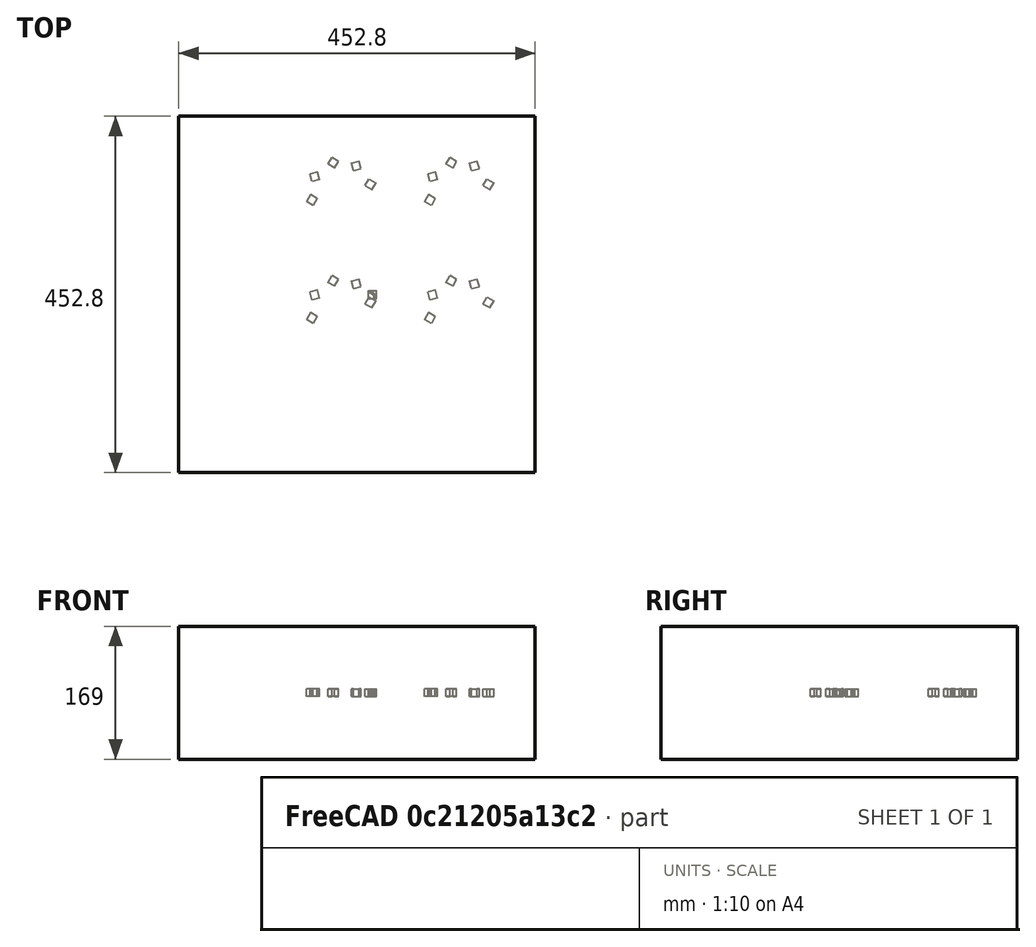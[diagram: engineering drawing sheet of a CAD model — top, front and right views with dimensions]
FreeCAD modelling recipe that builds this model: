
FCSTD DOCUMENT  (FreeCAD 0.21R33694 (Git))
Label: orthoArray-of-polarArray-of-Part
License: All rights reserved
LicenseURL: http://en.wikipedia.org/wiki/All_rights_reserved
objects: App::DocumentObjectGroupPython×1251, Part::FeaturePython×5, App::Part×5
note: 4 computed .brp shape members not serialized (recipe doc carries the construction recipe); baked Part::Feature solids carry a one-line shape summary decoded from their .brp

FEATURE [App::DocumentObjectGroupPython] HALFPI  # scripted group (container) (typed FeaturePython)
  name = HALFPI
  value = pi/2.
FEATURE [App::DocumentObjectGroupPython] PI  # scripted group (container) (typed FeaturePython)
  name = PI
  value = 1.*pi
FEATURE [App::DocumentObjectGroupPython] TWOPI  # scripted group (container) (typed FeaturePython)
  name = TWOPI
  value = 2.*pi
FEATURE [App::DocumentObjectGroupPython] Constants  # scripted group (container) (typed FeaturePython)
  Group = -> [HALFPI,PI,TWOPI]
FEATURE [App::DocumentObjectGroupPython] Variables  # scripted group (container) (typed FeaturePython)
FEATURE [App::DocumentObjectGroupPython] Quantities  # scripted group (container) (typed FeaturePython)
FEATURE [App::DocumentObjectGroupPython] Isotopes  # scripted group (container) (typed FeaturePython)
FEATURE [App::DocumentObjectGroupPython] Elements  # scripted group (container) (typed FeaturePython)
FEATURE [App::DocumentObjectGroupPython] Matrix  # scripted group (container) (typed FeaturePython)
FEATURE [App::DocumentObjectGroupPython] Surfaces  # scripted group (container) (typed FeaturePython)
FEATURE [App::DocumentObjectGroupPython] Opticals  # scripted group (container) (typed FeaturePython)
  Group = -> [Matrix,Surfaces]
FEATURE [App::DocumentObjectGroupPython] G4Isotopes  # scripted group (container) (typed FeaturePython)
FEATURE [App::DocumentObjectGroupPython] H_element  # scripted group (container) (typed FeaturePython)
  Z = 1
  atom_value = 1.008
  formula = H
  name = H_element
FEATURE [App::DocumentObjectGroupPython] He_element  # scripted group (container) (typed FeaturePython)
  Z = 2
  atom_value = 4.0026
  formula = He
  name = He_element
FEATURE [App::DocumentObjectGroupPython] Li_element  # scripted group (container) (typed FeaturePython)
  Z = 3
  atom_value = 6.94
  formula = Li
  name = Li_element
FEATURE [App::DocumentObjectGroupPython] Be_element  # scripted group (container) (typed FeaturePython)
  Z = 4
  atom_value = 9.01218
  formula = Be
  name = Be_element
FEATURE [App::DocumentObjectGroupPython] B_element  # scripted group (container) (typed FeaturePython)
  Z = 5
  atom_value = 10.81
  formula = B
  name = B_element
FEATURE [App::DocumentObjectGroupPython] C_element  # scripted group (container) (typed FeaturePython)
  Z = 6
  atom_value = 12.011
  formula = C
  name = C_element
FEATURE [App::DocumentObjectGroupPython] N_element  # scripted group (container) (typed FeaturePython)
  Z = 7
  atom_value = 14.007
  formula = N
  name = N_element
FEATURE [App::DocumentObjectGroupPython] O_element  # scripted group (container) (typed FeaturePython)
  Z = 8
  atom_value = 15.999
  formula = O
  name = O_element
FEATURE [App::DocumentObjectGroupPython] F_element  # scripted group (container) (typed FeaturePython)
  Z = 9
  atom_value = 18.9984
  formula = F
  name = F_element
FEATURE [App::DocumentObjectGroupPython] Ne_element  # scripted group (container) (typed FeaturePython)
  Z = 10
  atom_value = 20.1797
  formula = Ne
  name = Ne_element
FEATURE [App::DocumentObjectGroupPython] Na_element  # scripted group (container) (typed FeaturePython)
  Z = 11
  atom_value = 22.9898
  formula = Na
  name = Na_element
FEATURE [App::DocumentObjectGroupPython] Mg_element  # scripted group (container) (typed FeaturePython)
  Z = 12
  atom_value = 24.305
  formula = Mg
  name = Mg_element
FEATURE [App::DocumentObjectGroupPython] Al_element  # scripted group (container) (typed FeaturePython)
  Z = 13
  atom_value = 26.9815
  formula = Al
  name = Al_element
FEATURE [App::DocumentObjectGroupPython] Si_element  # scripted group (container) (typed FeaturePython)
  Z = 14
  atom_value = 28.085
  formula = Si
  name = Si_element
FEATURE [App::DocumentObjectGroupPython] P_element  # scripted group (container) (typed FeaturePython)
  Z = 15
  atom_value = 30.9738
  formula = P
  name = P_element
FEATURE [App::DocumentObjectGroupPython] S_element  # scripted group (container) (typed FeaturePython)
  Z = 16
  atom_value = 32.06
  formula = S
  name = S_element
FEATURE [App::DocumentObjectGroupPython] Cl_element  # scripted group (container) (typed FeaturePython)
  Z = 17
  atom_value = 35.45
  formula = Cl
  name = Cl_element
FEATURE [App::DocumentObjectGroupPython] Ar_element  # scripted group (container) (typed FeaturePython)
  Z = 18
  atom_value = 39.95
  formula = Ar
  name = Ar_element
FEATURE [App::DocumentObjectGroupPython] K_element  # scripted group (container) (typed FeaturePython)
  Z = 19
  atom_value = 39.0983
  formula = K
  name = K_element
FEATURE [App::DocumentObjectGroupPython] Ca_element  # scripted group (container) (typed FeaturePython)
  Z = 20
  atom_value = 40.078
  formula = Ca
  name = Ca_element
FEATURE [App::DocumentObjectGroupPython] Sc_element  # scripted group (container) (typed FeaturePython)
  Z = 21
  atom_value = 44.9559
  formula = Sc
  name = Sc_element
FEATURE [App::DocumentObjectGroupPython] Ti_element  # scripted group (container) (typed FeaturePython)
  Z = 22
  atom_value = 47.867
  formula = Ti
  name = Ti_element
FEATURE [App::DocumentObjectGroupPython] V_element  # scripted group (container) (typed FeaturePython)
  Z = 23
  atom_value = 50.9415
  formula = V
  name = V_element
FEATURE [App::DocumentObjectGroupPython] Cr_element  # scripted group (container) (typed FeaturePython)
  Z = 24
  atom_value = 51.9961
  formula = Cr
  name = Cr_element
FEATURE [App::DocumentObjectGroupPython] Mn_element  # scripted group (container) (typed FeaturePython)
  Z = 25
  atom_value = 54.938
  formula = Mn
  name = Mn_element
FEATURE [App::DocumentObjectGroupPython] Fe_element  # scripted group (container) (typed FeaturePython)
  Z = 26
  atom_value = 55.845
  formula = Fe
  name = Fe_element
FEATURE [App::DocumentObjectGroupPython] Co_element  # scripted group (container) (typed FeaturePython)
  Z = 27
  atom_value = 58.9332
  formula = Co
  name = Co_element
FEATURE [App::DocumentObjectGroupPython] Ni_element  # scripted group (container) (typed FeaturePython)
  Z = 28
  atom_value = 58.6934
  formula = Ni
  name = Ni_element
FEATURE [App::DocumentObjectGroupPython] Cu_element  # scripted group (container) (typed FeaturePython)
  Z = 29
  atom_value = 63.546
  formula = Cu
  name = Cu_element
FEATURE [App::DocumentObjectGroupPython] Zn_element  # scripted group (container) (typed FeaturePython)
  Z = 30
  atom_value = 65.38
  formula = Zn
  name = Zn_element
FEATURE [App::DocumentObjectGroupPython] Ga_element  # scripted group (container) (typed FeaturePython)
  Z = 31
  atom_value = 69.723
  formula = Ga
  name = Ga_element
FEATURE [App::DocumentObjectGroupPython] Ge_element  # scripted group (container) (typed FeaturePython)
  Z = 32
  atom_value = 72.63
  formula = Ge
  name = Ge_element
FEATURE [App::DocumentObjectGroupPython] As_element  # scripted group (container) (typed FeaturePython)
  Z = 33
  atom_value = 74.9216
  formula = As
  name = As_element
FEATURE [App::DocumentObjectGroupPython] Se_element  # scripted group (container) (typed FeaturePython)
  Z = 34
  atom_value = 78.971
  formula = Se
  name = Se_element
FEATURE [App::DocumentObjectGroupPython] Br_element  # scripted group (container) (typed FeaturePython)
  Z = 35
  atom_value = 79.904
  formula = Br
  name = Br_element
FEATURE [App::DocumentObjectGroupPython] Kr_element  # scripted group (container) (typed FeaturePython)
  Z = 36
  atom_value = 83.798
  formula = Kr
  name = Kr_element
FEATURE [App::DocumentObjectGroupPython] Rb_element  # scripted group (container) (typed FeaturePython)
  Z = 37
  atom_value = 85.4678
  formula = Rb
  name = Rb_element
FEATURE [App::DocumentObjectGroupPython] Sr_element  # scripted group (container) (typed FeaturePython)
  Z = 38
  atom_value = 87.62
  formula = Sr
  name = Sr_element
FEATURE [App::DocumentObjectGroupPython] Y_element  # scripted group (container) (typed FeaturePython)
  Z = 39
  atom_value = 88.9058
  formula = Y
  name = Y_element
FEATURE [App::DocumentObjectGroupPython] Zr_element  # scripted group (container) (typed FeaturePython)
  Z = 40
  atom_value = 91.224
  formula = Zr
  name = Zr_element
FEATURE [App::DocumentObjectGroupPython] Nb_element  # scripted group (container) (typed FeaturePython)
  Z = 41
  atom_value = 92.9064
  formula = Nb
  name = Nb_element
FEATURE [App::DocumentObjectGroupPython] Mo_element  # scripted group (container) (typed FeaturePython)
  Z = 42
  atom_value = 95.95
  formula = Mo
  name = Mo_element
FEATURE [App::DocumentObjectGroupPython] Tc_element  # scripted group (container) (typed FeaturePython)
  Z = 43
  atom_value = 97
  formula = Tc
  name = Tc_element
FEATURE [App::DocumentObjectGroupPython] Ru_element  # scripted group (container) (typed FeaturePython)
  Z = 44
  atom_value = 101.07
  formula = Ru
  name = Ru_element
FEATURE [App::DocumentObjectGroupPython] Rh_element  # scripted group (container) (typed FeaturePython)
  Z = 45
  atom_value = 102.905
  formula = Rh
  name = Rh_element
FEATURE [App::DocumentObjectGroupPython] Pd_element  # scripted group (container) (typed FeaturePython)
  Z = 46
  atom_value = 106.42
  formula = Pd
  name = Pd_element
FEATURE [App::DocumentObjectGroupPython] Ag_element  # scripted group (container) (typed FeaturePython)
  Z = 47
  atom_value = 107.868
  formula = Ag
  name = Ag_element
FEATURE [App::DocumentObjectGroupPython] Cd_element  # scripted group (container) (typed FeaturePython)
  Z = 48
  atom_value = 112.414
  formula = Cd
  name = Cd_element
FEATURE [App::DocumentObjectGroupPython] In_element  # scripted group (container) (typed FeaturePython)
  Z = 49
  atom_value = 114.818
  formula = In
  name = In_element
FEATURE [App::DocumentObjectGroupPython] Sn_element  # scripted group (container) (typed FeaturePython)
  Z = 50
  atom_value = 118.71
  formula = Sn
  name = Sn_element
FEATURE [App::DocumentObjectGroupPython] Sb_element  # scripted group (container) (typed FeaturePython)
  Z = 51
  atom_value = 121.76
  formula = Sb
  name = Sb_element
FEATURE [App::DocumentObjectGroupPython] Te_element  # scripted group (container) (typed FeaturePython)
  Z = 52
  atom_value = 127.6
  formula = Te
  name = Te_element
FEATURE [App::DocumentObjectGroupPython] I_element  # scripted group (container) (typed FeaturePython)
  Z = 53
  atom_value = 126.904
  formula = I
  name = I_element
FEATURE [App::DocumentObjectGroupPython] Xe_element  # scripted group (container) (typed FeaturePython)
  Z = 54
  atom_value = 131.293
  formula = Xe
  name = Xe_element
FEATURE [App::DocumentObjectGroupPython] Cs_element  # scripted group (container) (typed FeaturePython)
  Z = 55
  atom_value = 132.905
  formula = Cs
  name = Cs_element
FEATURE [App::DocumentObjectGroupPython] Ba_element  # scripted group (container) (typed FeaturePython)
  Z = 56
  atom_value = 137.327
  formula = Ba
  name = Ba_element
FEATURE [App::DocumentObjectGroupPython] La_element  # scripted group (container) (typed FeaturePython)
  Z = 57
  atom_value = 138.905
  formula = La
  name = La_element
FEATURE [App::DocumentObjectGroupPython] Ce_element  # scripted group (container) (typed FeaturePython)
  Z = 58
  atom_value = 140.116
  formula = Ce
  name = Ce_element
FEATURE [App::DocumentObjectGroupPython] Pr_element  # scripted group (container) (typed FeaturePython)
  Z = 59
  atom_value = 140.908
  formula = Pr
  name = Pr_element
FEATURE [App::DocumentObjectGroupPython] Nd_element  # scripted group (container) (typed FeaturePython)
  Z = 60
  atom_value = 144.242
  formula = Nd
  name = Nd_element
FEATURE [App::DocumentObjectGroupPython] Pm_element  # scripted group (container) (typed FeaturePython)
  Z = 61
  atom_value = 145
  formula = Pm
  name = Pm_element
FEATURE [App::DocumentObjectGroupPython] Sm_element  # scripted group (container) (typed FeaturePython)
  Z = 62
  atom_value = 150.36
  formula = Sm
  name = Sm_element
FEATURE [App::DocumentObjectGroupPython] Eu_element  # scripted group (container) (typed FeaturePython)
  Z = 63
  atom_value = 151.964
  formula = Eu
  name = Eu_element
FEATURE [App::DocumentObjectGroupPython] Gd_element  # scripted group (container) (typed FeaturePython)
  Z = 64
  atom_value = 157.25
  formula = Gd
  name = Gd_element
FEATURE [App::DocumentObjectGroupPython] Tb_element  # scripted group (container) (typed FeaturePython)
  Z = 65
  atom_value = 158.925
  formula = Tb
  name = Tb_element
FEATURE [App::DocumentObjectGroupPython] Dy_element  # scripted group (container) (typed FeaturePython)
  Z = 66
  atom_value = 162.5
  formula = Dy
  name = Dy_element
FEATURE [App::DocumentObjectGroupPython] Ho_element  # scripted group (container) (typed FeaturePython)
  Z = 67
  atom_value = 164.93
  formula = Ho
  name = Ho_element
FEATURE [App::DocumentObjectGroupPython] Er_element  # scripted group (container) (typed FeaturePython)
  Z = 68
  atom_value = 167.259
  formula = Er
  name = Er_element
FEATURE [App::DocumentObjectGroupPython] Tm_element  # scripted group (container) (typed FeaturePython)
  Z = 69
  atom_value = 168.934
  formula = Tm
  name = Tm_element
FEATURE [App::DocumentObjectGroupPython] Yb_element  # scripted group (container) (typed FeaturePython)
  Z = 70
  atom_value = 173.045
  formula = Yb
  name = Yb_element
FEATURE [App::DocumentObjectGroupPython] Lu_element  # scripted group (container) (typed FeaturePython)
  Z = 71
  atom_value = 174.967
  formula = Lu
  name = Lu_element
FEATURE [App::DocumentObjectGroupPython] Hf_element  # scripted group (container) (typed FeaturePython)
  Z = 72
  atom_value = 178.49
  formula = Hf
  name = Hf_element
FEATURE [App::DocumentObjectGroupPython] Ta_element  # scripted group (container) (typed FeaturePython)
  Z = 73
  atom_value = 180.948
  formula = Ta
  name = Ta_element
FEATURE [App::DocumentObjectGroupPython] W_element  # scripted group (container) (typed FeaturePython)
  Z = 74
  atom_value = 183.84
  formula = W
  name = W_element
FEATURE [App::DocumentObjectGroupPython] Re_element  # scripted group (container) (typed FeaturePython)
  Z = 75
  atom_value = 186.207
  formula = Re
  name = Re_element
FEATURE [App::DocumentObjectGroupPython] Os_element  # scripted group (container) (typed FeaturePython)
  Z = 76
  atom_value = 190.23
  formula = Os
  name = Os_element
FEATURE [App::DocumentObjectGroupPython] Ir_element  # scripted group (container) (typed FeaturePython)
  Z = 77
  atom_value = 192.217
  formula = Ir
  name = Ir_element
FEATURE [App::DocumentObjectGroupPython] Pt_element  # scripted group (container) (typed FeaturePython)
  Z = 78
  atom_value = 195.084
  formula = Pt
  name = Pt_element
FEATURE [App::DocumentObjectGroupPython] Au_element  # scripted group (container) (typed FeaturePython)
  Z = 79
  atom_value = 196.967
  formula = Au
  name = Au_element
FEATURE [App::DocumentObjectGroupPython] Hg_element  # scripted group (container) (typed FeaturePython)
  Z = 80
  atom_value = 200.592
  formula = Hg
  name = Hg_element
FEATURE [App::DocumentObjectGroupPython] Tl_element  # scripted group (container) (typed FeaturePython)
  Z = 81
  atom_value = 204.38
  formula = Tl
  name = Tl_element
FEATURE [App::DocumentObjectGroupPython] Pb_element  # scripted group (container) (typed FeaturePython)
  Z = 82
  atom_value = 207.2
  formula = Pb
  name = Pb_element
FEATURE [App::DocumentObjectGroupPython] Bi_element  # scripted group (container) (typed FeaturePython)
  Z = 83
  atom_value = 208.98
  formula = Bi
  name = Bi_element
FEATURE [App::DocumentObjectGroupPython] Po_element  # scripted group (container) (typed FeaturePython)
  Z = 84
  atom_value = 209
  formula = Po
  name = Po_element
FEATURE [App::DocumentObjectGroupPython] At_element  # scripted group (container) (typed FeaturePython)
  Z = 85
  atom_value = 210
  formula = At
  name = At_element
FEATURE [App::DocumentObjectGroupPython] Rn_element  # scripted group (container) (typed FeaturePython)
  Z = 86
  atom_value = 222
  formula = Rn
  name = Rn_element
FEATURE [App::DocumentObjectGroupPython] Fr_element  # scripted group (container) (typed FeaturePython)
  Z = 87
  atom_value = 223
  formula = Fr
  name = Fr_element
FEATURE [App::DocumentObjectGroupPython] Ra_element  # scripted group (container) (typed FeaturePython)
  Z = 88
  atom_value = 226
  formula = Ra
  name = Ra_element
FEATURE [App::DocumentObjectGroupPython] Ac_element  # scripted group (container) (typed FeaturePython)
  Z = 89
  atom_value = 227
  formula = Ac
  name = Ac_element
FEATURE [App::DocumentObjectGroupPython] Th_element  # scripted group (container) (typed FeaturePython)
  Z = 90
  atom_value = 232.038
  formula = Th
  name = Th_element
FEATURE [App::DocumentObjectGroupPython] Pa_element  # scripted group (container) (typed FeaturePython)
  Z = 91
  atom_value = 231.036
  formula = Pa
  name = Pa_element
FEATURE [App::DocumentObjectGroupPython] U_element  # scripted group (container) (typed FeaturePython)
  Z = 92
  atom_value = 238.029
  formula = U
  name = U_element
FEATURE [App::DocumentObjectGroupPython] Np_element  # scripted group (container) (typed FeaturePython)
  Z = 93
  atom_value = 237
  formula = Np
  name = Np_element
FEATURE [App::DocumentObjectGroupPython] Pu_element  # scripted group (container) (typed FeaturePython)
  Z = 94
  atom_value = 244
  formula = Pu
  name = Pu_element
FEATURE [App::DocumentObjectGroupPython] Am_element  # scripted group (container) (typed FeaturePython)
  Z = 95
  atom_value = 243
  formula = Am
  name = Am_element
FEATURE [App::DocumentObjectGroupPython] Cm_element  # scripted group (container) (typed FeaturePython)
  Z = 96
  atom_value = 247
  formula = Cm
  name = Cm_element
FEATURE [App::DocumentObjectGroupPython] Bk_element  # scripted group (container) (typed FeaturePython)
  Z = 97
  atom_value = 247
  formula = Bk
  name = Bk_element
FEATURE [App::DocumentObjectGroupPython] Cf_element  # scripted group (container) (typed FeaturePython)
  Z = 98
  atom_value = 251
  formula = Cf
  name = Cf_element
FEATURE [App::DocumentObjectGroupPython] G4Elements  # scripted group (container) (typed FeaturePython)
  Group = -> [H_element,He_element,Li_element,Be_element,B_element,C_element,N_element,O_element,F_element,Ne_element,Na_element,Mg_element,Al_element,Si_element,P_element,S_element,Cl_element,Ar_element,K_element,Ca_element,Sc_element,Ti_element,V_element,Cr_element,Mn_element,Fe_element,Co_element,Ni_element,Cu_element,Zn_element,Ga_element,Ge_element,As_element,Se_element,Br_element,Kr_element,Rb_element,+61 more]
FEATURE [App::DocumentObjectGroupPython] H_element001  label="H_element : 0.101"  # scripted group (container) (typed FeaturePython)
  n = 0.101327
FEATURE [App::DocumentObjectGroupPython] C_element001  label="C_element : 0.775"  # scripted group (container) (typed FeaturePython)
  n = 0.7755
FEATURE [App::DocumentObjectGroupPython] N_element001  label="N_element : 0.035"  # scripted group (container) (typed FeaturePython)
  n = 0.035057
FEATURE [App::DocumentObjectGroupPython] O_element001  label="O_element : 0.052"  # scripted group (container) (typed FeaturePython)
  n = 0.0523159
FEATURE [App::DocumentObjectGroupPython] F_element001  label="F_element : 0.017"  # scripted group (container) (typed FeaturePython)
  n = 0.017422
FEATURE [App::DocumentObjectGroupPython] Ca_element001  label="Ca_element : 0.018"  # scripted group (container) (typed FeaturePython)
  n = 0.018378
FEATURE [App::DocumentObjectGroupPython] G4_A_150_TISSUE  label="G4_A-150_TISSUE"  # scripted group (container) (typed FeaturePython)
  Dunit = g/cm3
  Dvalue = 1.127
  Group = -> [H_element001,C_element001,N_element001,O_element001,F_element001,Ca_element001]
  conduct = 2
  density = 1
  expand = 3
  formula = G4_A-150_TISSUE
  name = G4_A-150_TISSUE
  specific = 4
FEATURE [App::DocumentObjectGroupPython] C_element002  label="C_element : 3"  # scripted group (container) (typed FeaturePython)
  n = 3
  ref = C_element
FEATURE [App::DocumentObjectGroupPython] H_element002  label="H_element : 6"  # scripted group (container) (typed FeaturePython)
  n = 6
  ref = H_element
FEATURE [App::DocumentObjectGroupPython] O_element002  label="O_element : 1"  # scripted group (container) (typed FeaturePython)
  n = 1
  ref = O_element
FEATURE [App::DocumentObjectGroupPython] G4_ACETONE  # scripted group (container) (typed FeaturePython)
  Dunit = g/cm3
  Dvalue = 0.7899
  Group = -> [C_element002,H_element002,O_element002]
  conduct = 2
  density = 1
  expand = 3
  formula = G4_ACETONE
  name = G4_ACETONE
  specific = 4
FEATURE [App::DocumentObjectGroupPython] C_element003  label="C_element : 2"  # scripted group (container) (typed FeaturePython)
  n = 2
  ref = C_element
FEATURE [App::DocumentObjectGroupPython] H_element003  label="H_element : 2"  # scripted group (container) (typed FeaturePython)
  n = 2
  ref = H_element
FEATURE [App::DocumentObjectGroupPython] G4_ACETYLENE  # scripted group (container) (typed FeaturePython)
  Dunit = g/cm3
  Dvalue = 0.0010967
  Group = -> [C_element003,H_element003]
  conduct = 2
  density = 1
  expand = 3
  formula = G4_ACETYLENE
  name = G4_ACETYLENE
  specific = 4
FEATURE [App::DocumentObjectGroupPython] C_element004  label="C_element : 5"  # scripted group (container) (typed FeaturePython)
  n = 5
  ref = C_element
FEATURE [App::DocumentObjectGroupPython] H_element004  label="H_element : 5"  # scripted group (container) (typed FeaturePython)
  n = 5
  ref = H_element
FEATURE [App::DocumentObjectGroupPython] N_element002  label="N_element : 5"  # scripted group (container) (typed FeaturePython)
  n = 5
  ref = N_element
FEATURE [App::DocumentObjectGroupPython] G4_ADENINE  # scripted group (container) (typed FeaturePython)
  Dunit = g/cm3
  Dvalue = 1.6
  Group = -> [C_element004,H_element004,N_element002]
  conduct = 2
  density = 1
  expand = 3
  formula = G4_ADENINE
  name = G4_ADENINE
  specific = 4
FEATURE [App::DocumentObjectGroupPython] H_element005  label="H_element : 0.114"  # scripted group (container) (typed FeaturePython)
  n = 0.114
FEATURE [App::DocumentObjectGroupPython] C_element005  label="C_element : 0.598"  # scripted group (container) (typed FeaturePython)
  n = 0.598
FEATURE [App::DocumentObjectGroupPython] N_element003  label="N_element : 0.007"  # scripted group (container) (typed FeaturePython)
  n = 0.007
FEATURE [App::DocumentObjectGroupPython] O_element003  label="O_element : 0.278"  # scripted group (container) (typed FeaturePython)
  n = 0.278
FEATURE [App::DocumentObjectGroupPython] Na_element001  label="Na_element : 0.001"  # scripted group (container) (typed FeaturePython)
  n = 0.001
FEATURE [App::DocumentObjectGroupPython] S_element001  label="S_element : 0.001"  # scripted group (container) (typed FeaturePython)
  n = 0.001
FEATURE [App::DocumentObjectGroupPython] Cl_element001  label="Cl_element : 0.001"  # scripted group (container) (typed FeaturePython)
  n = 0.001
FEATURE [App::DocumentObjectGroupPython] G4_ADIPOSE_TISSUE_ICRP  # scripted group (container) (typed FeaturePython)
  Dunit = g/cm3
  Dvalue = 0.95
  Group = -> [H_element005,C_element005,N_element003,O_element003,Na_element001,S_element001,Cl_element001]
  conduct = 2
  density = 1
  expand = 3
  formula = G4_ADIPOSE_TISSUE_ICRP
  name = G4_ADIPOSE_TISSUE_ICRP
  specific = 4
FEATURE [App::DocumentObjectGroupPython] C_element006  label="C_element : 0.000"  # scripted group (container) (typed FeaturePython)
  n = 0.000124
FEATURE [App::DocumentObjectGroupPython] N_element004  label="N_element : 0.755"  # scripted group (container) (typed FeaturePython)
  n = 0.755268
FEATURE [App::DocumentObjectGroupPython] O_element004  label="O_element : 0.232"  # scripted group (container) (typed FeaturePython)
  n = 0.231781
FEATURE [App::DocumentObjectGroupPython] Ar_element001  label="Ar_element : 0.013"  # scripted group (container) (typed FeaturePython)
  n = 0.012827
FEATURE [App::DocumentObjectGroupPython] G4_AIR  # scripted group (container) (typed FeaturePython)
  Dunit = g/cm3
  Dvalue = 0.00120479
  Group = -> [C_element006,N_element004,O_element004,Ar_element001]
  conduct = 2
  density = 1
  expand = 3
  formula = G4_AIR
  name = G4_AIR
  specific = 4
FEATURE [App::DocumentObjectGroupPython] C_element007  label="C_element : 006"  # scripted group (container) (typed FeaturePython)
  n = 3
  ref = C_element
FEATURE [App::DocumentObjectGroupPython] H_element006  label="H_element : 7"  # scripted group (container) (typed FeaturePython)
  n = 7
  ref = H_element
FEATURE [App::DocumentObjectGroupPython] N_element005  label="N_element : 1"  # scripted group (container) (typed FeaturePython)
  n = 1
  ref = N_element
FEATURE [App::DocumentObjectGroupPython] O_element005  label="O_element : 2"  # scripted group (container) (typed FeaturePython)
  n = 2
  ref = O_element
FEATURE [App::DocumentObjectGroupPython] G4_ALANINE  # scripted group (container) (typed FeaturePython)
  Dunit = g/cm3
  Dvalue = 1.42
  Group = -> [C_element007,H_element006,N_element005,O_element005]
  conduct = 2
  density = 1
  expand = 3
  formula = G4_ALANINE
  name = G4_ALANINE
  specific = 4
FEATURE [App::DocumentObjectGroupPython] Al_element001  label="Al_element : 2"  # scripted group (container) (typed FeaturePython)
  n = 2
  ref = Al_element
FEATURE [App::DocumentObjectGroupPython] O_element006  label="O_element : 3"  # scripted group (container) (typed FeaturePython)
  n = 3
  ref = O_element
FEATURE [App::DocumentObjectGroupPython] G4_ALUMINUM_OXIDE  # scripted group (container) (typed FeaturePython)
  Dunit = g/cm3
  Dvalue = 3.97
  Group = -> [Al_element001,O_element006]
  conduct = 2
  density = 1
  expand = 3
  formula = G4_ALUMINUM_OXIDE
  name = G4_ALUMINUM_OXIDE
  specific = 4
FEATURE [App::DocumentObjectGroupPython] H_element007  label="H_element : 0.106"  # scripted group (container) (typed FeaturePython)
  n = 0.10593
FEATURE [App::DocumentObjectGroupPython] C_element008  label="C_element : 0.789"  # scripted group (container) (typed FeaturePython)
  n = 0.788974
FEATURE [App::DocumentObjectGroupPython] O_element007  label="O_element : 0.105"  # scripted group (container) (typed FeaturePython)
  n = 0.105096
FEATURE [App::DocumentObjectGroupPython] G4_AMBER  # scripted group (container) (typed FeaturePython)
  Dunit = g/cm3
  Dvalue = 1.1
  Group = -> [H_element007,C_element008,O_element007]
  conduct = 2
  density = 1
  expand = 3
  formula = G4_AMBER
  name = G4_AMBER
  specific = 4
FEATURE [App::DocumentObjectGroupPython] N_element006  label="N_element : 006"  # scripted group (container) (typed FeaturePython)
  n = 1
  ref = N_element
FEATURE [App::DocumentObjectGroupPython] H_element008  label="H_element : 3"  # scripted group (container) (typed FeaturePython)
  n = 3
  ref = H_element
FEATURE [App::DocumentObjectGroupPython] G4_AMMONIA  # scripted group (container) (typed FeaturePython)
  Dunit = g/cm3
  Dvalue = 0.000826019
  Group = -> [N_element006,H_element008]
  conduct = 2
  density = 1
  expand = 3
  formula = G4_AMMONIA
  name = G4_AMMONIA
  specific = 4
FEATURE [App::DocumentObjectGroupPython] C_element009  label="C_element : 6"  # scripted group (container) (typed FeaturePython)
  n = 6
  ref = C_element
FEATURE [App::DocumentObjectGroupPython] H_element009  label="H_element : 008"  # scripted group (container) (typed FeaturePython)
  n = 7
  ref = H_element
FEATURE [App::DocumentObjectGroupPython] N_element007  label="N_element : 007"  # scripted group (container) (typed FeaturePython)
  n = 1
  ref = N_element
FEATURE [App::DocumentObjectGroupPython] G4_ANILINE  # scripted group (container) (typed FeaturePython)
  Dunit = g/cm3
  Dvalue = 1.0235
  Group = -> [C_element009,H_element009,N_element007]
  conduct = 2
  density = 1
  expand = 3
  formula = G4_ANILINE
  name = G4_ANILINE
  specific = 4
FEATURE [App::DocumentObjectGroupPython] C_element010  label="C_element : 14"  # scripted group (container) (typed FeaturePython)
  n = 14
  ref = C_element
FEATURE [App::DocumentObjectGroupPython] H_element010  label="H_element : 10"  # scripted group (container) (typed FeaturePython)
  n = 10
  ref = H_element
FEATURE [App::DocumentObjectGroupPython] G4_ANTHRACENE  # scripted group (container) (typed FeaturePython)
  Dunit = g/cm3
  Dvalue = 1.283
  Group = -> [C_element010,H_element010]
  conduct = 2
  density = 1
  expand = 3
  formula = G4_ANTHRACENE
  name = G4_ANTHRACENE
  specific = 4
FEATURE [App::DocumentObjectGroupPython] H_element011  label="H_element : 0.065"  # scripted group (container) (typed FeaturePython)
  n = 0.0654709
FEATURE [App::DocumentObjectGroupPython] C_element011  label="C_element : 0.537"  # scripted group (container) (typed FeaturePython)
  n = 0.536944
FEATURE [App::DocumentObjectGroupPython] N_element008  label="N_element : 0.021"  # scripted group (container) (typed FeaturePython)
  n = 0.0215
FEATURE [App::DocumentObjectGroupPython] O_element008  label="O_element : 0.032"  # scripted group (container) (typed FeaturePython)
  n = 0.032085
FEATURE [App::DocumentObjectGroupPython] F_element002  label="F_element : 0.167"  # scripted group (container) (typed FeaturePython)
  n = 0.167411
FEATURE [App::DocumentObjectGroupPython] Ca_element002  label="Ca_element : 0.177"  # scripted group (container) (typed FeaturePython)
  n = 0.176589
FEATURE [App::DocumentObjectGroupPython] G4_B_100_BONE  label="G4_B-100_BONE"  # scripted group (container) (typed FeaturePython)
  Dunit = g/cm3
  Dvalue = 1.45
  Group = -> [H_element011,C_element011,N_element008,O_element008,F_element002,Ca_element002]
  conduct = 2
  density = 1
  expand = 3
  formula = G4_B-100_BONE
  name = G4_B-100_BONE
  specific = 4
FEATURE [App::DocumentObjectGroupPython] H_element012  label="H_element : 0.057"  # scripted group (container) (typed FeaturePython)
  n = 0.057441
FEATURE [App::DocumentObjectGroupPython] C_element012  label="C_element : 0.790"  # scripted group (container) (typed FeaturePython)
  n = 0.774591
FEATURE [App::DocumentObjectGroupPython] O_element009  label="O_element : 0.168"  # scripted group (container) (typed FeaturePython)
  n = 0.167968
FEATURE [App::DocumentObjectGroupPython] G4_BAKELITE  # scripted group (container) (typed FeaturePython)
  Dunit = g/cm3
  Dvalue = 1.25
  Group = -> [H_element012,C_element012,O_element009]
  conduct = 2
  density = 1
  expand = 3
  formula = G4_BAKELITE
  name = G4_BAKELITE
  specific = 4
FEATURE [App::DocumentObjectGroupPython] Ba_element001  label="Ba_element : 1"  # scripted group (container) (typed FeaturePython)
  n = 1
  ref = Ba_element
FEATURE [App::DocumentObjectGroupPython] F_element003  label="F_element : 2"  # scripted group (container) (typed FeaturePython)
  n = 2
  ref = F_element
FEATURE [App::DocumentObjectGroupPython] G4_BARIUM_FLUORIDE  # scripted group (container) (typed FeaturePython)
  Dunit = g/cm3
  Dvalue = 4.89
  Group = -> [Ba_element001,F_element003]
  conduct = 2
  density = 1
  expand = 3
  formula = G4_BARIUM_FLUORIDE
  name = G4_BARIUM_FLUORIDE
  specific = 4
FEATURE [App::DocumentObjectGroupPython] Ba_element002  label="Ba_element : 002"  # scripted group (container) (typed FeaturePython)
  n = 1
  ref = Ba_element
FEATURE [App::DocumentObjectGroupPython] S_element002  label="S_element : 1"  # scripted group (container) (typed FeaturePython)
  n = 1
  ref = S_element
FEATURE [App::DocumentObjectGroupPython] O_element010  label="O_element : 4"  # scripted group (container) (typed FeaturePython)
  n = 4
  ref = O_element
FEATURE [App::DocumentObjectGroupPython] G4_BARIUM_SULFATE  # scripted group (container) (typed FeaturePython)
  Dunit = g/cm3
  Dvalue = 4.5
  Group = -> [Ba_element002,S_element002,O_element010]
  conduct = 2
  density = 1
  expand = 3
  formula = G4_BARIUM_SULFATE
  name = G4_BARIUM_SULFATE
  specific = 4
FEATURE [App::DocumentObjectGroupPython] C_element013  label="C_element : 007"  # scripted group (container) (typed FeaturePython)
  n = 6
  ref = C_element
FEATURE [App::DocumentObjectGroupPython] H_element013  label="H_element : 009"  # scripted group (container) (typed FeaturePython)
  n = 6
  ref = H_element
FEATURE [App::DocumentObjectGroupPython] G4_BENZENE  # scripted group (container) (typed FeaturePython)
  Dunit = g/cm3
  Dvalue = 0.87865
  Group = -> [C_element013,H_element013]
  conduct = 2
  density = 1
  expand = 3
  formula = G4_BENZENE
  name = G4_BENZENE
  specific = 4
FEATURE [App::DocumentObjectGroupPython] Be_element001  label="Be_element : 1"  # scripted group (container) (typed FeaturePython)
  n = 1
  ref = Be_element
FEATURE [App::DocumentObjectGroupPython] O_element011  label="O_element : 005"  # scripted group (container) (typed FeaturePython)
  n = 1
  ref = O_element
FEATURE [App::DocumentObjectGroupPython] G4_BERYLLIUM_OXIDE  # scripted group (container) (typed FeaturePython)
  Dunit = g/cm3
  Dvalue = 3.01
  Group = -> [Be_element001,O_element011]
  conduct = 2
  density = 1
  expand = 3
  formula = G4_BERYLLIUM_OXIDE
  name = G4_BERYLLIUM_OXIDE
  specific = 4
FEATURE [App::DocumentObjectGroupPython] Bi_element001  label="Bi_element : 4"  # scripted group (container) (typed FeaturePython)
  n = 4
  ref = Bi_element
FEATURE [App::DocumentObjectGroupPython] Ge_element001  label="Ge_element : 3"  # scripted group (container) (typed FeaturePython)
  n = 3
  ref = Ge_element
FEATURE [App::DocumentObjectGroupPython] O_element012  label="O_element : 12"  # scripted group (container) (typed FeaturePython)
  n = 12
  ref = O_element
FEATURE [App::DocumentObjectGroupPython] G4_BGO  # scripted group (container) (typed FeaturePython)
  Dunit = g/cm3
  Dvalue = 7.13
  Group = -> [Bi_element001,Ge_element001,O_element012]
  conduct = 2
  density = 1
  expand = 3
  formula = G4_BGO
  name = G4_BGO
  specific = 4
FEATURE [App::DocumentObjectGroupPython] H_element014  label="H_element : 0.102"  # scripted group (container) (typed FeaturePython)
  n = 0.102
FEATURE [App::DocumentObjectGroupPython] C_element014  label="C_element : 0.110"  # scripted group (container) (typed FeaturePython)
  n = 0.11
FEATURE [App::DocumentObjectGroupPython] N_element009  label="N_element : 0.033"  # scripted group (container) (typed FeaturePython)
  n = 0.033
FEATURE [App::DocumentObjectGroupPython] O_element013  label="O_element : 0.745"  # scripted group (container) (typed FeaturePython)
  n = 0.745
FEATURE [App::DocumentObjectGroupPython] Na_element002  label="Na_element : 0.002"  # scripted group (container) (typed FeaturePython)
  n = 0.001
FEATURE [App::DocumentObjectGroupPython] P_element001  label="P_element : 0.001"  # scripted group (container) (typed FeaturePython)
  n = 0.001
FEATURE [App::DocumentObjectGroupPython] S_element003  label="S_element : 0.002"  # scripted group (container) (typed FeaturePython)
  n = 0.002
FEATURE [App::DocumentObjectGroupPython] Cl_element002  label="Cl_element : 0.003"  # scripted group (container) (typed FeaturePython)
  n = 0.003
FEATURE [App::DocumentObjectGroupPython] K_element001  label="K_element : 0.002"  # scripted group (container) (typed FeaturePython)
  n = 0.002
FEATURE [App::DocumentObjectGroupPython] Fe_element001  label="Fe_element : 0.001"  # scripted group (container) (typed FeaturePython)
  n = 0.001
FEATURE [App::DocumentObjectGroupPython] G4_BLOOD_ICRP  # scripted group (container) (typed FeaturePython)
  Dunit = g/cm3
  Dvalue = 1.06
  Group = -> [H_element014,C_element014,N_element009,O_element013,Na_element002,P_element001,S_element003,Cl_element002,K_element001,Fe_element001]
  conduct = 2
  density = 1
  expand = 3
  formula = G4_BLOOD_ICRP
  name = G4_BLOOD_ICRP
  specific = 4
FEATURE [App::DocumentObjectGroupPython] H_element015  label="H_element : 0.064"  # scripted group (container) (typed FeaturePython)
  n = 0.064
FEATURE [App::DocumentObjectGroupPython] C_element015  label="C_element : 0.278"  # scripted group (container) (typed FeaturePython)
  n = 0.278
FEATURE [App::DocumentObjectGroupPython] N_element010  label="N_element : 0.027"  # scripted group (container) (typed FeaturePython)
  n = 0.027
FEATURE [App::DocumentObjectGroupPython] O_element014  label="O_element : 0.410"  # scripted group (container) (typed FeaturePython)
  n = 0.41
FEATURE [App::DocumentObjectGroupPython] Mg_element001  label="Mg_element : 0.002"  # scripted group (container) (typed FeaturePython)
  n = 0.002
FEATURE [App::DocumentObjectGroupPython] P_element002  label="P_element : 0.070"  # scripted group (container) (typed FeaturePython)
  n = 0.07
FEATURE [App::DocumentObjectGroupPython] S_element004  label="S_element : 0.003"  # scripted group (container) (typed FeaturePython)
  n = 0.002
FEATURE [App::DocumentObjectGroupPython] Ca_element003  label="Ca_element : 0.147"  # scripted group (container) (typed FeaturePython)
  n = 0.147
FEATURE [App::DocumentObjectGroupPython] G4_BONE_COMPACT_ICRU  # scripted group (container) (typed FeaturePython)
  Dunit = g/cm3
  Dvalue = 1.85
  Group = -> [H_element015,C_element015,N_element010,O_element014,Mg_element001,P_element002,S_element004,Ca_element003]
  conduct = 2
  density = 1
  expand = 3
  formula = G4_BONE_COMPACT_ICRU
  name = G4_BONE_COMPACT_ICRU
  specific = 4
FEATURE [App::DocumentObjectGroupPython] H_element016  label="H_element : 0.034"  # scripted group (container) (typed FeaturePython)
  n = 0.034
FEATURE [App::DocumentObjectGroupPython] C_element016  label="C_element : 0.155"  # scripted group (container) (typed FeaturePython)
  n = 0.155
FEATURE [App::DocumentObjectGroupPython] N_element011  label="N_element : 0.042"  # scripted group (container) (typed FeaturePython)
  n = 0.042
FEATURE [App::DocumentObjectGroupPython] O_element015  label="O_element : 0.435"  # scripted group (container) (typed FeaturePython)
  n = 0.435
FEATURE [App::DocumentObjectGroupPython] Na_element003  label="Na_element : 0.003"  # scripted group (container) (typed FeaturePython)
  n = 0.001
FEATURE [App::DocumentObjectGroupPython] Mg_element002  label="Mg_element : 0.003"  # scripted group (container) (typed FeaturePython)
  n = 0.002
FEATURE [App::DocumentObjectGroupPython] P_element003  label="P_element : 0.103"  # scripted group (container) (typed FeaturePython)
  n = 0.103
FEATURE [App::DocumentObjectGroupPython] S_element005  label="S_element : 0.004"  # scripted group (container) (typed FeaturePython)
  n = 0.003
FEATURE [App::DocumentObjectGroupPython] Ca_element004  label="Ca_element : 0.225"  # scripted group (container) (typed FeaturePython)
  n = 0.225
FEATURE [App::DocumentObjectGroupPython] G4_BONE_CORTICAL_ICRP  # scripted group (container) (typed FeaturePython)
  Dunit = g/cm3
  Dvalue = 1.92
  Group = -> [H_element016,C_element016,N_element011,O_element015,Na_element003,Mg_element002,P_element003,S_element005,Ca_element004]
  conduct = 2
  density = 1
  expand = 3
  formula = G4_BONE_CORTICAL_ICRP
  name = G4_BONE_CORTICAL_ICRP
  specific = 4
FEATURE [App::DocumentObjectGroupPython] B_element001  label="B_element : 4"  # scripted group (container) (typed FeaturePython)
  n = 4
  ref = B_element
FEATURE [App::DocumentObjectGroupPython] C_element017  label="C_element : 1"  # scripted group (container) (typed FeaturePython)
  n = 1
  ref = C_element
FEATURE [App::DocumentObjectGroupPython] G4_BORON_CARBIDE  # scripted group (container) (typed FeaturePython)
  Dunit = g/cm3
  Dvalue = 2.52
  Group = -> [B_element001,C_element017]
  conduct = 2
  density = 1
  expand = 3
  formula = G4_BORON_CARBIDE
  name = G4_BORON_CARBIDE
  specific = 4
FEATURE [App::DocumentObjectGroupPython] B_element002  label="B_element : 2"  # scripted group (container) (typed FeaturePython)
  n = 2
  ref = B_element
FEATURE [App::DocumentObjectGroupPython] O_element016  label="O_element : 006"  # scripted group (container) (typed FeaturePython)
  n = 3
  ref = O_element
FEATURE [App::DocumentObjectGroupPython] G4_BORON_OXIDE  # scripted group (container) (typed FeaturePython)
  Dunit = g/cm3
  Dvalue = 1.812
  Group = -> [B_element002,O_element016]
  conduct = 2
  density = 1
  expand = 3
  formula = G4_BORON_OXIDE
  name = G4_BORON_OXIDE
  specific = 4
FEATURE [App::DocumentObjectGroupPython] H_element017  label="H_element : 0.107"  # scripted group (container) (typed FeaturePython)
  n = 0.107
FEATURE [App::DocumentObjectGroupPython] C_element018  label="C_element : 0.145"  # scripted group (container) (typed FeaturePython)
  n = 0.145
FEATURE [App::DocumentObjectGroupPython] N_element012  label="N_element : 0.022"  # scripted group (container) (typed FeaturePython)
  n = 0.022
FEATURE [App::DocumentObjectGroupPython] O_element017  label="O_element : 0.712"  # scripted group (container) (typed FeaturePython)
  n = 0.712
FEATURE [App::DocumentObjectGroupPython] Na_element004  label="Na_element : 0.004"  # scripted group (container) (typed FeaturePython)
  n = 0.002
FEATURE [App::DocumentObjectGroupPython] P_element004  label="P_element : 0.004"  # scripted group (container) (typed FeaturePython)
  n = 0.004
FEATURE [App::DocumentObjectGroupPython] S_element006  label="S_element : 0.005"  # scripted group (container) (typed FeaturePython)
  n = 0.002
FEATURE [App::DocumentObjectGroupPython] Cl_element003  label="Cl_element : 0.004"  # scripted group (container) (typed FeaturePython)
  n = 0.003
FEATURE [App::DocumentObjectGroupPython] K_element002  label="K_element : 0.003"  # scripted group (container) (typed FeaturePython)
  n = 0.003
FEATURE [App::DocumentObjectGroupPython] G4_BRAIN_ICRP  # scripted group (container) (typed FeaturePython)
  Dunit = g/cm3
  Dvalue = 1.04
  Group = -> [H_element017,C_element018,N_element012,O_element017,Na_element004,P_element004,S_element006,Cl_element003,K_element002]
  conduct = 2
  density = 1
  expand = 3
  formula = G4_BRAIN_ICRP
  name = G4_BRAIN_ICRP
  specific = 4
FEATURE [App::DocumentObjectGroupPython] C_element019  label="C_element : 4"  # scripted group (container) (typed FeaturePython)
  n = 4
  ref = C_element
FEATURE [App::DocumentObjectGroupPython] H_element018  label="H_element : 010"  # scripted group (container) (typed FeaturePython)
  n = 10
  ref = H_element
FEATURE [App::DocumentObjectGroupPython] G4_BUTANE  # scripted group (container) (typed FeaturePython)
  Dunit = g/cm3
  Dvalue = 0.00249343
  Group = -> [C_element019,H_element018]
  conduct = 2
  density = 1
  expand = 3
  formula = G4_BUTANE
  name = G4_BUTANE
  specific = 4
FEATURE [App::DocumentObjectGroupPython] C_element020  label="C_element : 008"  # scripted group (container) (typed FeaturePython)
  n = 4
  ref = C_element
FEATURE [App::DocumentObjectGroupPython] H_element019  label="H_element : 011"  # scripted group (container) (typed FeaturePython)
  n = 10
  ref = H_element
FEATURE [App::DocumentObjectGroupPython] O_element018  label="O_element : 007"  # scripted group (container) (typed FeaturePython)
  n = 1
  ref = O_element
FEATURE [App::DocumentObjectGroupPython] G4_N_BUTYL_ALCOHOL  label="G4_N-BUTYL_ALCOHOL"  # scripted group (container) (typed FeaturePython)
  Dunit = g/cm3
  Dvalue = 0.8098
  Group = -> [C_element020,H_element019,O_element018]
  conduct = 2
  density = 1
  expand = 3
  formula = G4_N-BUTYL_ALCOHOL
  name = G4_N-BUTYL_ALCOHOL
  specific = 4
FEATURE [App::DocumentObjectGroupPython] H_element020  label="H_element : 0.025"  # scripted group (container) (typed FeaturePython)
  n = 0.02468
FEATURE [App::DocumentObjectGroupPython] C_element021  label="C_element : 0.502"  # scripted group (container) (typed FeaturePython)
  n = 0.501611
FEATURE [App::DocumentObjectGroupPython] O_element019  label="O_element : 0.005"  # scripted group (container) (typed FeaturePython)
  n = 0.004527
FEATURE [App::DocumentObjectGroupPython] F_element004  label="F_element : 0.465"  # scripted group (container) (typed FeaturePython)
  n = 0.465209
FEATURE [App::DocumentObjectGroupPython] Si_element001  label="Si_element : 0.004"  # scripted group (container) (typed FeaturePython)
  n = 0.003973
FEATURE [App::DocumentObjectGroupPython] G4_C_552  label="G4_C-552"  # scripted group (container) (typed FeaturePython)
  Dunit = g/cm3
  Dvalue = 1.76
  Group = -> [H_element020,C_element021,O_element019,F_element004,Si_element001]
  conduct = 2
  density = 1
  expand = 3
  formula = G4_C-552
  name = G4_C-552
  specific = 4
FEATURE [App::DocumentObjectGroupPython] Cd_element001  label="Cd_element : 1"  # scripted group (container) (typed FeaturePython)
  n = 1
  ref = Cd_element
FEATURE [App::DocumentObjectGroupPython] Te_element001  label="Te_element : 1"  # scripted group (container) (typed FeaturePython)
  n = 1
  ref = Te_element
FEATURE [App::DocumentObjectGroupPython] G4_CADMIUM_TELLURIDE  # scripted group (container) (typed FeaturePython)
  Dunit = g/cm3
  Dvalue = 6.2
  Group = -> [Cd_element001,Te_element001]
  conduct = 2
  density = 1
  expand = 3
  formula = G4_CADMIUM_TELLURIDE
  name = G4_CADMIUM_TELLURIDE
  specific = 4
FEATURE [App::DocumentObjectGroupPython] Cd_element002  label="Cd_element : 002"  # scripted group (container) (typed FeaturePython)
  n = 1
  ref = Cd_element
FEATURE [App::DocumentObjectGroupPython] W_element001  label="W_element : 1"  # scripted group (container) (typed FeaturePython)
  n = 1
  ref = W_element
FEATURE [App::DocumentObjectGroupPython] O_element020  label="O_element : 008"  # scripted group (container) (typed FeaturePython)
  n = 4
  ref = O_element
FEATURE [App::DocumentObjectGroupPython] G4_CADMIUM_TUNGSTATE  # scripted group (container) (typed FeaturePython)
  Dunit = g/cm3
  Dvalue = 7.9
  Group = -> [Cd_element002,W_element001,O_element020]
  conduct = 2
  density = 1
  expand = 3
  formula = G4_CADMIUM_TUNGSTATE
  name = G4_CADMIUM_TUNGSTATE
  specific = 4
FEATURE [App::DocumentObjectGroupPython] Ca_element005  label="Ca_element : 1"  # scripted group (container) (typed FeaturePython)
  n = 1
  ref = Ca_element
FEATURE [App::DocumentObjectGroupPython] C_element022  label="C_element : 009"  # scripted group (container) (typed FeaturePython)
  n = 1
  ref = C_element
FEATURE [App::DocumentObjectGroupPython] O_element021  label="O_element : 009"  # scripted group (container) (typed FeaturePython)
  n = 3
  ref = O_element
FEATURE [App::DocumentObjectGroupPython] G4_CALCIUM_CARBONATE  # scripted group (container) (typed FeaturePython)
  Dunit = g/cm3
  Dvalue = 2.8
  Group = -> [Ca_element005,C_element022,O_element021]
  conduct = 2
  density = 1
  expand = 3
  formula = G4_CALCIUM_CARBONATE
  name = G4_CALCIUM_CARBONATE
  specific = 4
FEATURE [App::DocumentObjectGroupPython] Ca_element006  label="Ca_element : 002"  # scripted group (container) (typed FeaturePython)
  n = 1
  ref = Ca_element
FEATURE [App::DocumentObjectGroupPython] F_element005  label="F_element : 003"  # scripted group (container) (typed FeaturePython)
  n = 2
  ref = F_element
FEATURE [App::DocumentObjectGroupPython] G4_CALCIUM_FLUORIDE  # scripted group (container) (typed FeaturePython)
  Dunit = g/cm3
  Dvalue = 3.18
  Group = -> [Ca_element006,F_element005]
  conduct = 2
  density = 1
  expand = 3
  formula = G4_CALCIUM_FLUORIDE
  name = G4_CALCIUM_FLUORIDE
  specific = 4
FEATURE [App::DocumentObjectGroupPython] Ca_element007  label="Ca_element : 003"  # scripted group (container) (typed FeaturePython)
  n = 1
  ref = Ca_element
FEATURE [App::DocumentObjectGroupPython] O_element022  label="O_element : 010"  # scripted group (container) (typed FeaturePython)
  n = 1
  ref = O_element
FEATURE [App::DocumentObjectGroupPython] G4_CALCIUM_OXIDE  # scripted group (container) (typed FeaturePython)
  Dunit = g/cm3
  Dvalue = 3.3
  Group = -> [Ca_element007,O_element022]
  conduct = 2
  density = 1
  expand = 3
  formula = G4_CALCIUM_OXIDE
  name = G4_CALCIUM_OXIDE
  specific = 4
FEATURE [App::DocumentObjectGroupPython] Ca_element008  label="Ca_element : 004"  # scripted group (container) (typed FeaturePython)
  n = 1
  ref = Ca_element
FEATURE [App::DocumentObjectGroupPython] S_element007  label="S_element : 002"  # scripted group (container) (typed FeaturePython)
  n = 1
  ref = S_element
FEATURE [App::DocumentObjectGroupPython] O_element023  label="O_element : 011"  # scripted group (container) (typed FeaturePython)
  n = 4
  ref = O_element
FEATURE [App::DocumentObjectGroupPython] G4_CALCIUM_SULFATE  # scripted group (container) (typed FeaturePython)
  Dunit = g/cm3
  Dvalue = 2.96
  Group = -> [Ca_element008,S_element007,O_element023]
  conduct = 2
  density = 1
  expand = 3
  formula = G4_CALCIUM_SULFATE
  name = G4_CALCIUM_SULFATE
  specific = 4
FEATURE [App::DocumentObjectGroupPython] Ca_element009  label="Ca_element : 005"  # scripted group (container) (typed FeaturePython)
  n = 1
  ref = Ca_element
FEATURE [App::DocumentObjectGroupPython] W_element002  label="W_element : 002"  # scripted group (container) (typed FeaturePython)
  n = 1
  ref = W_element
FEATURE [App::DocumentObjectGroupPython] O_element024  label="O_element : 012"  # scripted group (container) (typed FeaturePython)
  n = 4
  ref = O_element
FEATURE [App::DocumentObjectGroupPython] G4_CALCIUM_TUNGSTATE  # scripted group (container) (typed FeaturePython)
  Dunit = g/cm3
  Dvalue = 6.062
  Group = -> [Ca_element009,W_element002,O_element024]
  conduct = 2
  density = 1
  expand = 3
  formula = G4_CALCIUM_TUNGSTATE
  name = G4_CALCIUM_TUNGSTATE
  specific = 4
FEATURE [App::DocumentObjectGroupPython] C_element023  label="C_element : 010"  # scripted group (container) (typed FeaturePython)
  n = 1
  ref = C_element
FEATURE [App::DocumentObjectGroupPython] O_element025  label="O_element : 013"  # scripted group (container) (typed FeaturePython)
  n = 2
  ref = O_element
FEATURE [App::DocumentObjectGroupPython] G4_CARBON_DIOXIDE  # scripted group (container) (typed FeaturePython)
  Dunit = g/cm3
  Dvalue = 0.00184212
  Group = -> [C_element023,O_element025]
  conduct = 2
  density = 1
  expand = 3
  formula = G4_CARBON_DIOXIDE
  name = G4_CARBON_DIOXIDE
  specific = 4
FEATURE [App::DocumentObjectGroupPython] C_element024  label="C_element : 011"  # scripted group (container) (typed FeaturePython)
  n = 1
  ref = C_element
FEATURE [App::DocumentObjectGroupPython] Cl_element004  label="Cl_element : 4"  # scripted group (container) (typed FeaturePython)
  n = 4
  ref = Cl_element
FEATURE [App::DocumentObjectGroupPython] G4_CARBON_TETRACHLORIDE  # scripted group (container) (typed FeaturePython)
  Dunit = g/cm3
  Dvalue = 1.594
  Group = -> [C_element024,Cl_element004]
  conduct = 2
  density = 1
  expand = 3
  formula = G4_CARBON_TETRACHLORIDE
  name = G4_CARBON_TETRACHLORIDE
  specific = 4
FEATURE [App::DocumentObjectGroupPython] C_element025  label="C_element : 012"  # scripted group (container) (typed FeaturePython)
  n = 6
  ref = C_element
FEATURE [App::DocumentObjectGroupPython] H_element021  label="H_element : 012"  # scripted group (container) (typed FeaturePython)
  n = 10
  ref = H_element
FEATURE [App::DocumentObjectGroupPython] O_element026  label="O_element : 5"  # scripted group (container) (typed FeaturePython)
  n = 5
  ref = O_element
FEATURE [App::DocumentObjectGroupPython] G4_CELLULOSE_CELLOPHANE  # scripted group (container) (typed FeaturePython)
  Dunit = g/cm3
  Dvalue = 1.42
  Group = -> [C_element025,H_element021,O_element026]
  conduct = 2
  density = 1
  expand = 3
  formula = G4_CELLULOSE_CELLOPHANE
  name = G4_CELLULOSE_CELLOPHANE
  specific = 4
FEATURE [App::DocumentObjectGroupPython] H_element022  label="H_element : 0.067"  # scripted group (container) (typed FeaturePython)
  n = 0.067125
FEATURE [App::DocumentObjectGroupPython] C_element026  label="C_element : 0.545"  # scripted group (container) (typed FeaturePython)
  n = 0.545403
FEATURE [App::DocumentObjectGroupPython] O_element027  label="O_element : 0.387"  # scripted group (container) (typed FeaturePython)
  n = 0.387472
FEATURE [App::DocumentObjectGroupPython] G4_CELLULOSE_BUTYRATE  # scripted group (container) (typed FeaturePython)
  Dunit = g/cm3
  Dvalue = 1.2
  Group = -> [H_element022,C_element026,O_element027]
  conduct = 2
  density = 1
  expand = 3
  formula = G4_CELLULOSE_BUTYRATE
  name = G4_CELLULOSE_BUTYRATE
  specific = 4
FEATURE [App::DocumentObjectGroupPython] H_element023  label="H_element : 0.029"  # scripted group (container) (typed FeaturePython)
  n = 0.029216
FEATURE [App::DocumentObjectGroupPython] C_element027  label="C_element : 0.271"  # scripted group (container) (typed FeaturePython)
  n = 0.271296
FEATURE [App::DocumentObjectGroupPython] N_element013  label="N_element : 0.121"  # scripted group (container) (typed FeaturePython)
  n = 0.121276
FEATURE [App::DocumentObjectGroupPython] O_element028  label="O_element : 0.578"  # scripted group (container) (typed FeaturePython)
  n = 0.578212
FEATURE [App::DocumentObjectGroupPython] G4_CELLULOSE_NITRATE  # scripted group (container) (typed FeaturePython)
  Dunit = g/cm3
  Dvalue = 1.49
  Group = -> [H_element023,C_element027,N_element013,O_element028]
  conduct = 2
  density = 1
  expand = 3
  formula = G4_CELLULOSE_NITRATE
  name = G4_CELLULOSE_NITRATE
  specific = 4
FEATURE [App::DocumentObjectGroupPython] H_element024  label="H_element : 0.108"  # scripted group (container) (typed FeaturePython)
  n = 0.107596
FEATURE [App::DocumentObjectGroupPython] N_element014  label="N_element : 0.001"  # scripted group (container) (typed FeaturePython)
  n = 0.0008
FEATURE [App::DocumentObjectGroupPython] O_element029  label="O_element : 0.875"  # scripted group (container) (typed FeaturePython)
  n = 0.874976
FEATURE [App::DocumentObjectGroupPython] S_element008  label="S_element : 0.015"  # scripted group (container) (typed FeaturePython)
  n = 0.014627
FEATURE [App::DocumentObjectGroupPython] Ce_element001  label="Ce_element : 0.002"  # scripted group (container) (typed FeaturePython)
  n = 0.002001
FEATURE [App::DocumentObjectGroupPython] G4_CERIC_SULFATE  # scripted group (container) (typed FeaturePython)
  Dunit = g/cm3
  Dvalue = 1.03
  Group = -> [H_element024,N_element014,O_element029,S_element008,Ce_element001]
  conduct = 2
  density = 1
  expand = 3
  formula = G4_CERIC_SULFATE
  name = G4_CERIC_SULFATE
  specific = 4
FEATURE [App::DocumentObjectGroupPython] Cs_element001  label="Cs_element : 1"  # scripted group (container) (typed FeaturePython)
  n = 1
  ref = Cs_element
FEATURE [App::DocumentObjectGroupPython] F_element006  label="F_element : 1"  # scripted group (container) (typed FeaturePython)
  n = 1
  ref = F_element
FEATURE [App::DocumentObjectGroupPython] G4_CESIUM_FLUORIDE  # scripted group (container) (typed FeaturePython)
  Dunit = g/cm3
  Dvalue = 4.115
  Group = -> [Cs_element001,F_element006]
  conduct = 2
  density = 1
  expand = 3
  formula = G4_CESIUM_FLUORIDE
  name = G4_CESIUM_FLUORIDE
  specific = 4
FEATURE [App::DocumentObjectGroupPython] Cs_element002  label="Cs_element : 002"  # scripted group (container) (typed FeaturePython)
  n = 1
  ref = Cs_element
FEATURE [App::DocumentObjectGroupPython] I_element001  label="I_element : 1"  # scripted group (container) (typed FeaturePython)
  n = 1
  ref = I_element
FEATURE [App::DocumentObjectGroupPython] G4_CESIUM_IODIDE  # scripted group (container) (typed FeaturePython)
  Dunit = g/cm3
  Dvalue = 4.51
  Group = -> [Cs_element002,I_element001]
  conduct = 2
  density = 1
  expand = 3
  formula = G4_CESIUM_IODIDE
  name = G4_CESIUM_IODIDE
  specific = 4
FEATURE [App::DocumentObjectGroupPython] C_element028  label="C_element : 013"  # scripted group (container) (typed FeaturePython)
  n = 6
  ref = C_element
FEATURE [App::DocumentObjectGroupPython] H_element025  label="H_element : 013"  # scripted group (container) (typed FeaturePython)
  n = 5
  ref = H_element
FEATURE [App::DocumentObjectGroupPython] Cl_element005  label="Cl_element : 1"  # scripted group (container) (typed FeaturePython)
  n = 1
  ref = Cl_element
FEATURE [App::DocumentObjectGroupPython] G4_CHLOROBENZENE  # scripted group (container) (typed FeaturePython)
  Dunit = g/cm3
  Dvalue = 1.1058
  Group = -> [C_element028,H_element025,Cl_element005]
  conduct = 2
  density = 1
  expand = 3
  formula = G4_CHLOROBENZENE
  name = G4_CHLOROBENZENE
  specific = 4
FEATURE [App::DocumentObjectGroupPython] C_element029  label="C_element : 014"  # scripted group (container) (typed FeaturePython)
  n = 1
  ref = C_element
FEATURE [App::DocumentObjectGroupPython] H_element026  label="H_element : 1"  # scripted group (container) (typed FeaturePython)
  n = 1
  ref = H_element
FEATURE [App::DocumentObjectGroupPython] Cl_element006  label="Cl_element : 3"  # scripted group (container) (typed FeaturePython)
  n = 3
  ref = Cl_element
FEATURE [App::DocumentObjectGroupPython] G4_CHLOROFORM  # scripted group (container) (typed FeaturePython)
  Dunit = g/cm3
  Dvalue = 1.4832
  Group = -> [C_element029,H_element026,Cl_element006]
  conduct = 2
  density = 1
  expand = 3
  formula = G4_CHLOROFORM
  name = G4_CHLOROFORM
  specific = 4
FEATURE [App::DocumentObjectGroupPython] H_element027  label="H_element : 0.010"  # scripted group (container) (typed FeaturePython)
  n = 0.01
FEATURE [App::DocumentObjectGroupPython] C_element030  label="C_element : 0.001"  # scripted group (container) (typed FeaturePython)
  n = 0.001
FEATURE [App::DocumentObjectGroupPython] O_element030  label="O_element : 0.529"  # scripted group (container) (typed FeaturePython)
  n = 0.529107
FEATURE [App::DocumentObjectGroupPython] Na_element005  label="Na_element : 0.016"  # scripted group (container) (typed FeaturePython)
  n = 0.016
FEATURE [App::DocumentObjectGroupPython] Mg_element003  label="Mg_element : 0.004"  # scripted group (container) (typed FeaturePython)
  n = 0.002
FEATURE [App::DocumentObjectGroupPython] Al_element002  label="Al_element : 0.034"  # scripted group (container) (typed FeaturePython)
  n = 0.033872
FEATURE [App::DocumentObjectGroupPython] Si_element002  label="Si_element : 0.337"  # scripted group (container) (typed FeaturePython)
  n = 0.337021
FEATURE [App::DocumentObjectGroupPython] K_element003  label="K_element : 0.013"  # scripted group (container) (typed FeaturePython)
  n = 0.013
FEATURE [App::DocumentObjectGroupPython] Ca_element010  label="Ca_element : 0.044"  # scripted group (container) (typed FeaturePython)
  n = 0.044
FEATURE [App::DocumentObjectGroupPython] Fe_element002  label="Fe_element : 0.014"  # scripted group (container) (typed FeaturePython)
  n = 0.014
FEATURE [App::DocumentObjectGroupPython] G4_CONCRETE  # scripted group (container) (typed FeaturePython)
  Dunit = g/cm3
  Dvalue = 2.3
  Group = -> [H_element027,C_element030,O_element030,Na_element005,Mg_element003,Al_element002,Si_element002,K_element003,Ca_element010,Fe_element002]
  conduct = 2
  density = 1
  expand = 3
  formula = G4_CONCRETE
  name = G4_CONCRETE
  specific = 4
FEATURE [App::DocumentObjectGroupPython] C_element031  label="C_element : 015"  # scripted group (container) (typed FeaturePython)
  n = 6
  ref = C_element
FEATURE [App::DocumentObjectGroupPython] H_element028  label="H_element : 12"  # scripted group (container) (typed FeaturePython)
  n = 12
  ref = H_element
FEATURE [App::DocumentObjectGroupPython] G4_CYCLOHEXANE  # scripted group (container) (typed FeaturePython)
  Dunit = g/cm3
  Dvalue = 0.779
  Group = -> [C_element031,H_element028]
  conduct = 2
  density = 1
  expand = 3
  formula = G4_CYCLOHEXANE
  name = G4_CYCLOHEXANE
  specific = 4
FEATURE [App::DocumentObjectGroupPython] C_element032  label="C_element : 016"  # scripted group (container) (typed FeaturePython)
  n = 6
  ref = C_element
FEATURE [App::DocumentObjectGroupPython] H_element029  label="H_element : 4"  # scripted group (container) (typed FeaturePython)
  n = 4
  ref = H_element
FEATURE [App::DocumentObjectGroupPython] Cl_element007  label="Cl_element : 2"  # scripted group (container) (typed FeaturePython)
  n = 2
  ref = Cl_element
FEATURE [App::DocumentObjectGroupPython] G4_1_2_DICHLOROBENZENE  label="G4_1.2-DICHLOROBENZENE"  # scripted group (container) (typed FeaturePython)
  Dunit = g/cm3
  Dvalue = 1.3048
  Group = -> [C_element032,H_element029,Cl_element007]
  conduct = 2
  density = 1
  expand = 3
  formula = G4_1.2-DICHLOROBENZENE
  name = G4_1.2-DICHLOROBENZENE
  specific = 4
FEATURE [App::DocumentObjectGroupPython] C_element033  label="C_element : 017"  # scripted group (container) (typed FeaturePython)
  n = 4
  ref = C_element
FEATURE [App::DocumentObjectGroupPython] H_element030  label="H_element : 8"  # scripted group (container) (typed FeaturePython)
  n = 8
  ref = H_element
FEATURE [App::DocumentObjectGroupPython] O_element031  label="O_element : 014"  # scripted group (container) (typed FeaturePython)
  n = 1
  ref = O_element
FEATURE [App::DocumentObjectGroupPython] Cl_element008  label="Cl_element : 005"  # scripted group (container) (typed FeaturePython)
  n = 2
  ref = Cl_element
FEATURE [App::DocumentObjectGroupPython] G4_DICHLORODIETHYL_ETHER  # scripted group (container) (typed FeaturePython)
  Dunit = g/cm3
  Dvalue = 1.2199
  Group = -> [C_element033,H_element030,O_element031,Cl_element008]
  conduct = 2
  density = 1
  expand = 3
  formula = G4_DICHLORODIETHYL_ETHER
  name = G4_DICHLORODIETHYL_ETHER
  specific = 4
FEATURE [App::DocumentObjectGroupPython] C_element034  label="C_element : 018"  # scripted group (container) (typed FeaturePython)
  n = 2
  ref = C_element
FEATURE [App::DocumentObjectGroupPython] H_element031  label="H_element : 014"  # scripted group (container) (typed FeaturePython)
  n = 4
  ref = H_element
FEATURE [App::DocumentObjectGroupPython] Cl_element009  label="Cl_element : 006"  # scripted group (container) (typed FeaturePython)
  n = 2
  ref = Cl_element
FEATURE [App::DocumentObjectGroupPython] G4_1_2_DICHLOROETHANE  label="G4_1.2-DICHLOROETHANE"  # scripted group (container) (typed FeaturePython)
  Dunit = g/cm3
  Dvalue = 1.2351
  Group = -> [C_element034,H_element031,Cl_element009]
  conduct = 2
  density = 1
  expand = 3
  formula = G4_1.2-DICHLOROETHANE
  name = G4_1.2-DICHLOROETHANE
  specific = 4
FEATURE [App::DocumentObjectGroupPython] C_element035  label="C_element : 019"  # scripted group (container) (typed FeaturePython)
  n = 4
  ref = C_element
FEATURE [App::DocumentObjectGroupPython] H_element032  label="H_element : 015"  # scripted group (container) (typed FeaturePython)
  n = 10
  ref = H_element
FEATURE [App::DocumentObjectGroupPython] O_element032  label="O_element : 015"  # scripted group (container) (typed FeaturePython)
  n = 1
  ref = O_element
FEATURE [App::DocumentObjectGroupPython] G4_DIETHYL_ETHER  # scripted group (container) (typed FeaturePython)
  Dunit = g/cm3
  Dvalue = 0.71378
  Group = -> [C_element035,H_element032,O_element032]
  conduct = 2
  density = 1
  expand = 3
  formula = G4_DIETHYL_ETHER
  name = G4_DIETHYL_ETHER
  specific = 4
FEATURE [App::DocumentObjectGroupPython] C_element036  label="C_element : 020"  # scripted group (container) (typed FeaturePython)
  n = 3
  ref = C_element
FEATURE [App::DocumentObjectGroupPython] H_element033  label="H_element : 016"  # scripted group (container) (typed FeaturePython)
  n = 7
  ref = H_element
FEATURE [App::DocumentObjectGroupPython] N_element015  label="N_element : 008"  # scripted group (container) (typed FeaturePython)
  n = 1
  ref = N_element
FEATURE [App::DocumentObjectGroupPython] O_element033  label="O_element : 016"  # scripted group (container) (typed FeaturePython)
  n = 1
  ref = O_element
FEATURE [App::DocumentObjectGroupPython] G4_N_N_DIMETHYL_FORMAMIDE  label="G4_N.N-DIMETHYL_FORMAMIDE"  # scripted group (container) (typed FeaturePython)
  Dunit = g/cm3
  Dvalue = 0.9487
  Group = -> [C_element036,H_element033,N_element015,O_element033]
  conduct = 2
  density = 1
  expand = 3
  formula = G4_N.N-DIMETHYL_FORMAMIDE
  name = G4_N.N-DIMETHYL_FORMAMIDE
  specific = 4
FEATURE [App::DocumentObjectGroupPython] C_element037  label="C_element : 021"  # scripted group (container) (typed FeaturePython)
  n = 2
  ref = C_element
FEATURE [App::DocumentObjectGroupPython] H_element034  label="H_element : 017"  # scripted group (container) (typed FeaturePython)
  n = 6
  ref = H_element
FEATURE [App::DocumentObjectGroupPython] O_element034  label="O_element : 017"  # scripted group (container) (typed FeaturePython)
  n = 1
  ref = O_element
FEATURE [App::DocumentObjectGroupPython] S_element009  label="S_element : 003"  # scripted group (container) (typed FeaturePython)
  n = 1
  ref = S_element
FEATURE [App::DocumentObjectGroupPython] G4_DIMETHYL_SULFOXIDE  # scripted group (container) (typed FeaturePython)
  Dunit = g/cm3
  Dvalue = 1.1014
  Group = -> [C_element037,H_element034,O_element034,S_element009]
  conduct = 2
  density = 1
  expand = 3
  formula = G4_DIMETHYL_SULFOXIDE
  name = G4_DIMETHYL_SULFOXIDE
  specific = 4
FEATURE [App::DocumentObjectGroupPython] C_element038  label="C_element : 022"  # scripted group (container) (typed FeaturePython)
  n = 2
  ref = C_element
FEATURE [App::DocumentObjectGroupPython] H_element035  label="H_element : 018"  # scripted group (container) (typed FeaturePython)
  n = 6
  ref = H_element
FEATURE [App::DocumentObjectGroupPython] G4_ETHANE  # scripted group (container) (typed FeaturePython)
  Dunit = g/cm3
  Dvalue = 0.00125324
  Group = -> [C_element038,H_element035]
  conduct = 2
  density = 1
  expand = 3
  formula = G4_ETHANE
  name = G4_ETHANE
  specific = 4
FEATURE [App::DocumentObjectGroupPython] C_element039  label="C_element : 023"  # scripted group (container) (typed FeaturePython)
  n = 2
  ref = C_element
FEATURE [App::DocumentObjectGroupPython] H_element036  label="H_element : 019"  # scripted group (container) (typed FeaturePython)
  n = 6
  ref = H_element
FEATURE [App::DocumentObjectGroupPython] O_element035  label="O_element : 018"  # scripted group (container) (typed FeaturePython)
  n = 1
  ref = O_element
FEATURE [App::DocumentObjectGroupPython] G4_ETHYL_ALCOHOL  # scripted group (container) (typed FeaturePython)
  Dunit = g/cm3
  Dvalue = 0.7893
  Group = -> [C_element039,H_element036,O_element035]
  conduct = 2
  density = 1
  expand = 3
  formula = G4_ETHYL_ALCOHOL
  name = G4_ETHYL_ALCOHOL
  specific = 4
FEATURE [App::DocumentObjectGroupPython] H_element037  label="H_element : 0.090"  # scripted group (container) (typed FeaturePython)
  n = 0.090027
FEATURE [App::DocumentObjectGroupPython] C_element040  label="C_element : 0.585"  # scripted group (container) (typed FeaturePython)
  n = 0.585182
FEATURE [App::DocumentObjectGroupPython] O_element036  label="O_element : 0.325"  # scripted group (container) (typed FeaturePython)
  n = 0.324791
FEATURE [App::DocumentObjectGroupPython] G4_ETHYL_CELLULOSE  # scripted group (container) (typed FeaturePython)
  Dunit = g/cm3
  Dvalue = 1.13
  Group = -> [H_element037,C_element040,O_element036]
  conduct = 2
  density = 1
  expand = 3
  formula = G4_ETHYL_CELLULOSE
  name = G4_ETHYL_CELLULOSE
  specific = 4
FEATURE [App::DocumentObjectGroupPython] C_element041  label="C_element : 024"  # scripted group (container) (typed FeaturePython)
  n = 2
  ref = C_element
FEATURE [App::DocumentObjectGroupPython] H_element038  label="H_element : 020"  # scripted group (container) (typed FeaturePython)
  n = 4
  ref = H_element
FEATURE [App::DocumentObjectGroupPython] G4_ETHYLENE  # scripted group (container) (typed FeaturePython)
  Dunit = g/cm3
  Dvalue = 0.00117497
  Group = -> [C_element041,H_element038]
  conduct = 2
  density = 1
  expand = 3
  formula = G4_ETHYLENE
  name = G4_ETHYLENE
  specific = 4
FEATURE [App::DocumentObjectGroupPython] H_element039  label="H_element : 0.096"  # scripted group (container) (typed FeaturePython)
  n = 0.096
FEATURE [App::DocumentObjectGroupPython] C_element042  label="C_element : 0.195"  # scripted group (container) (typed FeaturePython)
  n = 0.195
FEATURE [App::DocumentObjectGroupPython] N_element016  label="N_element : 0.057"  # scripted group (container) (typed FeaturePython)
  n = 0.057
FEATURE [App::DocumentObjectGroupPython] O_element037  label="O_element : 0.646"  # scripted group (container) (typed FeaturePython)
  n = 0.646
FEATURE [App::DocumentObjectGroupPython] Na_element006  label="Na_element : 0.017"  # scripted group (container) (typed FeaturePython)
  n = 0.001
FEATURE [App::DocumentObjectGroupPython] P_element005  label="P_element : 0.104"  # scripted group (container) (typed FeaturePython)
  n = 0.001
FEATURE [App::DocumentObjectGroupPython] S_element010  label="S_element : 0.016"  # scripted group (container) (typed FeaturePython)
  n = 0.003
FEATURE [App::DocumentObjectGroupPython] Cl_element010  label="Cl_element : 0.005"  # scripted group (container) (typed FeaturePython)
  n = 0.001
FEATURE [App::DocumentObjectGroupPython] G4_EYE_LENS_ICRP  # scripted group (container) (typed FeaturePython)
  Dunit = g/cm3
  Dvalue = 1.07
  Group = -> [H_element039,C_element042,N_element016,O_element037,Na_element006,P_element005,S_element010,Cl_element010]
  conduct = 2
  density = 1
  expand = 3
  formula = G4_EYE_LENS_ICRP
  name = G4_EYE_LENS_ICRP
  specific = 4
FEATURE [App::DocumentObjectGroupPython] Fe_element003  label="Fe_element : 2"  # scripted group (container) (typed FeaturePython)
  n = 2
  ref = Fe_element
FEATURE [App::DocumentObjectGroupPython] O_element038  label="O_element : 019"  # scripted group (container) (typed FeaturePython)
  n = 3
  ref = O_element
FEATURE [App::DocumentObjectGroupPython] G4_FERRIC_OXIDE  # scripted group (container) (typed FeaturePython)
  Dunit = g/cm3
  Dvalue = 5.2
  Group = -> [Fe_element003,O_element038]
  conduct = 2
  density = 1
  expand = 3
  formula = G4_FERRIC_OXIDE
  name = G4_FERRIC_OXIDE
  specific = 4
FEATURE [App::DocumentObjectGroupPython] Fe_element004  label="Fe_element : 1"  # scripted group (container) (typed FeaturePython)
  n = 1
  ref = Fe_element
FEATURE [App::DocumentObjectGroupPython] B_element003  label="B_element : 1"  # scripted group (container) (typed FeaturePython)
  n = 1
  ref = B_element
FEATURE [App::DocumentObjectGroupPython] G4_FERROBORIDE  # scripted group (container) (typed FeaturePython)
  Dunit = g/cm3
  Dvalue = 7.15
  Group = -> [Fe_element004,B_element003]
  conduct = 2
  density = 1
  expand = 3
  formula = G4_FERROBORIDE
  name = G4_FERROBORIDE
  specific = 4
FEATURE [App::DocumentObjectGroupPython] Fe_element005  label="Fe_element : 003"  # scripted group (container) (typed FeaturePython)
  n = 1
  ref = Fe_element
FEATURE [App::DocumentObjectGroupPython] O_element039  label="O_element : 020"  # scripted group (container) (typed FeaturePython)
  n = 1
  ref = O_element
FEATURE [App::DocumentObjectGroupPython] G4_FERROUS_OXIDE  # scripted group (container) (typed FeaturePython)
  Dunit = g/cm3
  Dvalue = 5.7
  Group = -> [Fe_element005,O_element039]
  conduct = 2
  density = 1
  expand = 3
  formula = G4_FERROUS_OXIDE
  name = G4_FERROUS_OXIDE
  specific = 4
FEATURE [App::DocumentObjectGroupPython] H_element040  label="H_element : 0.115"  # scripted group (container) (typed FeaturePython)
  n = 0.108259
FEATURE [App::DocumentObjectGroupPython] N_element017  label="N_element : 0.000"  # scripted group (container) (typed FeaturePython)
  n = 2.7e-05
FEATURE [App::DocumentObjectGroupPython] O_element040  label="O_element : 0.879"  # scripted group (container) (typed FeaturePython)
  n = 0.878636
FEATURE [App::DocumentObjectGroupPython] Na_element007  label="Na_element : 0.000"  # scripted group (container) (typed FeaturePython)
  n = 2.2e-05
FEATURE [App::DocumentObjectGroupPython] S_element011  label="S_element : 0.013"  # scripted group (container) (typed FeaturePython)
  n = 0.012968
FEATURE [App::DocumentObjectGroupPython] Cl_element011  label="Cl_element : 0.000"  # scripted group (container) (typed FeaturePython)
  n = 3.4e-05
FEATURE [App::DocumentObjectGroupPython] Fe_element006  label="Fe_element : 0.000"  # scripted group (container) (typed FeaturePython)
  n = 5.4e-05
FEATURE [App::DocumentObjectGroupPython] G4_FERROUS_SULFATE  # scripted group (container) (typed FeaturePython)
  Dunit = g/cm3
  Dvalue = 1.024
  Group = -> [H_element040,N_element017,O_element040,Na_element007,S_element011,Cl_element011,Fe_element006]
  conduct = 2
  density = 1
  expand = 3
  formula = G4_FERROUS_SULFATE
  name = G4_FERROUS_SULFATE
  specific = 4
FEATURE [App::DocumentObjectGroupPython] C_element043  label="C_element : 0.099"  # scripted group (container) (typed FeaturePython)
  n = 0.099335
FEATURE [App::DocumentObjectGroupPython] F_element007  label="F_element : 0.314"  # scripted group (container) (typed FeaturePython)
  n = 0.314247
FEATURE [App::DocumentObjectGroupPython] Cl_element012  label="Cl_element : 0.586"  # scripted group (container) (typed FeaturePython)
  n = 0.586418
FEATURE [App::DocumentObjectGroupPython] G4_FREON_12  label="G4_FREON-12"  # scripted group (container) (typed FeaturePython)
  Dunit = g/cm3
  Dvalue = 1.12
  Group = -> [C_element043,F_element007,Cl_element012]
  conduct = 2
  density = 1
  expand = 3
  formula = G4_FREON-12
  name = G4_FREON-12
  specific = 4
FEATURE [App::DocumentObjectGroupPython] C_element044  label="C_element : 0.057"  # scripted group (container) (typed FeaturePython)
  n = 0.057245
FEATURE [App::DocumentObjectGroupPython] F_element008  label="F_element : 0.181"  # scripted group (container) (typed FeaturePython)
  n = 0.181096
FEATURE [App::DocumentObjectGroupPython] Br_element001  label="Br_element : 0.762"  # scripted group (container) (typed FeaturePython)
  n = 0.761659
FEATURE [App::DocumentObjectGroupPython] G4_FREON_12B2  label="G4_FREON-12B2"  # scripted group (container) (typed FeaturePython)
  Dunit = g/cm3
  Dvalue = 1.8
  Group = -> [C_element044,F_element008,Br_element001]
  conduct = 2
  density = 1
  expand = 3
  formula = G4_FREON-12B2
  name = G4_FREON-12B2
  specific = 4
FEATURE [App::DocumentObjectGroupPython] C_element045  label="C_element : 0.115"  # scripted group (container) (typed FeaturePython)
  n = 0.114983
FEATURE [App::DocumentObjectGroupPython] F_element009  label="F_element : 0.546"  # scripted group (container) (typed FeaturePython)
  n = 0.545621
FEATURE [App::DocumentObjectGroupPython] Cl_element013  label="Cl_element : 0.339"  # scripted group (container) (typed FeaturePython)
  n = 0.339396
FEATURE [App::DocumentObjectGroupPython] G4_FREON_13  label="G4_FREON-13"  # scripted group (container) (typed FeaturePython)
  Dunit = g/cm3
  Dvalue = 0.95
  Group = -> [C_element045,F_element009,Cl_element013]
  conduct = 2
  density = 1
  expand = 3
  formula = G4_FREON-13
  name = G4_FREON-13
  specific = 4
FEATURE [App::DocumentObjectGroupPython] C_element046  label="C_element : 025"  # scripted group (container) (typed FeaturePython)
  n = 1
  ref = C_element
FEATURE [App::DocumentObjectGroupPython] F_element010  label="F_element : 3"  # scripted group (container) (typed FeaturePython)
  n = 3
  ref = F_element
FEATURE [App::DocumentObjectGroupPython] Br_element002  label="Br_element : 1"  # scripted group (container) (typed FeaturePython)
  n = 1
  ref = Br_element
FEATURE [App::DocumentObjectGroupPython] G4_FREON_13B1  label="G4_FREON-13B1"  # scripted group (container) (typed FeaturePython)
  Dunit = g/cm3
  Dvalue = 1.5
  Group = -> [C_element046,F_element010,Br_element002]
  conduct = 2
  density = 1
  expand = 3
  formula = G4_FREON-13B1
  name = G4_FREON-13B1
  specific = 4
FEATURE [App::DocumentObjectGroupPython] C_element047  label="C_element : 0.061"  # scripted group (container) (typed FeaturePython)
  n = 0.061309
FEATURE [App::DocumentObjectGroupPython] F_element011  label="F_element : 0.291"  # scripted group (container) (typed FeaturePython)
  n = 0.290924
FEATURE [App::DocumentObjectGroupPython] I_element002  label="I_element : 0.648"  # scripted group (container) (typed FeaturePython)
  n = 0.647767
FEATURE [App::DocumentObjectGroupPython] G4_FREON_13I1  label="G4_FREON-13I1"  # scripted group (container) (typed FeaturePython)
  Dunit = g/cm3
  Dvalue = 1.8
  Group = -> [C_element047,F_element011,I_element002]
  conduct = 2
  density = 1
  expand = 3
  formula = G4_FREON-13I1
  name = G4_FREON-13I1
  specific = 4
FEATURE [App::DocumentObjectGroupPython] Gd_element001  label="Gd_element : 2"  # scripted group (container) (typed FeaturePython)
  n = 2
  ref = Gd_element
FEATURE [App::DocumentObjectGroupPython] O_element041  label="O_element : 021"  # scripted group (container) (typed FeaturePython)
  n = 2
  ref = O_element
FEATURE [App::DocumentObjectGroupPython] S_element012  label="S_element : 004"  # scripted group (container) (typed FeaturePython)
  n = 1
  ref = S_element
FEATURE [App::DocumentObjectGroupPython] G4_GADOLINIUM_OXYSULFIDE  # scripted group (container) (typed FeaturePython)
  Dunit = g/cm3
  Dvalue = 7.44
  Group = -> [Gd_element001,O_element041,S_element012]
  conduct = 2
  density = 1
  expand = 3
  formula = G4_GADOLINIUM_OXYSULFIDE
  name = G4_GADOLINIUM_OXYSULFIDE
  specific = 4
FEATURE [App::DocumentObjectGroupPython] Ga_element001  label="Ga_element : 1"  # scripted group (container) (typed FeaturePython)
  n = 1
  ref = Ga_element
FEATURE [App::DocumentObjectGroupPython] As_element001  label="As_element : 1"  # scripted group (container) (typed FeaturePython)
  n = 1
  ref = As_element
FEATURE [App::DocumentObjectGroupPython] G4_GALLIUM_ARSENIDE  # scripted group (container) (typed FeaturePython)
  Dunit = g/cm3
  Dvalue = 5.31
  Group = -> [Ga_element001,As_element001]
  conduct = 2
  density = 1
  expand = 3
  formula = G4_GALLIUM_ARSENIDE
  name = G4_GALLIUM_ARSENIDE
  specific = 4
FEATURE [App::DocumentObjectGroupPython] H_element041  label="H_element : 0.081"  # scripted group (container) (typed FeaturePython)
  n = 0.08118
FEATURE [App::DocumentObjectGroupPython] C_element048  label="C_element : 0.416"  # scripted group (container) (typed FeaturePython)
  n = 0.41606
FEATURE [App::DocumentObjectGroupPython] N_element018  label="N_element : 0.111"  # scripted group (container) (typed FeaturePython)
  n = 0.11124
FEATURE [App::DocumentObjectGroupPython] O_element042  label="O_element : 0.381"  # scripted group (container) (typed FeaturePython)
  n = 0.38064
FEATURE [App::DocumentObjectGroupPython] S_element013  label="S_element : 0.011"  # scripted group (container) (typed FeaturePython)
  n = 0.01088
FEATURE [App::DocumentObjectGroupPython] G4_GEL_PHOTO_EMULSION  # scripted group (container) (typed FeaturePython)
  Dunit = g/cm3
  Dvalue = 1.2914
  Group = -> [H_element041,C_element048,N_element018,O_element042,S_element013]
  conduct = 2
  density = 1
  expand = 3
  formula = G4_GEL_PHOTO_EMULSION
  name = G4_GEL_PHOTO_EMULSION
  specific = 4
FEATURE [App::DocumentObjectGroupPython] B_element004  label="B_element : 0.040"  # scripted group (container) (typed FeaturePython)
  n = 0.0400639
FEATURE [App::DocumentObjectGroupPython] O_element043  label="O_element : 0.540"  # scripted group (container) (typed FeaturePython)
  n = 0.539561
FEATURE [App::DocumentObjectGroupPython] Na_element008  label="Na_element : 0.028"  # scripted group (container) (typed FeaturePython)
  n = 0.0281909
FEATURE [App::DocumentObjectGroupPython] Al_element003  label="Al_element : 0.012"  # scripted group (container) (typed FeaturePython)
  n = 0.011644
FEATURE [App::DocumentObjectGroupPython] Si_element003  label="Si_element : 0.377"  # scripted group (container) (typed FeaturePython)
  n = 0.377219
FEATURE [App::DocumentObjectGroupPython] K_element004  label="K_element : 0.014"  # scripted group (container) (typed FeaturePython)
  n = 0.00332099
FEATURE [App::DocumentObjectGroupPython] G4_Pyrex_Glass  # scripted group (container) (typed FeaturePython)
  Dunit = g/cm3
  Dvalue = 2.23
  Group = -> [B_element004,O_element043,Na_element008,Al_element003,Si_element003,K_element004]
  conduct = 2
  density = 1
  expand = 3
  formula = G4_Pyrex_Glass
  name = G4_Pyrex_Glass
  specific = 4
FEATURE [App::DocumentObjectGroupPython] O_element044  label="O_element : 0.156"  # scripted group (container) (typed FeaturePython)
  n = 0.156453
FEATURE [App::DocumentObjectGroupPython] Si_element004  label="Si_element : 0.081"  # scripted group (container) (typed FeaturePython)
  n = 0.080866
FEATURE [App::DocumentObjectGroupPython] Ti_element001  label="Ti_element : 0.008"  # scripted group (container) (typed FeaturePython)
  n = 0.008092
FEATURE [App::DocumentObjectGroupPython] As_element002  label="As_element : 0.003"  # scripted group (container) (typed FeaturePython)
  n = 0.002651
FEATURE [App::DocumentObjectGroupPython] Pb_element001  label="Pb_element : 0.752"  # scripted group (container) (typed FeaturePython)
  n = 0.751938
FEATURE [App::DocumentObjectGroupPython] G4_GLASS_LEAD  # scripted group (container) (typed FeaturePython)
  Dunit = g/cm3
  Dvalue = 6.22
  Group = -> [O_element044,Si_element004,Ti_element001,As_element002,Pb_element001]
  conduct = 2
  density = 1
  expand = 3
  formula = G4_GLASS_LEAD
  name = G4_GLASS_LEAD
  specific = 4
FEATURE [App::DocumentObjectGroupPython] O_element045  label="O_element : 0.460"  # scripted group (container) (typed FeaturePython)
  n = 0.4598
FEATURE [App::DocumentObjectGroupPython] Na_element009  label="Na_element : 0.096"  # scripted group (container) (typed FeaturePython)
  n = 0.0964411
FEATURE [App::DocumentObjectGroupPython] Si_element005  label="Si_element : 0.378"  # scripted group (container) (typed FeaturePython)
  n = 0.336553
FEATURE [App::DocumentObjectGroupPython] Ca_element011  label="Ca_element : 0.107"  # scripted group (container) (typed FeaturePython)
  n = 0.107205
FEATURE [App::DocumentObjectGroupPython] G4_GLASS_PLATE  # scripted group (container) (typed FeaturePython)
  Dunit = g/cm3
  Dvalue = 2.4
  Group = -> [O_element045,Na_element009,Si_element005,Ca_element011]
  conduct = 2
  density = 1
  expand = 3
  formula = G4_GLASS_PLATE
  name = G4_GLASS_PLATE
  specific = 4
FEATURE [App::DocumentObjectGroupPython] C_element049  label="C_element : 026"  # scripted group (container) (typed FeaturePython)
  n = 5
  ref = C_element
FEATURE [App::DocumentObjectGroupPython] H_element042  label="H_element : 021"  # scripted group (container) (typed FeaturePython)
  n = 10
  ref = H_element
FEATURE [App::DocumentObjectGroupPython] N_element019  label="N_element : 2"  # scripted group (container) (typed FeaturePython)
  n = 2
  ref = N_element
FEATURE [App::DocumentObjectGroupPython] O_element046  label="O_element : 022"  # scripted group (container) (typed FeaturePython)
  n = 3
  ref = O_element
FEATURE [App::DocumentObjectGroupPython] G4_GLUTAMINE  # scripted group (container) (typed FeaturePython)
  Dunit = g/cm3
  Dvalue = 1.46
  Group = -> [C_element049,H_element042,N_element019,O_element046]
  conduct = 2
  density = 1
  expand = 3
  formula = G4_GLUTAMINE
  name = G4_GLUTAMINE
  specific = 4
FEATURE [App::DocumentObjectGroupPython] C_element050  label="C_element : 027"  # scripted group (container) (typed FeaturePython)
  n = 3
  ref = C_element
FEATURE [App::DocumentObjectGroupPython] H_element043  label="H_element : 022"  # scripted group (container) (typed FeaturePython)
  n = 8
  ref = H_element
FEATURE [App::DocumentObjectGroupPython] O_element047  label="O_element : 023"  # scripted group (container) (typed FeaturePython)
  n = 3
  ref = O_element
FEATURE [App::DocumentObjectGroupPython] G4_GLYCEROL  # scripted group (container) (typed FeaturePython)
  Dunit = g/cm3
  Dvalue = 1.2613
  Group = -> [C_element050,H_element043,O_element047]
  conduct = 2
  density = 1
  expand = 3
  formula = G4_GLYCEROL
  name = G4_GLYCEROL
  specific = 4
FEATURE [App::DocumentObjectGroupPython] C_element051  label="C_element : 028"  # scripted group (container) (typed FeaturePython)
  n = 5
  ref = C_element
FEATURE [App::DocumentObjectGroupPython] H_element044  label="H_element : 023"  # scripted group (container) (typed FeaturePython)
  n = 5
  ref = H_element
FEATURE [App::DocumentObjectGroupPython] N_element020  label="N_element : 009"  # scripted group (container) (typed FeaturePython)
  n = 5
  ref = N_element
FEATURE [App::DocumentObjectGroupPython] O_element048  label="O_element : 024"  # scripted group (container) (typed FeaturePython)
  n = 1
  ref = O_element
FEATURE [App::DocumentObjectGroupPython] G4_GUANINE  # scripted group (container) (typed FeaturePython)
  Dunit = g/cm3
  Dvalue = 2.2
  Group = -> [C_element051,H_element044,N_element020,O_element048]
  conduct = 2
  density = 1
  expand = 3
  formula = G4_GUANINE
  name = G4_GUANINE
  specific = 4
FEATURE [App::DocumentObjectGroupPython] Ca_element012  label="Ca_element : 006"  # scripted group (container) (typed FeaturePython)
  n = 1
  ref = Ca_element
FEATURE [App::DocumentObjectGroupPython] S_element014  label="S_element : 005"  # scripted group (container) (typed FeaturePython)
  n = 1
  ref = S_element
FEATURE [App::DocumentObjectGroupPython] O_element049  label="O_element : 6"  # scripted group (container) (typed FeaturePython)
  n = 6
  ref = O_element
FEATURE [App::DocumentObjectGroupPython] H_element045  label="H_element : 024"  # scripted group (container) (typed FeaturePython)
  n = 4
  ref = H_element
FEATURE [App::DocumentObjectGroupPython] G4_GYPSUM  # scripted group (container) (typed FeaturePython)
  Dunit = g/cm3
  Dvalue = 2.32
  Group = -> [Ca_element012,S_element014,O_element049,H_element045]
  conduct = 2
  density = 1
  expand = 3
  formula = G4_GYPSUM
  name = G4_GYPSUM
  specific = 4
FEATURE [App::DocumentObjectGroupPython] C_element052  label="C_element : 7"  # scripted group (container) (typed FeaturePython)
  n = 7
  ref = C_element
FEATURE [App::DocumentObjectGroupPython] H_element046  label="H_element : 16"  # scripted group (container) (typed FeaturePython)
  n = 16
  ref = H_element
FEATURE [App::DocumentObjectGroupPython] G4_N_HEPTANE  label="G4_N-HEPTANE"  # scripted group (container) (typed FeaturePython)
  Dunit = g/cm3
  Dvalue = 0.68376
  Group = -> [C_element052,H_element046]
  conduct = 2
  density = 1
  expand = 3
  formula = G4_N-HEPTANE
  name = G4_N-HEPTANE
  specific = 4
FEATURE [App::DocumentObjectGroupPython] C_element053  label="C_element : 029"  # scripted group (container) (typed FeaturePython)
  n = 6
  ref = C_element
FEATURE [App::DocumentObjectGroupPython] H_element047  label="H_element : 14"  # scripted group (container) (typed FeaturePython)
  n = 14
  ref = H_element
FEATURE [App::DocumentObjectGroupPython] G4_N_HEXANE  label="G4_N-HEXANE"  # scripted group (container) (typed FeaturePython)
  Dunit = g/cm3
  Dvalue = 0.6603
  Group = -> [C_element053,H_element047]
  conduct = 2
  density = 1
  expand = 3
  formula = G4_N-HEXANE
  name = G4_N-HEXANE
  specific = 4
FEATURE [App::DocumentObjectGroupPython] C_element054  label="C_element : 22"  # scripted group (container) (typed FeaturePython)
  n = 22
  ref = C_element
FEATURE [App::DocumentObjectGroupPython] H_element048  label="H_element : 025"  # scripted group (container) (typed FeaturePython)
  n = 10
  ref = H_element
FEATURE [App::DocumentObjectGroupPython] N_element021  label="N_element : 010"  # scripted group (container) (typed FeaturePython)
  n = 2
  ref = N_element
FEATURE [App::DocumentObjectGroupPython] O_element050  label="O_element : 025"  # scripted group (container) (typed FeaturePython)
  n = 5
  ref = O_element
FEATURE [App::DocumentObjectGroupPython] G4_KAPTON  # scripted group (container) (typed FeaturePython)
  Dunit = g/cm3
  Dvalue = 1.42
  Group = -> [C_element054,H_element048,N_element021,O_element050]
  conduct = 2
  density = 1
  expand = 3
  formula = G4_KAPTON
  name = G4_KAPTON
  specific = 4
FEATURE [App::DocumentObjectGroupPython] La_element001  label="La_element : 1"  # scripted group (container) (typed FeaturePython)
  n = 1
  ref = La_element
FEATURE [App::DocumentObjectGroupPython] Br_element003  label="Br_element : 002"  # scripted group (container) (typed FeaturePython)
  n = 1
  ref = Br_element
FEATURE [App::DocumentObjectGroupPython] O_element051  label="O_element : 026"  # scripted group (container) (typed FeaturePython)
  n = 1
  ref = O_element
FEATURE [App::DocumentObjectGroupPython] G4_LANTHANUM_OXYBROMIDE  # scripted group (container) (typed FeaturePython)
  Dunit = g/cm3
  Dvalue = 6.28
  Group = -> [La_element001,Br_element003,O_element051]
  conduct = 2
  density = 1
  expand = 3
  formula = G4_LANTHANUM_OXYBROMIDE
  name = G4_LANTHANUM_OXYBROMIDE
  specific = 4
FEATURE [App::DocumentObjectGroupPython] La_element002  label="La_element : 2"  # scripted group (container) (typed FeaturePython)
  n = 2
  ref = La_element
FEATURE [App::DocumentObjectGroupPython] O_element052  label="O_element : 027"  # scripted group (container) (typed FeaturePython)
  n = 2
  ref = O_element
FEATURE [App::DocumentObjectGroupPython] S_element015  label="S_element : 006"  # scripted group (container) (typed FeaturePython)
  n = 1
  ref = S_element
FEATURE [App::DocumentObjectGroupPython] G4_LANTHANUM_OXYSULFIDE  # scripted group (container) (typed FeaturePython)
  Dunit = g/cm3
  Dvalue = 5.86
  Group = -> [La_element002,O_element052,S_element015]
  conduct = 2
  density = 1
  expand = 3
  formula = G4_LANTHANUM_OXYSULFIDE
  name = G4_LANTHANUM_OXYSULFIDE
  specific = 4
FEATURE [App::DocumentObjectGroupPython] O_element053  label="O_element : 0.072"  # scripted group (container) (typed FeaturePython)
  n = 0.071682
FEATURE [App::DocumentObjectGroupPython] Pb_element002  label="Pb_element : 0.928"  # scripted group (container) (typed FeaturePython)
  n = 0.928318
FEATURE [App::DocumentObjectGroupPython] G4_LEAD_OXIDE  # scripted group (container) (typed FeaturePython)
  Dunit = g/cm3
  Dvalue = 9.53
  Group = -> [O_element053,Pb_element002]
  conduct = 2
  density = 1
  expand = 3
  formula = G4_LEAD_OXIDE
  name = G4_LEAD_OXIDE
  specific = 4
FEATURE [App::DocumentObjectGroupPython] Li_element001  label="Li_element : 1"  # scripted group (container) (typed FeaturePython)
  n = 1
  ref = Li_element
FEATURE [App::DocumentObjectGroupPython] N_element022  label="N_element : 011"  # scripted group (container) (typed FeaturePython)
  n = 1
  ref = N_element
FEATURE [App::DocumentObjectGroupPython] H_element049  label="H_element : 026"  # scripted group (container) (typed FeaturePython)
  n = 2
  ref = H_element
FEATURE [App::DocumentObjectGroupPython] G4_LITHIUM_AMIDE  # scripted group (container) (typed FeaturePython)
  Dunit = g/cm3
  Dvalue = 1.178
  Group = -> [Li_element001,N_element022,H_element049]
  conduct = 2
  density = 1
  expand = 3
  formula = G4_LITHIUM_AMIDE
  name = G4_LITHIUM_AMIDE
  specific = 4
FEATURE [App::DocumentObjectGroupPython] Li_element002  label="Li_element : 2"  # scripted group (container) (typed FeaturePython)
  n = 2
  ref = Li_element
FEATURE [App::DocumentObjectGroupPython] C_element055  label="C_element : 030"  # scripted group (container) (typed FeaturePython)
  n = 1
  ref = C_element
FEATURE [App::DocumentObjectGroupPython] O_element054  label="O_element : 028"  # scripted group (container) (typed FeaturePython)
  n = 3
  ref = O_element
FEATURE [App::DocumentObjectGroupPython] G4_LITHIUM_CARBONATE  # scripted group (container) (typed FeaturePython)
  Dunit = g/cm3
  Dvalue = 2.11
  Group = -> [Li_element002,C_element055,O_element054]
  conduct = 2
  density = 1
  expand = 3
  formula = G4_LITHIUM_CARBONATE
  name = G4_LITHIUM_CARBONATE
  specific = 4
FEATURE [App::DocumentObjectGroupPython] Li_element003  label="Li_element : 003"  # scripted group (container) (typed FeaturePython)
  n = 1
  ref = Li_element
FEATURE [App::DocumentObjectGroupPython] F_element012  label="F_element : 004"  # scripted group (container) (typed FeaturePython)
  n = 1
  ref = F_element
FEATURE [App::DocumentObjectGroupPython] G4_LITHIUM_FLUORIDE  # scripted group (container) (typed FeaturePython)
  Dunit = g/cm3
  Dvalue = 2.635
  Group = -> [Li_element003,F_element012]
  conduct = 2
  density = 1
  expand = 3
  formula = G4_LITHIUM_FLUORIDE
  name = G4_LITHIUM_FLUORIDE
  specific = 4
FEATURE [App::DocumentObjectGroupPython] Li_element004  label="Li_element : 004"  # scripted group (container) (typed FeaturePython)
  n = 1
  ref = Li_element
FEATURE [App::DocumentObjectGroupPython] H_element050  label="H_element : 027"  # scripted group (container) (typed FeaturePython)
  n = 1
  ref = H_element
FEATURE [App::DocumentObjectGroupPython] G4_LITHIUM_HYDRIDE  # scripted group (container) (typed FeaturePython)
  Dunit = g/cm3
  Dvalue = 0.82
  Group = -> [Li_element004,H_element050]
  conduct = 2
  density = 1
  expand = 3
  formula = G4_LITHIUM_HYDRIDE
  name = G4_LITHIUM_HYDRIDE
  specific = 4
FEATURE [App::DocumentObjectGroupPython] Li_element005  label="Li_element : 005"  # scripted group (container) (typed FeaturePython)
  n = 1
  ref = Li_element
FEATURE [App::DocumentObjectGroupPython] I_element003  label="I_element : 002"  # scripted group (container) (typed FeaturePython)
  n = 1
  ref = I_element
FEATURE [App::DocumentObjectGroupPython] G4_LITHIUM_IODIDE  # scripted group (container) (typed FeaturePython)
  Dunit = g/cm3
  Dvalue = 3.494
  Group = -> [Li_element005,I_element003]
  conduct = 2
  density = 1
  expand = 3
  formula = G4_LITHIUM_IODIDE
  name = G4_LITHIUM_IODIDE
  specific = 4
FEATURE [App::DocumentObjectGroupPython] Li_element006  label="Li_element : 006"  # scripted group (container) (typed FeaturePython)
  n = 2
  ref = Li_element
FEATURE [App::DocumentObjectGroupPython] O_element055  label="O_element : 029"  # scripted group (container) (typed FeaturePython)
  n = 1
  ref = O_element
FEATURE [App::DocumentObjectGroupPython] G4_LITHIUM_OXIDE  # scripted group (container) (typed FeaturePython)
  Dunit = g/cm3
  Dvalue = 2.013
  Group = -> [Li_element006,O_element055]
  conduct = 2
  density = 1
  expand = 3
  formula = G4_LITHIUM_OXIDE
  name = G4_LITHIUM_OXIDE
  specific = 4
FEATURE [App::DocumentObjectGroupPython] Li_element007  label="Li_element : 007"  # scripted group (container) (typed FeaturePython)
  n = 2
  ref = Li_element
FEATURE [App::DocumentObjectGroupPython] B_element005  label="B_element : 005"  # scripted group (container) (typed FeaturePython)
  n = 4
  ref = B_element
FEATURE [App::DocumentObjectGroupPython] O_element056  label="O_element : 7"  # scripted group (container) (typed FeaturePython)
  n = 7
  ref = O_element
FEATURE [App::DocumentObjectGroupPython] G4_LITHIUM_TETRABORATE  # scripted group (container) (typed FeaturePython)
  Dunit = g/cm3
  Dvalue = 2.44
  Group = -> [Li_element007,B_element005,O_element056]
  conduct = 2
  density = 1
  expand = 3
  formula = G4_LITHIUM_TETRABORATE
  name = G4_LITHIUM_TETRABORATE
  specific = 4
FEATURE [App::DocumentObjectGroupPython] H_element051  label="H_element : 0.105"  # scripted group (container) (typed FeaturePython)
  n = 0.105
FEATURE [App::DocumentObjectGroupPython] C_element056  label="C_element : 0.083"  # scripted group (container) (typed FeaturePython)
  n = 0.083
FEATURE [App::DocumentObjectGroupPython] N_element023  label="N_element : 0.023"  # scripted group (container) (typed FeaturePython)
  n = 0.023
FEATURE [App::DocumentObjectGroupPython] O_element057  label="O_element : 0.779"  # scripted group (container) (typed FeaturePython)
  n = 0.779
FEATURE [App::DocumentObjectGroupPython] Na_element010  label="Na_element : 0.097"  # scripted group (container) (typed FeaturePython)
  n = 0.002
FEATURE [App::DocumentObjectGroupPython] P_element006  label="P_element : 0.105"  # scripted group (container) (typed FeaturePython)
  n = 0.001
FEATURE [App::DocumentObjectGroupPython] S_element016  label="S_element : 0.017"  # scripted group (container) (typed FeaturePython)
  n = 0.002
FEATURE [App::DocumentObjectGroupPython] Cl_element014  label="Cl_element : 0.587"  # scripted group (container) (typed FeaturePython)
  n = 0.003
FEATURE [App::DocumentObjectGroupPython] K_element005  label="K_element : 0.015"  # scripted group (container) (typed FeaturePython)
  n = 0.002
FEATURE [App::DocumentObjectGroupPython] G4_LUNG_ICRP  # scripted group (container) (typed FeaturePython)
  Dunit = g/cm3
  Dvalue = 1.04
  Group = -> [H_element051,C_element056,N_element023,O_element057,Na_element010,P_element006,S_element016,Cl_element014,K_element005]
  conduct = 2
  density = 1
  expand = 3
  formula = G4_LUNG_ICRP
  name = G4_LUNG_ICRP
  specific = 4
FEATURE [App::DocumentObjectGroupPython] H_element052  label="H_element : 0.116"  # scripted group (container) (typed FeaturePython)
  n = 0.114318
FEATURE [App::DocumentObjectGroupPython] C_element057  label="C_element : 0.656"  # scripted group (container) (typed FeaturePython)
  n = 0.655824
FEATURE [App::DocumentObjectGroupPython] O_element058  label="O_element : 0.092"  # scripted group (container) (typed FeaturePython)
  n = 0.0921831
FEATURE [App::DocumentObjectGroupPython] Mg_element004  label="Mg_element : 0.135"  # scripted group (container) (typed FeaturePython)
  n = 0.134792
FEATURE [App::DocumentObjectGroupPython] Ca_element013  label="Ca_element : 0.003"  # scripted group (container) (typed FeaturePython)
  n = 0.002883
FEATURE [App::DocumentObjectGroupPython] G4_M3_WAX  # scripted group (container) (typed FeaturePython)
  Dunit = g/cm3
  Dvalue = 1.05
  Group = -> [H_element052,C_element057,O_element058,Mg_element004,Ca_element013]
  conduct = 2
  density = 1
  expand = 3
  formula = G4_M3_WAX
  name = G4_M3_WAX
  specific = 4
FEATURE [App::DocumentObjectGroupPython] Mg_element005  label="Mg_element : 1"  # scripted group (container) (typed FeaturePython)
  n = 1
  ref = Mg_element
FEATURE [App::DocumentObjectGroupPython] C_element058  label="C_element : 031"  # scripted group (container) (typed FeaturePython)
  n = 1
  ref = C_element
FEATURE [App::DocumentObjectGroupPython] O_element059  label="O_element : 030"  # scripted group (container) (typed FeaturePython)
  n = 3
  ref = O_element
FEATURE [App::DocumentObjectGroupPython] G4_MAGNESIUM_CARBONATE  # scripted group (container) (typed FeaturePython)
  Dunit = g/cm3
  Dvalue = 2.958
  Group = -> [Mg_element005,C_element058,O_element059]
  conduct = 2
  density = 1
  expand = 3
  formula = G4_MAGNESIUM_CARBONATE
  name = G4_MAGNESIUM_CARBONATE
  specific = 4
FEATURE [App::DocumentObjectGroupPython] Mg_element006  label="Mg_element : 002"  # scripted group (container) (typed FeaturePython)
  n = 1
  ref = Mg_element
FEATURE [App::DocumentObjectGroupPython] F_element013  label="F_element : 005"  # scripted group (container) (typed FeaturePython)
  n = 2
  ref = F_element
FEATURE [App::DocumentObjectGroupPython] G4_MAGNESIUM_FLUORIDE  # scripted group (container) (typed FeaturePython)
  Dunit = g/cm3
  Dvalue = 3
  Group = -> [Mg_element006,F_element013]
  conduct = 2
  density = 1
  expand = 3
  formula = G4_MAGNESIUM_FLUORIDE
  name = G4_MAGNESIUM_FLUORIDE
  specific = 4
FEATURE [App::DocumentObjectGroupPython] Mg_element007  label="Mg_element : 003"  # scripted group (container) (typed FeaturePython)
  n = 1
  ref = Mg_element
FEATURE [App::DocumentObjectGroupPython] O_element060  label="O_element : 031"  # scripted group (container) (typed FeaturePython)
  n = 1
  ref = O_element
FEATURE [App::DocumentObjectGroupPython] G4_MAGNESIUM_OXIDE  # scripted group (container) (typed FeaturePython)
  Dunit = g/cm3
  Dvalue = 3.58
  Group = -> [Mg_element007,O_element060]
  conduct = 2
  density = 1
  expand = 3
  formula = G4_MAGNESIUM_OXIDE
  name = G4_MAGNESIUM_OXIDE
  specific = 4
FEATURE [App::DocumentObjectGroupPython] Mg_element008  label="Mg_element : 004"  # scripted group (container) (typed FeaturePython)
  n = 1
  ref = Mg_element
FEATURE [App::DocumentObjectGroupPython] B_element006  label="B_element : 006"  # scripted group (container) (typed FeaturePython)
  n = 4
  ref = B_element
FEATURE [App::DocumentObjectGroupPython] O_element061  label="O_element : 032"  # scripted group (container) (typed FeaturePython)
  n = 7
  ref = O_element
FEATURE [App::DocumentObjectGroupPython] G4_MAGNESIUM_TETRABORATE  # scripted group (container) (typed FeaturePython)
  Dunit = g/cm3
  Dvalue = 2.53
  Group = -> [Mg_element008,B_element006,O_element061]
  conduct = 2
  density = 1
  expand = 3
  formula = G4_MAGNESIUM_TETRABORATE
  name = G4_MAGNESIUM_TETRABORATE
  specific = 4
FEATURE [App::DocumentObjectGroupPython] Hg_element001  label="Hg_element : 1"  # scripted group (container) (typed FeaturePython)
  n = 1
  ref = Hg_element
FEATURE [App::DocumentObjectGroupPython] I_element004  label="I_element : 2"  # scripted group (container) (typed FeaturePython)
  n = 2
  ref = I_element
FEATURE [App::DocumentObjectGroupPython] G4_MERCURIC_IODIDE  # scripted group (container) (typed FeaturePython)
  Dunit = g/cm3
  Dvalue = 6.36
  Group = -> [Hg_element001,I_element004]
  conduct = 2
  density = 1
  expand = 3
  formula = G4_MERCURIC_IODIDE
  name = G4_MERCURIC_IODIDE
  specific = 4
FEATURE [App::DocumentObjectGroupPython] C_element059  label="C_element : 032"  # scripted group (container) (typed FeaturePython)
  n = 1
  ref = C_element
FEATURE [App::DocumentObjectGroupPython] H_element053  label="H_element : 028"  # scripted group (container) (typed FeaturePython)
  n = 4
  ref = H_element
FEATURE [App::DocumentObjectGroupPython] G4_METHANE  # scripted group (container) (typed FeaturePython)
  Dunit = g/cm3
  Dvalue = 0.000667151
  Group = -> [C_element059,H_element053]
  conduct = 2
  density = 1
  expand = 3
  formula = G4_METHANE
  name = G4_METHANE
  specific = 4
FEATURE [App::DocumentObjectGroupPython] C_element060  label="C_element : 033"  # scripted group (container) (typed FeaturePython)
  n = 1
  ref = C_element
FEATURE [App::DocumentObjectGroupPython] H_element054  label="H_element : 029"  # scripted group (container) (typed FeaturePython)
  n = 4
  ref = H_element
FEATURE [App::DocumentObjectGroupPython] O_element062  label="O_element : 033"  # scripted group (container) (typed FeaturePython)
  n = 1
  ref = O_element
FEATURE [App::DocumentObjectGroupPython] G4_METHANOL  # scripted group (container) (typed FeaturePython)
  Dunit = g/cm3
  Dvalue = 0.7914
  Group = -> [C_element060,H_element054,O_element062]
  conduct = 2
  density = 1
  expand = 3
  formula = G4_METHANOL
  name = G4_METHANOL
  specific = 4
FEATURE [App::DocumentObjectGroupPython] H_element055  label="H_element : 0.134"  # scripted group (container) (typed FeaturePython)
  n = 0.13404
FEATURE [App::DocumentObjectGroupPython] C_element061  label="C_element : 0.778"  # scripted group (container) (typed FeaturePython)
  n = 0.77796
FEATURE [App::DocumentObjectGroupPython] O_element063  label="O_element : 0.035"  # scripted group (container) (typed FeaturePython)
  n = 0.03502
FEATURE [App::DocumentObjectGroupPython] Mg_element009  label="Mg_element : 0.039"  # scripted group (container) (typed FeaturePython)
  n = 0.038594
FEATURE [App::DocumentObjectGroupPython] Ti_element002  label="Ti_element : 0.014"  # scripted group (container) (typed FeaturePython)
  n = 0.014386
FEATURE [App::DocumentObjectGroupPython] G4_MIX_D_WAX  # scripted group (container) (typed FeaturePython)
  Dunit = g/cm3
  Dvalue = 0.99
  Group = -> [H_element055,C_element061,O_element063,Mg_element009,Ti_element002]
  conduct = 2
  density = 1
  expand = 3
  formula = G4_MIX_D_WAX
  name = G4_MIX_D_WAX
  specific = 4
FEATURE [App::DocumentObjectGroupPython] H_element056  label="H_element : 0.135"  # scripted group (container) (typed FeaturePython)
  n = 0.081192
FEATURE [App::DocumentObjectGroupPython] C_element062  label="C_element : 0.583"  # scripted group (container) (typed FeaturePython)
  n = 0.583442
FEATURE [App::DocumentObjectGroupPython] N_element024  label="N_element : 0.018"  # scripted group (container) (typed FeaturePython)
  n = 0.017798
FEATURE [App::DocumentObjectGroupPython] O_element064  label="O_element : 0.186"  # scripted group (container) (typed FeaturePython)
  n = 0.186381
FEATURE [App::DocumentObjectGroupPython] Mg_element010  label="Mg_element : 0.130"  # scripted group (container) (typed FeaturePython)
  n = 0.130287
FEATURE [App::DocumentObjectGroupPython] Cl_element015  label="Cl_element : 0.588"  # scripted group (container) (typed FeaturePython)
  n = 0.0009
FEATURE [App::DocumentObjectGroupPython] G4_MS20_TISSUE  # scripted group (container) (typed FeaturePython)
  Dunit = g/cm3
  Dvalue = 1
  Group = -> [H_element056,C_element062,N_element024,O_element064,Mg_element010,Cl_element015]
  conduct = 2
  density = 1
  expand = 3
  formula = G4_MS20_TISSUE
  name = G4_MS20_TISSUE
  specific = 4
FEATURE [App::DocumentObjectGroupPython] H_element057  label="H_element : 0.136"  # scripted group (container) (typed FeaturePython)
  n = 0.102
FEATURE [App::DocumentObjectGroupPython] C_element063  label="C_element : 0.143"  # scripted group (container) (typed FeaturePython)
  n = 0.143
FEATURE [App::DocumentObjectGroupPython] N_element025  label="N_element : 0.034"  # scripted group (container) (typed FeaturePython)
  n = 0.034
FEATURE [App::DocumentObjectGroupPython] O_element065  label="O_element : 0.710"  # scripted group (container) (typed FeaturePython)
  n = 0.71
FEATURE [App::DocumentObjectGroupPython] Na_element011  label="Na_element : 0.098"  # scripted group (container) (typed FeaturePython)
  n = 0.001
FEATURE [App::DocumentObjectGroupPython] P_element007  label="P_element : 0.002"  # scripted group (container) (typed FeaturePython)
  n = 0.002
FEATURE [App::DocumentObjectGroupPython] S_element017  label="S_element : 0.018"  # scripted group (container) (typed FeaturePython)
  n = 0.003
FEATURE [App::DocumentObjectGroupPython] Cl_element016  label="Cl_element : 0.589"  # scripted group (container) (typed FeaturePython)
  n = 0.001
FEATURE [App::DocumentObjectGroupPython] K_element006  label="K_element : 0.004"  # scripted group (container) (typed FeaturePython)
  n = 0.004
FEATURE [App::DocumentObjectGroupPython] G4_MUSCLE_SKELETAL_ICRP  # scripted group (container) (typed FeaturePython)
  Dunit = g/cm3
  Dvalue = 1.05
  Group = -> [H_element057,C_element063,N_element025,O_element065,Na_element011,P_element007,S_element017,Cl_element016,K_element006]
  conduct = 2
  density = 1
  expand = 3
  formula = G4_MUSCLE_SKELETAL_ICRP
  name = G4_MUSCLE_SKELETAL_ICRP
  specific = 4
FEATURE [App::DocumentObjectGroupPython] H_element058  label="H_element : 0.137"  # scripted group (container) (typed FeaturePython)
  n = 0.102102
FEATURE [App::DocumentObjectGroupPython] C_element064  label="C_element : 0.123"  # scripted group (container) (typed FeaturePython)
  n = 0.123123
FEATURE [App::DocumentObjectGroupPython] N_element026  label="N_element : 0.756"  # scripted group (container) (typed FeaturePython)
  n = 0.035035
FEATURE [App::DocumentObjectGroupPython] O_element066  label="O_element : 0.730"  # scripted group (container) (typed FeaturePython)
  n = 0.72973
FEATURE [App::DocumentObjectGroupPython] Na_element012  label="Na_element : 0.099"  # scripted group (container) (typed FeaturePython)
  n = 0.001001
FEATURE [App::DocumentObjectGroupPython] P_element008  label="P_element : 0.106"  # scripted group (container) (typed FeaturePython)
  n = 0.002002
FEATURE [App::DocumentObjectGroupPython] S_element018  label="S_element : 0.019"  # scripted group (container) (typed FeaturePython)
  n = 0.004004
FEATURE [App::DocumentObjectGroupPython] K_element007  label="K_element : 0.016"  # scripted group (container) (typed FeaturePython)
  n = 0.003003
FEATURE [App::DocumentObjectGroupPython] G4_MUSCLE_STRIATED_ICRU  # scripted group (container) (typed FeaturePython)
  Dunit = g/cm3
  Dvalue = 1.04
  Group = -> [H_element058,C_element064,N_element026,O_element066,Na_element012,P_element008,S_element018,K_element007]
  conduct = 2
  density = 1
  expand = 3
  formula = G4_MUSCLE_STRIATED_ICRU
  name = G4_MUSCLE_STRIATED_ICRU
  specific = 4
FEATURE [App::DocumentObjectGroupPython] H_element059  label="H_element : 0.098"  # scripted group (container) (typed FeaturePython)
  n = 0.0982341
FEATURE [App::DocumentObjectGroupPython] C_element065  label="C_element : 0.156"  # scripted group (container) (typed FeaturePython)
  n = 0.156214
FEATURE [App::DocumentObjectGroupPython] N_element027  label="N_element : 0.757"  # scripted group (container) (typed FeaturePython)
  n = 0.035451
FEATURE [App::DocumentObjectGroupPython] O_element067  label="O_element : 0.880"  # scripted group (container) (typed FeaturePython)
  n = 0.710101
FEATURE [App::DocumentObjectGroupPython] G4_MUSCLE_WITH_SUCROSE  # scripted group (container) (typed FeaturePython)
  Dunit = g/cm3
  Dvalue = 1.11
  Group = -> [H_element059,C_element065,N_element027,O_element067]
  conduct = 2
  density = 1
  expand = 3
  formula = G4_MUSCLE_WITH_SUCROSE
  name = G4_MUSCLE_WITH_SUCROSE
  specific = 4
FEATURE [App::DocumentObjectGroupPython] H_element060  label="H_element : 0.138"  # scripted group (container) (typed FeaturePython)
  n = 0.101969
FEATURE [App::DocumentObjectGroupPython] C_element066  label="C_element : 0.120"  # scripted group (container) (typed FeaturePython)
  n = 0.120058
FEATURE [App::DocumentObjectGroupPython] N_element028  label="N_element : 0.758"  # scripted group (container) (typed FeaturePython)
  n = 0.035451
FEATURE [App::DocumentObjectGroupPython] O_element068  label="O_element : 0.743"  # scripted group (container) (typed FeaturePython)
  n = 0.742522
FEATURE [App::DocumentObjectGroupPython] G4_MUSCLE_WITHOUT_SUCROSE  # scripted group (container) (typed FeaturePython)
  Dunit = g/cm3
  Dvalue = 1.07
  Group = -> [H_element060,C_element066,N_element028,O_element068]
  conduct = 2
  density = 1
  expand = 3
  formula = G4_MUSCLE_WITHOUT_SUCROSE
  name = G4_MUSCLE_WITHOUT_SUCROSE
  specific = 4
FEATURE [App::DocumentObjectGroupPython] C_element067  label="C_element : 10"  # scripted group (container) (typed FeaturePython)
  n = 10
  ref = C_element
FEATURE [App::DocumentObjectGroupPython] H_element061  label="H_element : 030"  # scripted group (container) (typed FeaturePython)
  n = 8
  ref = H_element
FEATURE [App::DocumentObjectGroupPython] G4_NAPHTHALENE  # scripted group (container) (typed FeaturePython)
  Dunit = g/cm3
  Dvalue = 1.145
  Group = -> [C_element067,H_element061]
  conduct = 2
  density = 1
  expand = 3
  formula = G4_NAPHTHALENE
  name = G4_NAPHTHALENE
  specific = 4
FEATURE [App::DocumentObjectGroupPython] C_element068  label="C_element : 034"  # scripted group (container) (typed FeaturePython)
  n = 6
  ref = C_element
FEATURE [App::DocumentObjectGroupPython] H_element062  label="H_element : 031"  # scripted group (container) (typed FeaturePython)
  n = 5
  ref = H_element
FEATURE [App::DocumentObjectGroupPython] N_element029  label="N_element : 012"  # scripted group (container) (typed FeaturePython)
  n = 1
  ref = N_element
FEATURE [App::DocumentObjectGroupPython] O_element069  label="O_element : 034"  # scripted group (container) (typed FeaturePython)
  n = 2
  ref = O_element
FEATURE [App::DocumentObjectGroupPython] G4_NITROBENZENE  # scripted group (container) (typed FeaturePython)
  Dunit = g/cm3
  Dvalue = 1.19867
  Group = -> [C_element068,H_element062,N_element029,O_element069]
  conduct = 2
  density = 1
  expand = 3
  formula = G4_NITROBENZENE
  name = G4_NITROBENZENE
  specific = 4
FEATURE [App::DocumentObjectGroupPython] N_element030  label="N_element : 013"  # scripted group (container) (typed FeaturePython)
  n = 2
  ref = N_element
FEATURE [App::DocumentObjectGroupPython] O_element070  label="O_element : 035"  # scripted group (container) (typed FeaturePython)
  n = 1
  ref = O_element
FEATURE [App::DocumentObjectGroupPython] G4_NITROUS_OXIDE  # scripted group (container) (typed FeaturePython)
  Dunit = g/cm3
  Dvalue = 0.00183094
  Group = -> [N_element030,O_element070]
  conduct = 2
  density = 1
  expand = 3
  formula = G4_NITROUS_OXIDE
  name = G4_NITROUS_OXIDE
  specific = 4
FEATURE [App::DocumentObjectGroupPython] H_element063  label="H_element : 0.104"  # scripted group (container) (typed FeaturePython)
  n = 0.103509
FEATURE [App::DocumentObjectGroupPython] C_element069  label="C_element : 0.648"  # scripted group (container) (typed FeaturePython)
  n = 0.648416
FEATURE [App::DocumentObjectGroupPython] N_element031  label="N_element : 0.100"  # scripted group (container) (typed FeaturePython)
  n = 0.0995361
FEATURE [App::DocumentObjectGroupPython] O_element071  label="O_element : 0.149"  # scripted group (container) (typed FeaturePython)
  n = 0.148539
FEATURE [App::DocumentObjectGroupPython] G4_NYLON_8062  label="G4_NYLON-8062"  # scripted group (container) (typed FeaturePython)
  Dunit = g/cm3
  Dvalue = 1.08
  Group = -> [H_element063,C_element069,N_element031,O_element071]
  conduct = 2
  density = 1
  expand = 3
  formula = G4_NYLON-8062
  name = G4_NYLON-8062
  specific = 4
FEATURE [App::DocumentObjectGroupPython] C_element070  label="C_element : 035"  # scripted group (container) (typed FeaturePython)
  n = 6
  ref = C_element
FEATURE [App::DocumentObjectGroupPython] H_element064  label="H_element : 11"  # scripted group (container) (typed FeaturePython)
  n = 11
  ref = H_element
FEATURE [App::DocumentObjectGroupPython] N_element032  label="N_element : 014"  # scripted group (container) (typed FeaturePython)
  n = 1
  ref = N_element
FEATURE [App::DocumentObjectGroupPython] O_element072  label="O_element : 036"  # scripted group (container) (typed FeaturePython)
  n = 1
  ref = O_element
FEATURE [App::DocumentObjectGroupPython] G4_NYLON_6_6  label="G4_NYLON-6-6"  # scripted group (container) (typed FeaturePython)
  Dunit = g/cm3
  Dvalue = 1.14
  Group = -> [C_element070,H_element064,N_element032,O_element072]
  conduct = 2
  density = 1
  expand = 3
  formula = G4_NYLON-6-6
  name = G4_NYLON-6-6
  specific = 4
FEATURE [App::DocumentObjectGroupPython] H_element065  label="H_element : 0.139"  # scripted group (container) (typed FeaturePython)
  n = 0.107062
FEATURE [App::DocumentObjectGroupPython] C_element071  label="C_element : 0.680"  # scripted group (container) (typed FeaturePython)
  n = 0.680449
FEATURE [App::DocumentObjectGroupPython] N_element033  label="N_element : 0.099"  # scripted group (container) (typed FeaturePython)
  n = 0.099189
FEATURE [App::DocumentObjectGroupPython] O_element073  label="O_element : 0.113"  # scripted group (container) (typed FeaturePython)
  n = 0.1133
FEATURE [App::DocumentObjectGroupPython] G4_NYLON_6_10  label="G4_NYLON-6-10"  # scripted group (container) (typed FeaturePython)
  Dunit = g/cm3
  Dvalue = 1.14
  Group = -> [H_element065,C_element071,N_element033,O_element073]
  conduct = 2
  density = 1
  expand = 3
  formula = G4_NYLON-6-10
  name = G4_NYLON-6-10
  specific = 4
FEATURE [App::DocumentObjectGroupPython] H_element066  label="H_element : 0.140"  # scripted group (container) (typed FeaturePython)
  n = 0.115476
FEATURE [App::DocumentObjectGroupPython] C_element072  label="C_element : 0.721"  # scripted group (container) (typed FeaturePython)
  n = 0.720818
FEATURE [App::DocumentObjectGroupPython] N_element034  label="N_element : 0.076"  # scripted group (container) (typed FeaturePython)
  n = 0.0764169
FEATURE [App::DocumentObjectGroupPython] O_element074  label="O_element : 0.087"  # scripted group (container) (typed FeaturePython)
  n = 0.0872889
FEATURE [App::DocumentObjectGroupPython] G4_NYLON_11_RILSAN  label="G4_NYLON-11_RILSAN"  # scripted group (container) (typed FeaturePython)
  Dunit = g/cm3
  Dvalue = 1.425
  Group = -> [H_element066,C_element072,N_element034,O_element074]
  conduct = 2
  density = 1
  expand = 3
  formula = G4_NYLON-11_RILSAN
  name = G4_NYLON-11_RILSAN
  specific = 4
FEATURE [App::DocumentObjectGroupPython] C_element073  label="C_element : 8"  # scripted group (container) (typed FeaturePython)
  n = 8
  ref = C_element
FEATURE [App::DocumentObjectGroupPython] H_element067  label="H_element : 18"  # scripted group (container) (typed FeaturePython)
  n = 18
  ref = H_element
FEATURE [App::DocumentObjectGroupPython] G4_OCTANE  # scripted group (container) (typed FeaturePython)
  Dunit = g/cm3
  Dvalue = 0.7026
  Group = -> [C_element073,H_element067]
  conduct = 2
  density = 1
  expand = 3
  formula = G4_OCTANE
  name = G4_OCTANE
  specific = 4
FEATURE [App::DocumentObjectGroupPython] C_element074  label="C_element : 25"  # scripted group (container) (typed FeaturePython)
  n = 25
  ref = C_element
FEATURE [App::DocumentObjectGroupPython] H_element068  label="H_element : 52"  # scripted group (container) (typed FeaturePython)
  n = 52
  ref = H_element
FEATURE [App::DocumentObjectGroupPython] G4_PARAFFIN  # scripted group (container) (typed FeaturePython)
  Dunit = g/cm3
  Dvalue = 0.93
  Group = -> [C_element074,H_element068]
  conduct = 2
  density = 1
  expand = 3
  formula = G4_PARAFFIN
  name = G4_PARAFFIN
  specific = 4
FEATURE [App::DocumentObjectGroupPython] C_element075  label="C_element : 036"  # scripted group (container) (typed FeaturePython)
  n = 5
  ref = C_element
FEATURE [App::DocumentObjectGroupPython] H_element069  label="H_element : 032"  # scripted group (container) (typed FeaturePython)
  n = 12
  ref = H_element
FEATURE [App::DocumentObjectGroupPython] G4_N_PENTANE  label="G4_N-PENTANE"  # scripted group (container) (typed FeaturePython)
  Dunit = g/cm3
  Dvalue = 0.6262
  Group = -> [C_element075,H_element069]
  conduct = 2
  density = 1
  expand = 3
  formula = G4_N-PENTANE
  name = G4_N-PENTANE
  specific = 4
FEATURE [App::DocumentObjectGroupPython] H_element070  label="H_element : 0.014"  # scripted group (container) (typed FeaturePython)
  n = 0.0141
FEATURE [App::DocumentObjectGroupPython] C_element076  label="C_element : 0.072"  # scripted group (container) (typed FeaturePython)
  n = 0.072261
FEATURE [App::DocumentObjectGroupPython] N_element035  label="N_element : 0.019"  # scripted group (container) (typed FeaturePython)
  n = 0.01932
FEATURE [App::DocumentObjectGroupPython] O_element075  label="O_element : 0.066"  # scripted group (container) (typed FeaturePython)
  n = 0.066101
FEATURE [App::DocumentObjectGroupPython] S_element019  label="S_element : 0.020"  # scripted group (container) (typed FeaturePython)
  n = 0.00189
FEATURE [App::DocumentObjectGroupPython] Br_element004  label="Br_element : 0.349"  # scripted group (container) (typed FeaturePython)
  n = 0.349103
FEATURE [App::DocumentObjectGroupPython] Ag_element001  label="Ag_element : 0.474"  # scripted group (container) (typed FeaturePython)
  n = 0.474105
FEATURE [App::DocumentObjectGroupPython] I_element005  label="I_element : 0.003"  # scripted group (container) (typed FeaturePython)
  n = 0.00312
FEATURE [App::DocumentObjectGroupPython] G4_PHOTO_EMULSION  # scripted group (container) (typed FeaturePython)
  Dunit = g/cm3
  Dvalue = 3.815
  Group = -> [H_element070,C_element076,N_element035,O_element075,S_element019,Br_element004,Ag_element001,I_element005]
  conduct = 2
  density = 1
  expand = 3
  formula = G4_PHOTO_EMULSION
  name = G4_PHOTO_EMULSION
  specific = 4
FEATURE [App::DocumentObjectGroupPython] C_element077  label="C_element : 9"  # scripted group (container) (typed FeaturePython)
  n = 9
  ref = C_element
FEATURE [App::DocumentObjectGroupPython] H_element071  label="H_element : 033"  # scripted group (container) (typed FeaturePython)
  n = 10
  ref = H_element
FEATURE [App::DocumentObjectGroupPython] G4_PLASTIC_SC_VINYLTOLUENE  # scripted group (container) (typed FeaturePython)
  Dunit = g/cm3
  Dvalue = 1.032
  Group = -> [C_element077,H_element071]
  conduct = 2
  density = 1
  expand = 3
  formula = G4_PLASTIC_SC_VINYLTOLUENE
  name = G4_PLASTIC_SC_VINYLTOLUENE
  specific = 4
FEATURE [App::DocumentObjectGroupPython] Pu_element001  label="Pu_element : 1"  # scripted group (container) (typed FeaturePython)
  n = 1
  ref = Pu_element
FEATURE [App::DocumentObjectGroupPython] O_element076  label="O_element : 037"  # scripted group (container) (typed FeaturePython)
  n = 2
  ref = O_element
FEATURE [App::DocumentObjectGroupPython] G4_PLUTONIUM_DIOXIDE  # scripted group (container) (typed FeaturePython)
  Dunit = g/cm3
  Dvalue = 11.46
  Group = -> [Pu_element001,O_element076]
  conduct = 2
  density = 1
  expand = 3
  formula = G4_PLUTONIUM_DIOXIDE
  name = G4_PLUTONIUM_DIOXIDE
  specific = 4
FEATURE [App::DocumentObjectGroupPython] C_element078  label="C_element : 037"  # scripted group (container) (typed FeaturePython)
  n = 3
  ref = C_element
FEATURE [App::DocumentObjectGroupPython] H_element072  label="H_element : 034"  # scripted group (container) (typed FeaturePython)
  n = 3
  ref = H_element
FEATURE [App::DocumentObjectGroupPython] N_element036  label="N_element : 015"  # scripted group (container) (typed FeaturePython)
  n = 1
  ref = N_element
FEATURE [App::DocumentObjectGroupPython] G4_POLYACRYLONITRILE  # scripted group (container) (typed FeaturePython)
  Dunit = g/cm3
  Dvalue = 1.17
  Group = -> [C_element078,H_element072,N_element036]
  conduct = 2
  density = 1
  expand = 3
  formula = G4_POLYACRYLONITRILE
  name = G4_POLYACRYLONITRILE
  specific = 4
FEATURE [App::DocumentObjectGroupPython] C_element079  label="C_element : 16"  # scripted group (container) (typed FeaturePython)
  n = 16
  ref = C_element
FEATURE [App::DocumentObjectGroupPython] H_element073  label="H_element : 035"  # scripted group (container) (typed FeaturePython)
  n = 14
  ref = H_element
FEATURE [App::DocumentObjectGroupPython] O_element077  label="O_element : 038"  # scripted group (container) (typed FeaturePython)
  n = 3
  ref = O_element
FEATURE [App::DocumentObjectGroupPython] G4_POLYCARBONATE  # scripted group (container) (typed FeaturePython)
  Dunit = g/cm3
  Dvalue = 1.2
  Group = -> [C_element079,H_element073,O_element077]
  conduct = 2
  density = 1
  expand = 3
  formula = G4_POLYCARBONATE
  name = G4_POLYCARBONATE
  specific = 4
FEATURE [App::DocumentObjectGroupPython] C_element080  label="C_element : 038"  # scripted group (container) (typed FeaturePython)
  n = 8
  ref = C_element
FEATURE [App::DocumentObjectGroupPython] H_element074  label="H_element : 036"  # scripted group (container) (typed FeaturePython)
  n = 7
  ref = H_element
FEATURE [App::DocumentObjectGroupPython] Cl_element017  label="Cl_element : 007"  # scripted group (container) (typed FeaturePython)
  n = 1
  ref = Cl_element
FEATURE [App::DocumentObjectGroupPython] G4_POLYCHLOROSTYRENE  # scripted group (container) (typed FeaturePython)
  Dunit = g/cm3
  Dvalue = 1.3
  Group = -> [C_element080,H_element074,Cl_element017]
  conduct = 2
  density = 1
  expand = 3
  formula = G4_POLYCHLOROSTYRENE
  name = G4_POLYCHLOROSTYRENE
  specific = 4
FEATURE [App::DocumentObjectGroupPython] C_element081  label="C_element : 039"  # scripted group (container) (typed FeaturePython)
  n = 1
  ref = C_element
FEATURE [App::DocumentObjectGroupPython] H_element075  label="H_element : 037"  # scripted group (container) (typed FeaturePython)
  n = 2
  ref = H_element
FEATURE [App::DocumentObjectGroupPython] G4_POLYETHYLENE  # scripted group (container) (typed FeaturePython)
  Dunit = g/cm3
  Dvalue = 0.94
  Group = -> [C_element081,H_element075]
  conduct = 2
  density = 1
  expand = 3
  formula = G4_POLYETHYLENE
  name = G4_POLYETHYLENE
  specific = 4
FEATURE [App::DocumentObjectGroupPython] C_element082  label="C_element : 040"  # scripted group (container) (typed FeaturePython)
  n = 10
  ref = C_element
FEATURE [App::DocumentObjectGroupPython] H_element076  label="H_element : 038"  # scripted group (container) (typed FeaturePython)
  n = 8
  ref = H_element
FEATURE [App::DocumentObjectGroupPython] O_element078  label="O_element : 039"  # scripted group (container) (typed FeaturePython)
  n = 4
  ref = O_element
FEATURE [App::DocumentObjectGroupPython] G4_MYLAR  # scripted group (container) (typed FeaturePython)
  Dunit = g/cm3
  Dvalue = 1.4
  Group = -> [C_element082,H_element076,O_element078]
  conduct = 2
  density = 1
  expand = 3
  formula = G4_MYLAR
  name = G4_MYLAR
  specific = 4
FEATURE [App::DocumentObjectGroupPython] C_element083  label="C_element : 041"  # scripted group (container) (typed FeaturePython)
  n = 5
  ref = C_element
FEATURE [App::DocumentObjectGroupPython] H_element077  label="H_element : 039"  # scripted group (container) (typed FeaturePython)
  n = 8
  ref = H_element
FEATURE [App::DocumentObjectGroupPython] O_element079  label="O_element : 040"  # scripted group (container) (typed FeaturePython)
  n = 2
  ref = O_element
FEATURE [App::DocumentObjectGroupPython] G4_PLEXIGLASS  # scripted group (container) (typed FeaturePython)
  Dunit = g/cm3
  Dvalue = 1.19
  Group = -> [C_element083,H_element077,O_element079]
  conduct = 2
  density = 1
  expand = 3
  formula = G4_PLEXIGLASS
  name = G4_PLEXIGLASS
  specific = 4
FEATURE [App::DocumentObjectGroupPython] C_element084  label="C_element : 042"  # scripted group (container) (typed FeaturePython)
  n = 1
  ref = C_element
FEATURE [App::DocumentObjectGroupPython] H_element078  label="H_element : 040"  # scripted group (container) (typed FeaturePython)
  n = 2
  ref = H_element
FEATURE [App::DocumentObjectGroupPython] O_element080  label="O_element : 041"  # scripted group (container) (typed FeaturePython)
  n = 1
  ref = O_element
FEATURE [App::DocumentObjectGroupPython] G4_POLYOXYMETHYLENE  # scripted group (container) (typed FeaturePython)
  Dunit = g/cm3
  Dvalue = 1.425
  Group = -> [C_element084,H_element078,O_element080]
  conduct = 2
  density = 1
  expand = 3
  formula = G4_POLYOXYMETHYLENE
  name = G4_POLYOXYMETHYLENE
  specific = 4
FEATURE [App::DocumentObjectGroupPython] C_element085  label="C_element : 043"  # scripted group (container) (typed FeaturePython)
  n = 2
  ref = C_element
FEATURE [App::DocumentObjectGroupPython] H_element079  label="H_element : 041"  # scripted group (container) (typed FeaturePython)
  n = 4
  ref = H_element
FEATURE [App::DocumentObjectGroupPython] G4_POLYPROPYLENE  # scripted group (container) (typed FeaturePython)
  Dunit = g/cm3
  Dvalue = 0.9
  Group = -> [C_element085,H_element079]
  conduct = 2
  density = 1
  expand = 3
  formula = G4_POLYPROPYLENE
  name = G4_POLYPROPYLENE
  specific = 4
FEATURE [App::DocumentObjectGroupPython] C_element086  label="C_element : 044"  # scripted group (container) (typed FeaturePython)
  n = 8
  ref = C_element
FEATURE [App::DocumentObjectGroupPython] H_element080  label="H_element : 042"  # scripted group (container) (typed FeaturePython)
  n = 8
  ref = H_element
FEATURE [App::DocumentObjectGroupPython] G4_POLYSTYRENE  # scripted group (container) (typed FeaturePython)
  Dunit = g/cm3
  Dvalue = 1.06
  Group = -> [C_element086,H_element080]
  conduct = 2
  density = 1
  expand = 3
  formula = G4_POLYSTYRENE
  name = G4_POLYSTYRENE
  specific = 4
FEATURE [App::DocumentObjectGroupPython] C_element087  label="C_element : 045"  # scripted group (container) (typed FeaturePython)
  n = 2
  ref = C_element
FEATURE [App::DocumentObjectGroupPython] F_element014  label="F_element : 4"  # scripted group (container) (typed FeaturePython)
  n = 4
  ref = F_element
FEATURE [App::DocumentObjectGroupPython] G4_TEFLON  # scripted group (container) (typed FeaturePython)
  Dunit = g/cm3
  Dvalue = 2.2
  Group = -> [C_element087,F_element014]
  conduct = 2
  density = 1
  expand = 3
  formula = G4_TEFLON
  name = G4_TEFLON
  specific = 4
FEATURE [App::DocumentObjectGroupPython] C_element088  label="C_element : 046"  # scripted group (container) (typed FeaturePython)
  n = 2
  ref = C_element
FEATURE [App::DocumentObjectGroupPython] F_element015  label="F_element : 006"  # scripted group (container) (typed FeaturePython)
  n = 3
  ref = F_element
FEATURE [App::DocumentObjectGroupPython] Cl_element018  label="Cl_element : 008"  # scripted group (container) (typed FeaturePython)
  n = 1
  ref = Cl_element
FEATURE [App::DocumentObjectGroupPython] G4_POLYTRIFLUOROCHLOROETHYLENE  # scripted group (container) (typed FeaturePython)
  Dunit = g/cm3
  Dvalue = 2.1
  Group = -> [C_element088,F_element015,Cl_element018]
  conduct = 2
  density = 1
  expand = 3
  formula = G4_POLYTRIFLUOROCHLOROETHYLENE
  name = G4_POLYTRIFLUOROCHLOROETHYLENE
  specific = 4
FEATURE [App::DocumentObjectGroupPython] C_element089  label="C_element : 047"  # scripted group (container) (typed FeaturePython)
  n = 4
  ref = C_element
FEATURE [App::DocumentObjectGroupPython] H_element081  label="H_element : 043"  # scripted group (container) (typed FeaturePython)
  n = 6
  ref = H_element
FEATURE [App::DocumentObjectGroupPython] O_element081  label="O_element : 042"  # scripted group (container) (typed FeaturePython)
  n = 2
  ref = O_element
FEATURE [App::DocumentObjectGroupPython] G4_POLYVINYL_ACETATE  # scripted group (container) (typed FeaturePython)
  Dunit = g/cm3
  Dvalue = 1.19
  Group = -> [C_element089,H_element081,O_element081]
  conduct = 2
  density = 1
  expand = 3
  formula = G4_POLYVINYL_ACETATE
  name = G4_POLYVINYL_ACETATE
  specific = 4
FEATURE [App::DocumentObjectGroupPython] C_element090  label="C_element : 048"  # scripted group (container) (typed FeaturePython)
  n = 2
  ref = C_element
FEATURE [App::DocumentObjectGroupPython] H_element082  label="H_element : 044"  # scripted group (container) (typed FeaturePython)
  n = 4
  ref = H_element
FEATURE [App::DocumentObjectGroupPython] O_element082  label="O_element : 043"  # scripted group (container) (typed FeaturePython)
  n = 1
  ref = O_element
FEATURE [App::DocumentObjectGroupPython] G4_POLYVINYL_ALCOHOL  # scripted group (container) (typed FeaturePython)
  Dunit = g/cm3
  Dvalue = 1.3
  Group = -> [C_element090,H_element082,O_element082]
  conduct = 2
  density = 1
  expand = 3
  formula = G4_POLYVINYL_ALCOHOL
  name = G4_POLYVINYL_ALCOHOL
  specific = 4
FEATURE [App::DocumentObjectGroupPython] C_element091  label="C_element : 049"  # scripted group (container) (typed FeaturePython)
  n = 8
  ref = C_element
FEATURE [App::DocumentObjectGroupPython] H_element083  label="H_element : 045"  # scripted group (container) (typed FeaturePython)
  n = 14
  ref = H_element
FEATURE [App::DocumentObjectGroupPython] O_element083  label="O_element : 044"  # scripted group (container) (typed FeaturePython)
  n = 2
  ref = O_element
FEATURE [App::DocumentObjectGroupPython] G4_POLYVINYL_BUTYRAL  # scripted group (container) (typed FeaturePython)
  Dunit = g/cm3
  Dvalue = 1.12
  Group = -> [C_element091,H_element083,O_element083]
  conduct = 2
  density = 1
  expand = 3
  formula = G4_POLYVINYL_BUTYRAL
  name = G4_POLYVINYL_BUTYRAL
  specific = 4
FEATURE [App::DocumentObjectGroupPython] C_element092  label="C_element : 050"  # scripted group (container) (typed FeaturePython)
  n = 2
  ref = C_element
FEATURE [App::DocumentObjectGroupPython] H_element084  label="H_element : 046"  # scripted group (container) (typed FeaturePython)
  n = 3
  ref = H_element
FEATURE [App::DocumentObjectGroupPython] Cl_element019  label="Cl_element : 009"  # scripted group (container) (typed FeaturePython)
  n = 1
  ref = Cl_element
FEATURE [App::DocumentObjectGroupPython] G4_POLYVINYL_CHLORIDE  # scripted group (container) (typed FeaturePython)
  Dunit = g/cm3
  Dvalue = 1.3
  Group = -> [C_element092,H_element084,Cl_element019]
  conduct = 2
  density = 1
  expand = 3
  formula = G4_POLYVINYL_CHLORIDE
  name = G4_POLYVINYL_CHLORIDE
  specific = 4
FEATURE [App::DocumentObjectGroupPython] C_element093  label="C_element : 051"  # scripted group (container) (typed FeaturePython)
  n = 2
  ref = C_element
FEATURE [App::DocumentObjectGroupPython] H_element085  label="H_element : 047"  # scripted group (container) (typed FeaturePython)
  n = 2
  ref = H_element
FEATURE [App::DocumentObjectGroupPython] Cl_element020  label="Cl_element : 010"  # scripted group (container) (typed FeaturePython)
  n = 2
  ref = Cl_element
FEATURE [App::DocumentObjectGroupPython] G4_POLYVINYLIDENE_CHLORIDE  # scripted group (container) (typed FeaturePython)
  Dunit = g/cm3
  Dvalue = 1.7
  Group = -> [C_element093,H_element085,Cl_element020]
  conduct = 2
  density = 1
  expand = 3
  formula = G4_POLYVINYLIDENE_CHLORIDE
  name = G4_POLYVINYLIDENE_CHLORIDE
  specific = 4
FEATURE [App::DocumentObjectGroupPython] C_element094  label="C_element : 052"  # scripted group (container) (typed FeaturePython)
  n = 2
  ref = C_element
FEATURE [App::DocumentObjectGroupPython] H_element086  label="H_element : 048"  # scripted group (container) (typed FeaturePython)
  n = 2
  ref = H_element
FEATURE [App::DocumentObjectGroupPython] F_element016  label="F_element : 007"  # scripted group (container) (typed FeaturePython)
  n = 2
  ref = F_element
FEATURE [App::DocumentObjectGroupPython] G4_POLYVINYLIDENE_FLUORIDE  # scripted group (container) (typed FeaturePython)
  Dunit = g/cm3
  Dvalue = 1.76
  Group = -> [C_element094,H_element086,F_element016]
  conduct = 2
  density = 1
  expand = 3
  formula = G4_POLYVINYLIDENE_FLUORIDE
  name = G4_POLYVINYLIDENE_FLUORIDE
  specific = 4
FEATURE [App::DocumentObjectGroupPython] C_element095  label="C_element : 053"  # scripted group (container) (typed FeaturePython)
  n = 6
  ref = C_element
FEATURE [App::DocumentObjectGroupPython] H_element087  label="H_element : 9"  # scripted group (container) (typed FeaturePython)
  n = 9
  ref = H_element
FEATURE [App::DocumentObjectGroupPython] N_element037  label="N_element : 016"  # scripted group (container) (typed FeaturePython)
  n = 1
  ref = N_element
FEATURE [App::DocumentObjectGroupPython] O_element084  label="O_element : 045"  # scripted group (container) (typed FeaturePython)
  n = 1
  ref = O_element
FEATURE [App::DocumentObjectGroupPython] G4_POLYVINYL_PYRROLIDONE  # scripted group (container) (typed FeaturePython)
  Dunit = g/cm3
  Dvalue = 1.25
  Group = -> [C_element095,H_element087,N_element037,O_element084]
  conduct = 2
  density = 1
  expand = 3
  formula = G4_POLYVINYL_PYRROLIDONE
  name = G4_POLYVINYL_PYRROLIDONE
  specific = 4
FEATURE [App::DocumentObjectGroupPython] K_element008  label="K_element : 1"  # scripted group (container) (typed FeaturePython)
  n = 1
  ref = K_element
FEATURE [App::DocumentObjectGroupPython] I_element006  label="I_element : 003"  # scripted group (container) (typed FeaturePython)
  n = 1
  ref = I_element
FEATURE [App::DocumentObjectGroupPython] G4_POTASSIUM_IODIDE  # scripted group (container) (typed FeaturePython)
  Dunit = g/cm3
  Dvalue = 3.13
  Group = -> [K_element008,I_element006]
  conduct = 2
  density = 1
  expand = 3
  formula = G4_POTASSIUM_IODIDE
  name = G4_POTASSIUM_IODIDE
  specific = 4
FEATURE [App::DocumentObjectGroupPython] K_element009  label="K_element : 2"  # scripted group (container) (typed FeaturePython)
  n = 2
  ref = K_element
FEATURE [App::DocumentObjectGroupPython] O_element085  label="O_element : 046"  # scripted group (container) (typed FeaturePython)
  n = 1
  ref = O_element
FEATURE [App::DocumentObjectGroupPython] G4_POTASSIUM_OXIDE  # scripted group (container) (typed FeaturePython)
  Dunit = g/cm3
  Dvalue = 2.32
  Group = -> [K_element009,O_element085]
  conduct = 2
  density = 1
  expand = 3
  formula = G4_POTASSIUM_OXIDE
  name = G4_POTASSIUM_OXIDE
  specific = 4
FEATURE [App::DocumentObjectGroupPython] C_element096  label="C_element : 054"  # scripted group (container) (typed FeaturePython)
  n = 3
  ref = C_element
FEATURE [App::DocumentObjectGroupPython] H_element088  label="H_element : 049"  # scripted group (container) (typed FeaturePython)
  n = 8
  ref = H_element
FEATURE [App::DocumentObjectGroupPython] G4_PROPANE  # scripted group (container) (typed FeaturePython)
  Dunit = g/cm3
  Dvalue = 0.00187939
  Group = -> [C_element096,H_element088]
  conduct = 2
  density = 1
  expand = 3
  formula = G4_PROPANE
  name = G4_PROPANE
  specific = 4
FEATURE [App::DocumentObjectGroupPython] C_element097  label="C_element : 055"  # scripted group (container) (typed FeaturePython)
  n = 3
  ref = C_element
FEATURE [App::DocumentObjectGroupPython] H_element089  label="H_element : 050"  # scripted group (container) (typed FeaturePython)
  n = 8
  ref = H_element
FEATURE [App::DocumentObjectGroupPython] G4_lPROPANE  # scripted group (container) (typed FeaturePython)
  Dunit = g/cm3
  Dvalue = 0.43
  Group = -> [C_element097,H_element089]
  conduct = 2
  density = 1
  expand = 3
  formula = G4_lPROPANE
  name = G4_lPROPANE
  specific = 4
FEATURE [App::DocumentObjectGroupPython] C_element098  label="C_element : 056"  # scripted group (container) (typed FeaturePython)
  n = 3
  ref = C_element
FEATURE [App::DocumentObjectGroupPython] H_element090  label="H_element : 051"  # scripted group (container) (typed FeaturePython)
  n = 8
  ref = H_element
FEATURE [App::DocumentObjectGroupPython] O_element086  label="O_element : 047"  # scripted group (container) (typed FeaturePython)
  n = 1
  ref = O_element
FEATURE [App::DocumentObjectGroupPython] G4_N_PROPYL_ALCOHOL  label="G4_N-PROPYL_ALCOHOL"  # scripted group (container) (typed FeaturePython)
  Dunit = g/cm3
  Dvalue = 0.8035
  Group = -> [C_element098,H_element090,O_element086]
  conduct = 2
  density = 1
  expand = 3
  formula = G4_N-PROPYL_ALCOHOL
  name = G4_N-PROPYL_ALCOHOL
  specific = 4
FEATURE [App::DocumentObjectGroupPython] C_element099  label="C_element : 057"  # scripted group (container) (typed FeaturePython)
  n = 5
  ref = C_element
FEATURE [App::DocumentObjectGroupPython] H_element091  label="H_element : 052"  # scripted group (container) (typed FeaturePython)
  n = 5
  ref = H_element
FEATURE [App::DocumentObjectGroupPython] N_element038  label="N_element : 017"  # scripted group (container) (typed FeaturePython)
  n = 1
  ref = N_element
FEATURE [App::DocumentObjectGroupPython] G4_PYRIDINE  # scripted group (container) (typed FeaturePython)
  Dunit = g/cm3
  Dvalue = 0.9819
  Group = -> [C_element099,H_element091,N_element038]
  conduct = 2
  density = 1
  expand = 3
  formula = G4_PYRIDINE
  name = G4_PYRIDINE
  specific = 4
FEATURE [App::DocumentObjectGroupPython] H_element092  label="H_element : 0.144"  # scripted group (container) (typed FeaturePython)
  n = 0.143711
FEATURE [App::DocumentObjectGroupPython] C_element100  label="C_element : 0.856"  # scripted group (container) (typed FeaturePython)
  n = 0.856289
FEATURE [App::DocumentObjectGroupPython] G4_RUBBER_BUTYL  # scripted group (container) (typed FeaturePython)
  Dunit = g/cm3
  Dvalue = 0.92
  Group = -> [H_element092,C_element100]
  conduct = 2
  density = 1
  expand = 3
  formula = G4_RUBBER_BUTYL
  name = G4_RUBBER_BUTYL
  specific = 4
FEATURE [App::DocumentObjectGroupPython] H_element093  label="H_element : 0.118"  # scripted group (container) (typed FeaturePython)
  n = 0.118371
FEATURE [App::DocumentObjectGroupPython] C_element101  label="C_element : 0.882"  # scripted group (container) (typed FeaturePython)
  n = 0.881629
FEATURE [App::DocumentObjectGroupPython] G4_RUBBER_NATURAL  # scripted group (container) (typed FeaturePython)
  Dunit = g/cm3
  Dvalue = 0.92
  Group = -> [H_element093,C_element101]
  conduct = 2
  density = 1
  expand = 3
  formula = G4_RUBBER_NATURAL
  name = G4_RUBBER_NATURAL
  specific = 4
FEATURE [App::DocumentObjectGroupPython] H_element094  label="H_element : 0.145"  # scripted group (container) (typed FeaturePython)
  n = 0.05692
FEATURE [App::DocumentObjectGroupPython] C_element102  label="C_element : 0.543"  # scripted group (container) (typed FeaturePython)
  n = 0.542646
FEATURE [App::DocumentObjectGroupPython] Cl_element021  label="Cl_element : 0.400"  # scripted group (container) (typed FeaturePython)
  n = 0.400434
FEATURE [App::DocumentObjectGroupPython] G4_RUBBER_NEOPRENE  # scripted group (container) (typed FeaturePython)
  Dunit = g/cm3
  Dvalue = 1.23
  Group = -> [H_element094,C_element102,Cl_element021]
  conduct = 2
  density = 1
  expand = 3
  formula = G4_RUBBER_NEOPRENE
  name = G4_RUBBER_NEOPRENE
  specific = 4
FEATURE [App::DocumentObjectGroupPython] Si_element006  label="Si_element : 1"  # scripted group (container) (typed FeaturePython)
  n = 1
  ref = Si_element
FEATURE [App::DocumentObjectGroupPython] O_element087  label="O_element : 048"  # scripted group (container) (typed FeaturePython)
  n = 2
  ref = O_element
FEATURE [App::DocumentObjectGroupPython] G4_SILICON_DIOXIDE  # scripted group (container) (typed FeaturePython)
  Dunit = g/cm3
  Dvalue = 2.32
  Group = -> [Si_element006,O_element087]
  conduct = 2
  density = 1
  expand = 3
  formula = G4_SILICON_DIOXIDE
  name = G4_SILICON_DIOXIDE
  specific = 4
FEATURE [App::DocumentObjectGroupPython] Ag_element002  label="Ag_element : 1"  # scripted group (container) (typed FeaturePython)
  n = 1
  ref = Ag_element
FEATURE [App::DocumentObjectGroupPython] Br_element005  label="Br_element : 003"  # scripted group (container) (typed FeaturePython)
  n = 1
  ref = Br_element
FEATURE [App::DocumentObjectGroupPython] G4_SILVER_BROMIDE  # scripted group (container) (typed FeaturePython)
  Dunit = g/cm3
  Dvalue = 6.473
  Group = -> [Ag_element002,Br_element005]
  conduct = 2
  density = 1
  expand = 3
  formula = G4_SILVER_BROMIDE
  name = G4_SILVER_BROMIDE
  specific = 4
FEATURE [App::DocumentObjectGroupPython] Ag_element003  label="Ag_element : 002"  # scripted group (container) (typed FeaturePython)
  n = 1
  ref = Ag_element
FEATURE [App::DocumentObjectGroupPython] Cl_element022  label="Cl_element : 011"  # scripted group (container) (typed FeaturePython)
  n = 1
  ref = Cl_element
FEATURE [App::DocumentObjectGroupPython] G4_SILVER_CHLORIDE  # scripted group (container) (typed FeaturePython)
  Dunit = g/cm3
  Dvalue = 5.56
  Group = -> [Ag_element003,Cl_element022]
  conduct = 2
  density = 1
  expand = 3
  formula = G4_SILVER_CHLORIDE
  name = G4_SILVER_CHLORIDE
  specific = 4
FEATURE [App::DocumentObjectGroupPython] Br_element006  label="Br_element : 0.423"  # scripted group (container) (typed FeaturePython)
  n = 0.422895
FEATURE [App::DocumentObjectGroupPython] Ag_element004  label="Ag_element : 0.574"  # scripted group (container) (typed FeaturePython)
  n = 0.573748
FEATURE [App::DocumentObjectGroupPython] I_element007  label="I_element : 0.649"  # scripted group (container) (typed FeaturePython)
  n = 0.003357
FEATURE [App::DocumentObjectGroupPython] G4_SILVER_HALIDES  # scripted group (container) (typed FeaturePython)
  Dunit = g/cm3
  Dvalue = 6.47
  Group = -> [Br_element006,Ag_element004,I_element007]
  conduct = 2
  density = 1
  expand = 3
  formula = G4_SILVER_HALIDES
  name = G4_SILVER_HALIDES
  specific = 4
FEATURE [App::DocumentObjectGroupPython] Ag_element005  label="Ag_element : 003"  # scripted group (container) (typed FeaturePython)
  n = 1
  ref = Ag_element
FEATURE [App::DocumentObjectGroupPython] I_element008  label="I_element : 004"  # scripted group (container) (typed FeaturePython)
  n = 1
  ref = I_element
FEATURE [App::DocumentObjectGroupPython] G4_SILVER_IODIDE  # scripted group (container) (typed FeaturePython)
  Dunit = g/cm3
  Dvalue = 6.01
  Group = -> [Ag_element005,I_element008]
  conduct = 2
  density = 1
  expand = 3
  formula = G4_SILVER_IODIDE
  name = G4_SILVER_IODIDE
  specific = 4
FEATURE [App::DocumentObjectGroupPython] H_element095  label="H_element : 0.100"  # scripted group (container) (typed FeaturePython)
  n = 0.1
FEATURE [App::DocumentObjectGroupPython] C_element103  label="C_element : 0.204"  # scripted group (container) (typed FeaturePython)
  n = 0.204
FEATURE [App::DocumentObjectGroupPython] N_element039  label="N_element : 0.759"  # scripted group (container) (typed FeaturePython)
  n = 0.042
FEATURE [App::DocumentObjectGroupPython] O_element088  label="O_element : 0.645"  # scripted group (container) (typed FeaturePython)
  n = 0.645
FEATURE [App::DocumentObjectGroupPython] Na_element013  label="Na_element : 0.100"  # scripted group (container) (typed FeaturePython)
  n = 0.002
FEATURE [App::DocumentObjectGroupPython] P_element009  label="P_element : 0.107"  # scripted group (container) (typed FeaturePython)
  n = 0.001
FEATURE [App::DocumentObjectGroupPython] S_element020  label="S_element : 0.021"  # scripted group (container) (typed FeaturePython)
  n = 0.002
FEATURE [App::DocumentObjectGroupPython] Cl_element023  label="Cl_element : 0.590"  # scripted group (container) (typed FeaturePython)
  n = 0.003
FEATURE [App::DocumentObjectGroupPython] K_element010  label="K_element : 0.001"  # scripted group (container) (typed FeaturePython)
  n = 0.001
FEATURE [App::DocumentObjectGroupPython] G4_SKIN_ICRP  # scripted group (container) (typed FeaturePython)
  Dunit = g/cm3
  Dvalue = 1.09
  Group = -> [H_element095,C_element103,N_element039,O_element088,Na_element013,P_element009,S_element020,Cl_element023,K_element010]
  conduct = 2
  density = 1
  expand = 3
  formula = G4_SKIN_ICRP
  name = G4_SKIN_ICRP
  specific = 4
FEATURE [App::DocumentObjectGroupPython] Na_element014  label="Na_element : 2"  # scripted group (container) (typed FeaturePython)
  n = 2
  ref = Na_element
FEATURE [App::DocumentObjectGroupPython] C_element104  label="C_element : 058"  # scripted group (container) (typed FeaturePython)
  n = 1
  ref = C_element
FEATURE [App::DocumentObjectGroupPython] O_element089  label="O_element : 049"  # scripted group (container) (typed FeaturePython)
  n = 3
  ref = O_element
FEATURE [App::DocumentObjectGroupPython] G4_SODIUM_CARBONATE  # scripted group (container) (typed FeaturePython)
  Dunit = g/cm3
  Dvalue = 2.532
  Group = -> [Na_element014,C_element104,O_element089]
  conduct = 2
  density = 1
  expand = 3
  formula = G4_SODIUM_CARBONATE
  name = G4_SODIUM_CARBONATE
  specific = 4
FEATURE [App::DocumentObjectGroupPython] Na_element015  label="Na_element : 1"  # scripted group (container) (typed FeaturePython)
  n = 1
  ref = Na_element
FEATURE [App::DocumentObjectGroupPython] I_element009  label="I_element : 005"  # scripted group (container) (typed FeaturePython)
  n = 1
  ref = I_element
FEATURE [App::DocumentObjectGroupPython] G4_SODIUM_IODIDE  # scripted group (container) (typed FeaturePython)
  Dunit = g/cm3
  Dvalue = 3.667
  Group = -> [Na_element015,I_element009]
  conduct = 2
  density = 1
  expand = 3
  formula = G4_SODIUM_IODIDE
  name = G4_SODIUM_IODIDE
  specific = 4
FEATURE [App::DocumentObjectGroupPython] Na_element016  label="Na_element : 003"  # scripted group (container) (typed FeaturePython)
  n = 2
  ref = Na_element
FEATURE [App::DocumentObjectGroupPython] O_element090  label="O_element : 050"  # scripted group (container) (typed FeaturePython)
  n = 1
  ref = O_element
FEATURE [App::DocumentObjectGroupPython] G4_SODIUM_MONOXIDE  # scripted group (container) (typed FeaturePython)
  Dunit = g/cm3
  Dvalue = 2.27
  Group = -> [Na_element016,O_element090]
  conduct = 2
  density = 1
  expand = 3
  formula = G4_SODIUM_MONOXIDE
  name = G4_SODIUM_MONOXIDE
  specific = 4
FEATURE [App::DocumentObjectGroupPython] Na_element017  label="Na_element : 004"  # scripted group (container) (typed FeaturePython)
  n = 1
  ref = Na_element
FEATURE [App::DocumentObjectGroupPython] N_element040  label="N_element : 018"  # scripted group (container) (typed FeaturePython)
  n = 1
  ref = N_element
FEATURE [App::DocumentObjectGroupPython] O_element091  label="O_element : 051"  # scripted group (container) (typed FeaturePython)
  n = 3
  ref = O_element
FEATURE [App::DocumentObjectGroupPython] G4_SODIUM_NITRATE  # scripted group (container) (typed FeaturePython)
  Dunit = g/cm3
  Dvalue = 2.261
  Group = -> [Na_element017,N_element040,O_element091]
  conduct = 2
  density = 1
  expand = 3
  formula = G4_SODIUM_NITRATE
  name = G4_SODIUM_NITRATE
  specific = 4
FEATURE [App::DocumentObjectGroupPython] C_element105  label="C_element : 059"  # scripted group (container) (typed FeaturePython)
  n = 14
  ref = C_element
FEATURE [App::DocumentObjectGroupPython] H_element096  label="H_element : 053"  # scripted group (container) (typed FeaturePython)
  n = 12
  ref = H_element
FEATURE [App::DocumentObjectGroupPython] G4_STILBENE  # scripted group (container) (typed FeaturePython)
  Dunit = g/cm3
  Dvalue = 0.9707
  Group = -> [C_element105,H_element096]
  conduct = 2
  density = 1
  expand = 3
  formula = G4_STILBENE
  name = G4_STILBENE
  specific = 4
FEATURE [App::DocumentObjectGroupPython] C_element106  label="C_element : 12"  # scripted group (container) (typed FeaturePython)
  n = 12
  ref = C_element
FEATURE [App::DocumentObjectGroupPython] H_element097  label="H_element : 22"  # scripted group (container) (typed FeaturePython)
  n = 22
  ref = H_element
FEATURE [App::DocumentObjectGroupPython] O_element092  label="O_element : 11"  # scripted group (container) (typed FeaturePython)
  n = 11
  ref = O_element
FEATURE [App::DocumentObjectGroupPython] G4_SUCROSE  # scripted group (container) (typed FeaturePython)
  Dunit = g/cm3
  Dvalue = 1.5805
  Group = -> [C_element106,H_element097,O_element092]
  conduct = 2
  density = 1
  expand = 3
  formula = G4_SUCROSE
  name = G4_SUCROSE
  specific = 4
FEATURE [App::DocumentObjectGroupPython] C_element107  label="C_element : 18"  # scripted group (container) (typed FeaturePython)
  n = 18
  ref = C_element
FEATURE [App::DocumentObjectGroupPython] H_element098  label="H_element : 054"  # scripted group (container) (typed FeaturePython)
  n = 14
  ref = H_element
FEATURE [App::DocumentObjectGroupPython] G4_TERPHENYL  # scripted group (container) (typed FeaturePython)
  Dunit = g/cm3
  Dvalue = 1.24
  Group = -> [C_element107,H_element098]
  conduct = 2
  density = 1
  expand = 3
  formula = G4_TERPHENYL
  name = G4_TERPHENYL
  specific = 4
FEATURE [App::DocumentObjectGroupPython] H_element099  label="H_element : 0.146"  # scripted group (container) (typed FeaturePython)
  n = 0.106
FEATURE [App::DocumentObjectGroupPython] C_element108  label="C_element : 0.883"  # scripted group (container) (typed FeaturePython)
  n = 0.099
FEATURE [App::DocumentObjectGroupPython] N_element041  label="N_element : 0.020"  # scripted group (container) (typed FeaturePython)
  n = 0.02
FEATURE [App::DocumentObjectGroupPython] O_element093  label="O_element : 0.766"  # scripted group (container) (typed FeaturePython)
  n = 0.766
FEATURE [App::DocumentObjectGroupPython] Na_element018  label="Na_element : 0.101"  # scripted group (container) (typed FeaturePython)
  n = 0.002
FEATURE [App::DocumentObjectGroupPython] P_element010  label="P_element : 0.108"  # scripted group (container) (typed FeaturePython)
  n = 0.001
FEATURE [App::DocumentObjectGroupPython] S_element021  label="S_element : 0.022"  # scripted group (container) (typed FeaturePython)
  n = 0.002
FEATURE [App::DocumentObjectGroupPython] Cl_element024  label="Cl_element : 0.002"  # scripted group (container) (typed FeaturePython)
  n = 0.002
FEATURE [App::DocumentObjectGroupPython] K_element011  label="K_element : 0.017"  # scripted group (container) (typed FeaturePython)
  n = 0.002
FEATURE [App::DocumentObjectGroupPython] G4_TESTIS_ICRP  # scripted group (container) (typed FeaturePython)
  Dunit = g/cm3
  Dvalue = 1.04
  Group = -> [H_element099,C_element108,N_element041,O_element093,Na_element018,P_element010,S_element021,Cl_element024,K_element011]
  conduct = 2
  density = 1
  expand = 3
  formula = G4_TESTIS_ICRP
  name = G4_TESTIS_ICRP
  specific = 4
FEATURE [App::DocumentObjectGroupPython] C_element109  label="C_element : 060"  # scripted group (container) (typed FeaturePython)
  n = 2
  ref = C_element
FEATURE [App::DocumentObjectGroupPython] Cl_element025  label="Cl_element : 012"  # scripted group (container) (typed FeaturePython)
  n = 4
  ref = Cl_element
FEATURE [App::DocumentObjectGroupPython] G4_TETRACHLOROETHYLENE  # scripted group (container) (typed FeaturePython)
  Dunit = g/cm3
  Dvalue = 1.625
  Group = -> [C_element109,Cl_element025]
  conduct = 2
  density = 1
  expand = 3
  formula = G4_TETRACHLOROETHYLENE
  name = G4_TETRACHLOROETHYLENE
  specific = 4
FEATURE [App::DocumentObjectGroupPython] Tl_element001  label="Tl_element : 1"  # scripted group (container) (typed FeaturePython)
  n = 1
  ref = Tl_element
FEATURE [App::DocumentObjectGroupPython] Cl_element026  label="Cl_element : 013"  # scripted group (container) (typed FeaturePython)
  n = 1
  ref = Cl_element
FEATURE [App::DocumentObjectGroupPython] G4_THALLIUM_CHLORIDE  # scripted group (container) (typed FeaturePython)
  Dunit = g/cm3
  Dvalue = 7.004
  Group = -> [Tl_element001,Cl_element026]
  conduct = 2
  density = 1
  expand = 3
  formula = G4_THALLIUM_CHLORIDE
  name = G4_THALLIUM_CHLORIDE
  specific = 4
FEATURE [App::DocumentObjectGroupPython] H_element100  label="H_element : 0.147"  # scripted group (container) (typed FeaturePython)
  n = 0.105
FEATURE [App::DocumentObjectGroupPython] C_element110  label="C_element : 0.256"  # scripted group (container) (typed FeaturePython)
  n = 0.256
FEATURE [App::DocumentObjectGroupPython] N_element042  label="N_element : 0.760"  # scripted group (container) (typed FeaturePython)
  n = 0.027
FEATURE [App::DocumentObjectGroupPython] O_element094  label="O_element : 0.602"  # scripted group (container) (typed FeaturePython)
  n = 0.602
FEATURE [App::DocumentObjectGroupPython] Na_element019  label="Na_element : 0.102"  # scripted group (container) (typed FeaturePython)
  n = 0.001
FEATURE [App::DocumentObjectGroupPython] P_element011  label="P_element : 0.109"  # scripted group (container) (typed FeaturePython)
  n = 0.002
FEATURE [App::DocumentObjectGroupPython] S_element022  label="S_element : 0.023"  # scripted group (container) (typed FeaturePython)
  n = 0.003
FEATURE [App::DocumentObjectGroupPython] Cl_element027  label="Cl_element : 0.591"  # scripted group (container) (typed FeaturePython)
  n = 0.002
FEATURE [App::DocumentObjectGroupPython] K_element012  label="K_element : 0.018"  # scripted group (container) (typed FeaturePython)
  n = 0.002
FEATURE [App::DocumentObjectGroupPython] G4_TISSUE_SOFT_ICRP  # scripted group (container) (typed FeaturePython)
  Dunit = g/cm3
  Dvalue = 1.03
  Group = -> [H_element100,C_element110,N_element042,O_element094,Na_element019,P_element011,S_element022,Cl_element027,K_element012]
  conduct = 2
  density = 1
  expand = 3
  formula = G4_TISSUE_SOFT_ICRP
  name = G4_TISSUE_SOFT_ICRP
  specific = 4
FEATURE [App::DocumentObjectGroupPython] H_element101  label="H_element : 0.148"  # scripted group (container) (typed FeaturePython)
  n = 0.101
FEATURE [App::DocumentObjectGroupPython] C_element111  label="C_element : 0.111"  # scripted group (container) (typed FeaturePython)
  n = 0.111
FEATURE [App::DocumentObjectGroupPython] N_element043  label="N_element : 0.026"  # scripted group (container) (typed FeaturePython)
  n = 0.026
FEATURE [App::DocumentObjectGroupPython] O_element095  label="O_element : 0.762"  # scripted group (container) (typed FeaturePython)
  n = 0.762
FEATURE [App::DocumentObjectGroupPython] G4_TISSUE_SOFT_ICRU_4  label="G4_TISSUE_SOFT_ICRU-4"  # scripted group (container) (typed FeaturePython)
  Dunit = g/cm3
  Dvalue = 1
  Group = -> [H_element101,C_element111,N_element043,O_element095]
  conduct = 2
  density = 1
  expand = 3
  formula = G4_TISSUE_SOFT_ICRU-4
  name = G4_TISSUE_SOFT_ICRU-4
  specific = 4
FEATURE [App::DocumentObjectGroupPython] H_element102  label="H_element : 0.149"  # scripted group (container) (typed FeaturePython)
  n = 0.101869
FEATURE [App::DocumentObjectGroupPython] C_element112  label="C_element : 0.456"  # scripted group (container) (typed FeaturePython)
  n = 0.456179
FEATURE [App::DocumentObjectGroupPython] N_element044  label="N_element : 0.761"  # scripted group (container) (typed FeaturePython)
  n = 0.035172
FEATURE [App::DocumentObjectGroupPython] O_element096  label="O_element : 0.407"  # scripted group (container) (typed FeaturePython)
  n = 0.40678
FEATURE [App::DocumentObjectGroupPython] G4_TISSUE_METHANE  label="G4_TISSUE-METHANE"  # scripted group (container) (typed FeaturePython)
  Dunit = g/cm3
  Dvalue = 0.00106409
  Group = -> [H_element102,C_element112,N_element044,O_element096]
  conduct = 2
  density = 1
  expand = 3
  formula = G4_TISSUE-METHANE
  name = G4_TISSUE-METHANE
  specific = 4
FEATURE [App::DocumentObjectGroupPython] H_element103  label="H_element : 0.103"  # scripted group (container) (typed FeaturePython)
  n = 0.102672
FEATURE [App::DocumentObjectGroupPython] C_element113  label="C_element : 0.569"  # scripted group (container) (typed FeaturePython)
  n = 0.56894
FEATURE [App::DocumentObjectGroupPython] N_element045  label="N_element : 0.762"  # scripted group (container) (typed FeaturePython)
  n = 0.035022
FEATURE [App::DocumentObjectGroupPython] O_element097  label="O_element : 0.293"  # scripted group (container) (typed FeaturePython)
  n = 0.293366
FEATURE [App::DocumentObjectGroupPython] G4_TISSUE_PROPANE  label="G4_TISSUE-PROPANE"  # scripted group (container) (typed FeaturePython)
  Dunit = g/cm3
  Dvalue = 0.00182628
  Group = -> [H_element103,C_element113,N_element045,O_element097]
  conduct = 2
  density = 1
  expand = 3
  formula = G4_TISSUE-PROPANE
  name = G4_TISSUE-PROPANE
  specific = 4
FEATURE [App::DocumentObjectGroupPython] Ti_element003  label="Ti_element : 1"  # scripted group (container) (typed FeaturePython)
  n = 1
  ref = Ti_element
FEATURE [App::DocumentObjectGroupPython] O_element098  label="O_element : 052"  # scripted group (container) (typed FeaturePython)
  n = 2
  ref = O_element
FEATURE [App::DocumentObjectGroupPython] G4_TITANIUM_DIOXIDE  # scripted group (container) (typed FeaturePython)
  Dunit = g/cm3
  Dvalue = 4.26
  Group = -> [Ti_element003,O_element098]
  conduct = 2
  density = 1
  expand = 3
  formula = G4_TITANIUM_DIOXIDE
  name = G4_TITANIUM_DIOXIDE
  specific = 4
FEATURE [App::DocumentObjectGroupPython] C_element114  label="C_element : 061"  # scripted group (container) (typed FeaturePython)
  n = 7
  ref = C_element
FEATURE [App::DocumentObjectGroupPython] H_element104  label="H_element : 055"  # scripted group (container) (typed FeaturePython)
  n = 8
  ref = H_element
FEATURE [App::DocumentObjectGroupPython] G4_TOLUENE  # scripted group (container) (typed FeaturePython)
  Dunit = g/cm3
  Dvalue = 0.8669
  Group = -> [C_element114,H_element104]
  conduct = 2
  density = 1
  expand = 3
  formula = G4_TOLUENE
  name = G4_TOLUENE
  specific = 4
FEATURE [App::DocumentObjectGroupPython] C_element115  label="C_element : 062"  # scripted group (container) (typed FeaturePython)
  n = 2
  ref = C_element
FEATURE [App::DocumentObjectGroupPython] H_element105  label="H_element : 056"  # scripted group (container) (typed FeaturePython)
  n = 1
  ref = H_element
FEATURE [App::DocumentObjectGroupPython] Cl_element028  label="Cl_element : 014"  # scripted group (container) (typed FeaturePython)
  n = 3
  ref = Cl_element
FEATURE [App::DocumentObjectGroupPython] G4_TRICHLOROETHYLENE  # scripted group (container) (typed FeaturePython)
  Dunit = g/cm3
  Dvalue = 1.46
  Group = -> [C_element115,H_element105,Cl_element028]
  conduct = 2
  density = 1
  expand = 3
  formula = G4_TRICHLOROETHYLENE
  name = G4_TRICHLOROETHYLENE
  specific = 4
FEATURE [App::DocumentObjectGroupPython] C_element116  label="C_element : 063"  # scripted group (container) (typed FeaturePython)
  n = 6
  ref = C_element
FEATURE [App::DocumentObjectGroupPython] H_element106  label="H_element : 15"  # scripted group (container) (typed FeaturePython)
  n = 15
  ref = H_element
FEATURE [App::DocumentObjectGroupPython] O_element099  label="O_element : 053"  # scripted group (container) (typed FeaturePython)
  n = 4
  ref = O_element
FEATURE [App::DocumentObjectGroupPython] P_element012  label="P_element : 1"  # scripted group (container) (typed FeaturePython)
  n = 1
  ref = P_element
FEATURE [App::DocumentObjectGroupPython] G4_TRIETHYL_PHOSPHATE  # scripted group (container) (typed FeaturePython)
  Dunit = g/cm3
  Dvalue = 1.07
  Group = -> [C_element116,H_element106,O_element099,P_element012]
  conduct = 2
  density = 1
  expand = 3
  formula = G4_TRIETHYL_PHOSPHATE
  name = G4_TRIETHYL_PHOSPHATE
  specific = 4
FEATURE [App::DocumentObjectGroupPython] W_element003  label="W_element : 003"  # scripted group (container) (typed FeaturePython)
  n = 1
  ref = W_element
FEATURE [App::DocumentObjectGroupPython] F_element017  label="F_element : 6"  # scripted group (container) (typed FeaturePython)
  n = 6
  ref = F_element
FEATURE [App::DocumentObjectGroupPython] G4_TUNGSTEN_HEXAFLUORIDE  # scripted group (container) (typed FeaturePython)
  Dunit = g/cm3
  Dvalue = 2.4
  Group = -> [W_element003,F_element017]
  conduct = 2
  density = 1
  expand = 3
  formula = G4_TUNGSTEN_HEXAFLUORIDE
  name = G4_TUNGSTEN_HEXAFLUORIDE
  specific = 4
FEATURE [App::DocumentObjectGroupPython] U_element001  label="U_element : 1"  # scripted group (container) (typed FeaturePython)
  n = 1
  ref = U_element
FEATURE [App::DocumentObjectGroupPython] C_element117  label="C_element : 064"  # scripted group (container) (typed FeaturePython)
  n = 2
  ref = C_element
FEATURE [App::DocumentObjectGroupPython] G4_URANIUM_DICARBIDE  # scripted group (container) (typed FeaturePython)
  Dunit = g/cm3
  Dvalue = 11.28
  Group = -> [U_element001,C_element117]
  conduct = 2
  density = 1
  expand = 3
  formula = G4_URANIUM_DICARBIDE
  name = G4_URANIUM_DICARBIDE
  specific = 4
FEATURE [App::DocumentObjectGroupPython] U_element002  label="U_element : 002"  # scripted group (container) (typed FeaturePython)
  n = 1
  ref = U_element
FEATURE [App::DocumentObjectGroupPython] C_element118  label="C_element : 065"  # scripted group (container) (typed FeaturePython)
  n = 1
  ref = C_element
FEATURE [App::DocumentObjectGroupPython] G4_URANIUM_MONOCARBIDE  # scripted group (container) (typed FeaturePython)
  Dunit = g/cm3
  Dvalue = 13.63
  Group = -> [U_element002,C_element118]
  conduct = 2
  density = 1
  expand = 3
  formula = G4_URANIUM_MONOCARBIDE
  name = G4_URANIUM_MONOCARBIDE
  specific = 4
FEATURE [App::DocumentObjectGroupPython] U_element003  label="U_element : 003"  # scripted group (container) (typed FeaturePython)
  n = 1
  ref = U_element
FEATURE [App::DocumentObjectGroupPython] O_element100  label="O_element : 054"  # scripted group (container) (typed FeaturePython)
  n = 2
  ref = O_element
FEATURE [App::DocumentObjectGroupPython] G4_URANIUM_OXIDE  # scripted group (container) (typed FeaturePython)
  Dunit = g/cm3
  Dvalue = 10.96
  Group = -> [U_element003,O_element100]
  conduct = 2
  density = 1
  expand = 3
  formula = G4_URANIUM_OXIDE
  name = G4_URANIUM_OXIDE
  specific = 4
FEATURE [App::DocumentObjectGroupPython] C_element119  label="C_element : 066"  # scripted group (container) (typed FeaturePython)
  n = 1
  ref = C_element
FEATURE [App::DocumentObjectGroupPython] H_element107  label="H_element : 057"  # scripted group (container) (typed FeaturePython)
  n = 4
  ref = H_element
FEATURE [App::DocumentObjectGroupPython] N_element046  label="N_element : 019"  # scripted group (container) (typed FeaturePython)
  n = 2
  ref = N_element
FEATURE [App::DocumentObjectGroupPython] O_element101  label="O_element : 055"  # scripted group (container) (typed FeaturePython)
  n = 1
  ref = O_element
FEATURE [App::DocumentObjectGroupPython] G4_UREA  # scripted group (container) (typed FeaturePython)
  Dunit = g/cm3
  Dvalue = 1.323
  Group = -> [C_element119,H_element107,N_element046,O_element101]
  conduct = 2
  density = 1
  expand = 3
  formula = G4_UREA
  name = G4_UREA
  specific = 4
FEATURE [App::DocumentObjectGroupPython] C_element120  label="C_element : 067"  # scripted group (container) (typed FeaturePython)
  n = 5
  ref = C_element
FEATURE [App::DocumentObjectGroupPython] H_element108  label="H_element : 058"  # scripted group (container) (typed FeaturePython)
  n = 11
  ref = H_element
FEATURE [App::DocumentObjectGroupPython] N_element047  label="N_element : 020"  # scripted group (container) (typed FeaturePython)
  n = 1
  ref = N_element
FEATURE [App::DocumentObjectGroupPython] O_element102  label="O_element : 056"  # scripted group (container) (typed FeaturePython)
  n = 2
  ref = O_element
FEATURE [App::DocumentObjectGroupPython] G4_VALINE  # scripted group (container) (typed FeaturePython)
  Dunit = g/cm3
  Dvalue = 1.23
  Group = -> [C_element120,H_element108,N_element047,O_element102]
  conduct = 2
  density = 1
  expand = 3
  formula = G4_VALINE
  name = G4_VALINE
  specific = 4
FEATURE [App::DocumentObjectGroupPython] H_element109  label="H_element : 0.009"  # scripted group (container) (typed FeaturePython)
  n = 0.009417
FEATURE [App::DocumentObjectGroupPython] C_element121  label="C_element : 0.281"  # scripted group (container) (typed FeaturePython)
  n = 0.280555
FEATURE [App::DocumentObjectGroupPython] F_element018  label="F_element : 0.710"  # scripted group (container) (typed FeaturePython)
  n = 0.710028
FEATURE [App::DocumentObjectGroupPython] G4_VITON  # scripted group (container) (typed FeaturePython)
  Dunit = g/cm3
  Dvalue = 1.8
  Group = -> [H_element109,C_element121,F_element018]
  conduct = 2
  density = 1
  expand = 3
  formula = G4_VITON
  name = G4_VITON
  specific = 4
FEATURE [App::DocumentObjectGroupPython] H_element110  label="H_element : 059"  # scripted group (container) (typed FeaturePython)
  n = 2
  ref = H_element
FEATURE [App::DocumentObjectGroupPython] O_element103  label="O_element : 057"  # scripted group (container) (typed FeaturePython)
  n = 1
  ref = O_element
FEATURE [App::DocumentObjectGroupPython] G4_WATER  # scripted group (container) (typed FeaturePython)
  Dunit = g/cm3
  Dvalue = 1
  Group = -> [H_element110,O_element103]
  conduct = 2
  density = 1
  expand = 3
  formula = G4_WATER
  name = G4_WATER
  specific = 4
FEATURE [App::DocumentObjectGroupPython] H_element111  label="H_element : 060"  # scripted group (container) (typed FeaturePython)
  n = 2
  ref = H_element
FEATURE [App::DocumentObjectGroupPython] O_element104  label="O_element : 058"  # scripted group (container) (typed FeaturePython)
  n = 1
  ref = O_element
FEATURE [App::DocumentObjectGroupPython] G4_WATER_VAPOR  # scripted group (container) (typed FeaturePython)
  Dunit = g/cm3
  Dvalue = 0.000756182
  Group = -> [H_element111,O_element104]
  conduct = 2
  density = 1
  expand = 3
  formula = G4_WATER_VAPOR
  name = G4_WATER_VAPOR
  specific = 4
FEATURE [App::DocumentObjectGroupPython] C_element122  label="C_element : 068"  # scripted group (container) (typed FeaturePython)
  n = 8
  ref = C_element
FEATURE [App::DocumentObjectGroupPython] H_element112  label="H_element : 061"  # scripted group (container) (typed FeaturePython)
  n = 10
  ref = H_element
FEATURE [App::DocumentObjectGroupPython] G4_XYLENE  # scripted group (container) (typed FeaturePython)
  Dunit = g/cm3
  Dvalue = 0.87
  Group = -> [C_element122,H_element112]
  conduct = 2
  density = 1
  expand = 3
  formula = G4_XYLENE
  name = G4_XYLENE
  specific = 4
FEATURE [App::DocumentObjectGroupPython] C_element123  label="C_element : 069"  # scripted group (container) (typed FeaturePython)
  n = 1
  ref = C_element
FEATURE [App::DocumentObjectGroupPython] G4_GRAPHITE  # scripted group (container) (typed FeaturePython)
  Dunit = g/cm3
  Dvalue = 2.21
  Group = -> [C_element123]
  conduct = 2
  density = 1
  expand = 3
  formula = G4_GRAPHITE
  name = G4_GRAPHITE
  specific = 4
FEATURE [App::DocumentObjectGroupPython] NIST  # scripted group (container) (typed FeaturePython)
  Group = -> [G4_A_150_TISSUE,G4_ACETONE,G4_ACETYLENE,G4_ADENINE,G4_ADIPOSE_TISSUE_ICRP,G4_AIR,G4_ALANINE,G4_ALUMINUM_OXIDE,G4_AMBER,G4_AMMONIA,G4_ANILINE,G4_ANTHRACENE,G4_B_100_BONE,G4_BAKELITE,G4_BARIUM_FLUORIDE,G4_BARIUM_SULFATE,G4_BENZENE,G4_BERYLLIUM_OXIDE,G4_BGO,G4_BLOOD_ICRP,G4_BONE_COMPACT_ICRU,G4_BONE_CORTICAL_ICRP,G4_BORON_CARBIDE,G4_BORON_OXIDE,G4_BRAIN_ICRP,G4_BUTANE,G4_N_BUTYL_ALCOHOL,G4_C_552,+152 more]
FEATURE [App::DocumentObjectGroupPython] H_element113  label="H_element : 062"  # scripted group (container) (typed FeaturePython)
  n = 1
  ref = H_element
FEATURE [App::DocumentObjectGroupPython] G4_H  # scripted group (container) (typed FeaturePython)
  Dunit = g/cm3
  Dvalue = 8.3748e-05
  Group = -> [H_element113]
  conduct = 2
  density = 1
  expand = 3
  formula = H
  name = G4_H
  specific = 4
FEATURE [App::DocumentObjectGroupPython] He_element001  label="He_element : 1"  # scripted group (container) (typed FeaturePython)
  n = 1
  ref = He_element
FEATURE [App::DocumentObjectGroupPython] G4_He  # scripted group (container) (typed FeaturePython)
  Dunit = g/cm3
  Dvalue = 0.000166322
  Group = -> [He_element001]
  conduct = 2
  density = 1
  expand = 3
  formula = He
  name = G4_He
  specific = 4
FEATURE [App::DocumentObjectGroupPython] Li_element008  label="Li_element : 008"  # scripted group (container) (typed FeaturePython)
  n = 1
  ref = Li_element
FEATURE [App::DocumentObjectGroupPython] G4_Li  # scripted group (container) (typed FeaturePython)
  Dunit = g/cm3
  Dvalue = 0.534
  Group = -> [Li_element008]
  conduct = 2
  density = 1
  expand = 3
  formula = Li
  name = G4_Li
  specific = 4
FEATURE [App::DocumentObjectGroupPython] Be_element002  label="Be_element : 002"  # scripted group (container) (typed FeaturePython)
  n = 1
  ref = Be_element
FEATURE [App::DocumentObjectGroupPython] G4_Be  # scripted group (container) (typed FeaturePython)
  Dunit = g/cm3
  Dvalue = 1.848
  Group = -> [Be_element002]
  conduct = 2
  density = 1
  expand = 3
  formula = Be
  name = G4_Be
  specific = 4
FEATURE [App::DocumentObjectGroupPython] B_element007  label="B_element : 007"  # scripted group (container) (typed FeaturePython)
  n = 1
  ref = B_element
FEATURE [App::DocumentObjectGroupPython] G4_B  # scripted group (container) (typed FeaturePython)
  Dunit = g/cm3
  Dvalue = 2.37
  Group = -> [B_element007]
  conduct = 2
  density = 1
  expand = 3
  formula = B
  name = G4_B
  specific = 4
FEATURE [App::DocumentObjectGroupPython] C_element124  label="C_element : 070"  # scripted group (container) (typed FeaturePython)
  n = 1
  ref = C_element
FEATURE [App::DocumentObjectGroupPython] G4_C  # scripted group (container) (typed FeaturePython)
  Dunit = g/cm3
  Dvalue = 2
  Group = -> [C_element124]
  conduct = 2
  density = 1
  expand = 3
  formula = C
  name = G4_C
  specific = 4
FEATURE [App::DocumentObjectGroupPython] N_element048  label="N_element : 021"  # scripted group (container) (typed FeaturePython)
  n = 1
  ref = N_element
FEATURE [App::DocumentObjectGroupPython] G4_N  # scripted group (container) (typed FeaturePython)
  Dunit = g/cm3
  Dvalue = 0.0011652
  Group = -> [N_element048]
  conduct = 2
  density = 1
  expand = 3
  formula = N
  name = G4_N
  specific = 4
FEATURE [App::DocumentObjectGroupPython] O_element105  label="O_element : 059"  # scripted group (container) (typed FeaturePython)
  n = 1
  ref = O_element
FEATURE [App::DocumentObjectGroupPython] G4_O  # scripted group (container) (typed FeaturePython)
  Dunit = g/cm3
  Dvalue = 0.00133151
  Group = -> [O_element105]
  conduct = 2
  density = 1
  expand = 3
  formula = O
  name = G4_O
  specific = 4
FEATURE [App::DocumentObjectGroupPython] F_element019  label="F_element : 008"  # scripted group (container) (typed FeaturePython)
  n = 1
  ref = F_element
FEATURE [App::DocumentObjectGroupPython] G4_F  # scripted group (container) (typed FeaturePython)
  Dunit = g/cm3
  Dvalue = 0.00158029
  Group = -> [F_element019]
  conduct = 2
  density = 1
  expand = 3
  formula = F
  name = G4_F
  specific = 4
FEATURE [App::DocumentObjectGroupPython] Ne_element001  label="Ne_element : 1"  # scripted group (container) (typed FeaturePython)
  n = 1
  ref = Ne_element
FEATURE [App::DocumentObjectGroupPython] G4_Ne  # scripted group (container) (typed FeaturePython)
  Dunit = g/cm3
  Dvalue = 0.000838505
  Group = -> [Ne_element001]
  conduct = 2
  density = 1
  expand = 3
  formula = Ne
  name = G4_Ne
  specific = 4
FEATURE [App::DocumentObjectGroupPython] Na_element020  label="Na_element : 005"  # scripted group (container) (typed FeaturePython)
  n = 1
  ref = Na_element
FEATURE [App::DocumentObjectGroupPython] G4_Na  # scripted group (container) (typed FeaturePython)
  Dunit = g/cm3
  Dvalue = 0.971
  Group = -> [Na_element020]
  conduct = 2
  density = 1
  expand = 3
  formula = Na
  name = G4_Na
  specific = 4
FEATURE [App::DocumentObjectGroupPython] Mg_element011  label="Mg_element : 005"  # scripted group (container) (typed FeaturePython)
  n = 1
  ref = Mg_element
FEATURE [App::DocumentObjectGroupPython] G4_Mg  # scripted group (container) (typed FeaturePython)
  Dunit = g/cm3
  Dvalue = 1.74
  Group = -> [Mg_element011]
  conduct = 2
  density = 1
  expand = 3
  formula = Mg
  name = G4_Mg
  specific = 4
FEATURE [App::DocumentObjectGroupPython] Al_element004  label="Al_element : 1"  # scripted group (container) (typed FeaturePython)
  n = 1
  ref = Al_element
FEATURE [App::DocumentObjectGroupPython] G4_Al  # scripted group (container) (typed FeaturePython)
  Dunit = g/cm3
  Dvalue = 2.699
  Group = -> [Al_element004]
  conduct = 2
  density = 1
  expand = 3
  formula = Al
  name = G4_Al
  specific = 4
FEATURE [App::DocumentObjectGroupPython] Si_element007  label="Si_element : 002"  # scripted group (container) (typed FeaturePython)
  n = 1
  ref = Si_element
FEATURE [App::DocumentObjectGroupPython] G4_Si  # scripted group (container) (typed FeaturePython)
  Dunit = g/cm3
  Dvalue = 2.33
  Group = -> [Si_element007]
  conduct = 2
  density = 1
  expand = 3
  formula = Si
  name = G4_Si
  specific = 4
FEATURE [App::DocumentObjectGroupPython] P_element013  label="P_element : 002"  # scripted group (container) (typed FeaturePython)
  n = 1
  ref = P_element
FEATURE [App::DocumentObjectGroupPython] G4_P  # scripted group (container) (typed FeaturePython)
  Dunit = g/cm3
  Dvalue = 2.2
  Group = -> [P_element013]
  conduct = 2
  density = 1
  expand = 3
  formula = P
  name = G4_P
  specific = 4
FEATURE [App::DocumentObjectGroupPython] S_element023  label="S_element : 007"  # scripted group (container) (typed FeaturePython)
  n = 1
  ref = S_element
FEATURE [App::DocumentObjectGroupPython] G4_S  # scripted group (container) (typed FeaturePython)
  Dunit = g/cm3
  Dvalue = 2
  Group = -> [S_element023]
  conduct = 2
  density = 1
  expand = 3
  formula = S
  name = G4_S
  specific = 4
FEATURE [App::DocumentObjectGroupPython] Cl_element029  label="Cl_element : 015"  # scripted group (container) (typed FeaturePython)
  n = 1
  ref = Cl_element
FEATURE [App::DocumentObjectGroupPython] G4_Cl  # scripted group (container) (typed FeaturePython)
  Dunit = g/cm3
  Dvalue = 0.00299473
  Group = -> [Cl_element029]
  conduct = 2
  density = 1
  expand = 3
  formula = Cl
  name = G4_Cl
  specific = 4
FEATURE [App::DocumentObjectGroupPython] Ar_element002  label="Ar_element : 1"  # scripted group (container) (typed FeaturePython)
  n = 1
  ref = Ar_element
FEATURE [App::DocumentObjectGroupPython] G4_Ar  # scripted group (container) (typed FeaturePython)
  Dunit = g/cm3
  Dvalue = 0.00166201
  Group = -> [Ar_element002]
  conduct = 2
  density = 1
  expand = 3
  formula = Ar
  name = G4_Ar
  specific = 4
FEATURE [App::DocumentObjectGroupPython] K_element013  label="K_element : 003"  # scripted group (container) (typed FeaturePython)
  n = 1
  ref = K_element
FEATURE [App::DocumentObjectGroupPython] G4_K  # scripted group (container) (typed FeaturePython)
  Dunit = g/cm3
  Dvalue = 0.862
  Group = -> [K_element013]
  conduct = 2
  density = 1
  expand = 3
  formula = K
  name = G4_K
  specific = 4
FEATURE [App::DocumentObjectGroupPython] Ca_element014  label="Ca_element : 007"  # scripted group (container) (typed FeaturePython)
  n = 1
  ref = Ca_element
FEATURE [App::DocumentObjectGroupPython] G4_Ca  # scripted group (container) (typed FeaturePython)
  Dunit = g/cm3
  Dvalue = 1.55
  Group = -> [Ca_element014]
  conduct = 2
  density = 1
  expand = 3
  formula = Ca
  name = G4_Ca
  specific = 4
FEATURE [App::DocumentObjectGroupPython] Sc_element001  label="Sc_element : 1"  # scripted group (container) (typed FeaturePython)
  n = 1
  ref = Sc_element
FEATURE [App::DocumentObjectGroupPython] G4_Sc  # scripted group (container) (typed FeaturePython)
  Dunit = g/cm3
  Dvalue = 2.989
  Group = -> [Sc_element001]
  conduct = 2
  density = 1
  expand = 3
  formula = Sc
  name = G4_Sc
  specific = 4
FEATURE [App::DocumentObjectGroupPython] Ti_element004  label="Ti_element : 002"  # scripted group (container) (typed FeaturePython)
  n = 1
  ref = Ti_element
FEATURE [App::DocumentObjectGroupPython] G4_Ti  # scripted group (container) (typed FeaturePython)
  Dunit = g/cm3
  Dvalue = 4.54
  Group = -> [Ti_element004]
  conduct = 2
  density = 1
  expand = 3
  formula = Ti
  name = G4_Ti
  specific = 4
FEATURE [App::DocumentObjectGroupPython] V_element001  label="V_element : 1"  # scripted group (container) (typed FeaturePython)
  n = 1
  ref = V_element
FEATURE [App::DocumentObjectGroupPython] G4_V  # scripted group (container) (typed FeaturePython)
  Dunit = g/cm3
  Dvalue = 6.11
  Group = -> [V_element001]
  conduct = 2
  density = 1
  expand = 3
  formula = V
  name = G4_V
  specific = 4
FEATURE [App::DocumentObjectGroupPython] Cr_element001  label="Cr_element : 1"  # scripted group (container) (typed FeaturePython)
  n = 1
  ref = Cr_element
FEATURE [App::DocumentObjectGroupPython] G4_Cr  # scripted group (container) (typed FeaturePython)
  Dunit = g/cm3
  Dvalue = 7.18
  Group = -> [Cr_element001]
  conduct = 2
  density = 1
  expand = 3
  formula = Cr
  name = G4_Cr
  specific = 4
FEATURE [App::DocumentObjectGroupPython] Mn_element001  label="Mn_element : 1"  # scripted group (container) (typed FeaturePython)
  n = 1
  ref = Mn_element
FEATURE [App::DocumentObjectGroupPython] G4_Mn  # scripted group (container) (typed FeaturePython)
  Dunit = g/cm3
  Dvalue = 7.44
  Group = -> [Mn_element001]
  conduct = 2
  density = 1
  expand = 3
  formula = Mn
  name = G4_Mn
  specific = 4
FEATURE [App::DocumentObjectGroupPython] Fe_element007  label="Fe_element : 004"  # scripted group (container) (typed FeaturePython)
  n = 1
  ref = Fe_element
FEATURE [App::DocumentObjectGroupPython] G4_Fe  # scripted group (container) (typed FeaturePython)
  Dunit = g/cm3
  Dvalue = 7.874
  Group = -> [Fe_element007]
  conduct = 2
  density = 1
  expand = 3
  formula = Fe
  name = G4_Fe
  specific = 4
FEATURE [App::DocumentObjectGroupPython] Co_element001  label="Co_element : 1"  # scripted group (container) (typed FeaturePython)
  n = 1
  ref = Co_element
FEATURE [App::DocumentObjectGroupPython] G4_Co  # scripted group (container) (typed FeaturePython)
  Dunit = g/cm3
  Dvalue = 8.9
  Group = -> [Co_element001]
  conduct = 2
  density = 1
  expand = 3
  formula = Co
  name = G4_Co
  specific = 4
FEATURE [App::DocumentObjectGroupPython] Ni_element001  label="Ni_element : 1"  # scripted group (container) (typed FeaturePython)
  n = 1
  ref = Ni_element
FEATURE [App::DocumentObjectGroupPython] G4_Ni  # scripted group (container) (typed FeaturePython)
  Dunit = g/cm3
  Dvalue = 8.902
  Group = -> [Ni_element001]
  conduct = 2
  density = 1
  expand = 3
  formula = Ni
  name = G4_Ni
  specific = 4
FEATURE [App::DocumentObjectGroupPython] Cu_element001  label="Cu_element : 1"  # scripted group (container) (typed FeaturePython)
  n = 1
  ref = Cu_element
FEATURE [App::DocumentObjectGroupPython] G4_Cu  # scripted group (container) (typed FeaturePython)
  Dunit = g/cm3
  Dvalue = 8.96
  Group = -> [Cu_element001]
  conduct = 2
  density = 1
  expand = 3
  formula = Cu
  name = G4_Cu
  specific = 4
FEATURE [App::DocumentObjectGroupPython] Zn_element001  label="Zn_element : 1"  # scripted group (container) (typed FeaturePython)
  n = 1
  ref = Zn_element
FEATURE [App::DocumentObjectGroupPython] G4_Zn  # scripted group (container) (typed FeaturePython)
  Dunit = g/cm3
  Dvalue = 7.133
  Group = -> [Zn_element001]
  conduct = 2
  density = 1
  expand = 3
  formula = Zn
  name = G4_Zn
  specific = 4
FEATURE [App::DocumentObjectGroupPython] Ga_element002  label="Ga_element : 002"  # scripted group (container) (typed FeaturePython)
  n = 1
  ref = Ga_element
FEATURE [App::DocumentObjectGroupPython] G4_Ga  # scripted group (container) (typed FeaturePython)
  Dunit = g/cm3
  Dvalue = 5.904
  Group = -> [Ga_element002]
  conduct = 2
  density = 1
  expand = 3
  formula = Ga
  name = G4_Ga
  specific = 4
FEATURE [App::DocumentObjectGroupPython] Ge_element002  label="Ge_element : 1"  # scripted group (container) (typed FeaturePython)
  n = 1
  ref = Ge_element
FEATURE [App::DocumentObjectGroupPython] G4_Ge  # scripted group (container) (typed FeaturePython)
  Dunit = g/cm3
  Dvalue = 5.323
  Group = -> [Ge_element002]
  conduct = 2
  density = 1
  expand = 3
  formula = Ge
  name = G4_Ge
  specific = 4
FEATURE [App::DocumentObjectGroupPython] As_element003  label="As_element : 002"  # scripted group (container) (typed FeaturePython)
  n = 1
  ref = As_element
FEATURE [App::DocumentObjectGroupPython] G4_As  # scripted group (container) (typed FeaturePython)
  Dunit = g/cm3
  Dvalue = 5.73
  Group = -> [As_element003]
  conduct = 2
  density = 1
  expand = 3
  formula = As
  name = G4_As
  specific = 4
FEATURE [App::DocumentObjectGroupPython] Se_element001  label="Se_element : 1"  # scripted group (container) (typed FeaturePython)
  n = 1
  ref = Se_element
FEATURE [App::DocumentObjectGroupPython] G4_Se  # scripted group (container) (typed FeaturePython)
  Dunit = g/cm3
  Dvalue = 4.5
  Group = -> [Se_element001]
  conduct = 2
  density = 1
  expand = 3
  formula = Se
  name = G4_Se
  specific = 4
FEATURE [App::DocumentObjectGroupPython] Br_element007  label="Br_element : 004"  # scripted group (container) (typed FeaturePython)
  n = 1
  ref = Br_element
FEATURE [App::DocumentObjectGroupPython] G4_Br  # scripted group (container) (typed FeaturePython)
  Dunit = g/cm3
  Dvalue = 0.0070721
  Group = -> [Br_element007]
  conduct = 2
  density = 1
  expand = 3
  formula = Br
  name = G4_Br
  specific = 4
FEATURE [App::DocumentObjectGroupPython] Kr_element001  label="Kr_element : 1"  # scripted group (container) (typed FeaturePython)
  n = 1
  ref = Kr_element
FEATURE [App::DocumentObjectGroupPython] G4_Kr  # scripted group (container) (typed FeaturePython)
  Dunit = g/cm3
  Dvalue = 0.00347832
  Group = -> [Kr_element001]
  conduct = 2
  density = 1
  expand = 3
  formula = Kr
  name = G4_Kr
  specific = 4
FEATURE [App::DocumentObjectGroupPython] Rb_element001  label="Rb_element : 1"  # scripted group (container) (typed FeaturePython)
  n = 1
  ref = Rb_element
FEATURE [App::DocumentObjectGroupPython] G4_Rb  # scripted group (container) (typed FeaturePython)
  Dunit = g/cm3
  Dvalue = 1.532
  Group = -> [Rb_element001]
  conduct = 2
  density = 1
  expand = 3
  formula = Rb
  name = G4_Rb
  specific = 4
FEATURE [App::DocumentObjectGroupPython] Sr_element001  label="Sr_element : 1"  # scripted group (container) (typed FeaturePython)
  n = 1
  ref = Sr_element
FEATURE [App::DocumentObjectGroupPython] G4_Sr  # scripted group (container) (typed FeaturePython)
  Dunit = g/cm3
  Dvalue = 2.54
  Group = -> [Sr_element001]
  conduct = 2
  density = 1
  expand = 3
  formula = Sr
  name = G4_Sr
  specific = 4
FEATURE [App::DocumentObjectGroupPython] Y_element001  label="Y_element : 1"  # scripted group (container) (typed FeaturePython)
  n = 1
  ref = Y_element
FEATURE [App::DocumentObjectGroupPython] G4_Y  # scripted group (container) (typed FeaturePython)
  Dunit = g/cm3
  Dvalue = 4.469
  Group = -> [Y_element001]
  conduct = 2
  density = 1
  expand = 3
  formula = Y
  name = G4_Y
  specific = 4
FEATURE [App::DocumentObjectGroupPython] Zr_element001  label="Zr_element : 1"  # scripted group (container) (typed FeaturePython)
  n = 1
  ref = Zr_element
FEATURE [App::DocumentObjectGroupPython] G4_Zr  # scripted group (container) (typed FeaturePython)
  Dunit = g/cm3
  Dvalue = 6.506
  Group = -> [Zr_element001]
  conduct = 2
  density = 1
  expand = 3
  formula = Zr
  name = G4_Zr
  specific = 4
FEATURE [App::DocumentObjectGroupPython] Nb_element001  label="Nb_element : 1"  # scripted group (container) (typed FeaturePython)
  n = 1
  ref = Nb_element
FEATURE [App::DocumentObjectGroupPython] G4_Nb  # scripted group (container) (typed FeaturePython)
  Dunit = g/cm3
  Dvalue = 8.57
  Group = -> [Nb_element001]
  conduct = 2
  density = 1
  expand = 3
  formula = Nb
  name = G4_Nb
  specific = 4
FEATURE [App::DocumentObjectGroupPython] Mo_element001  label="Mo_element : 1"  # scripted group (container) (typed FeaturePython)
  n = 1
  ref = Mo_element
FEATURE [App::DocumentObjectGroupPython] G4_Mo  # scripted group (container) (typed FeaturePython)
  Dunit = g/cm3
  Dvalue = 10.22
  Group = -> [Mo_element001]
  conduct = 2
  density = 1
  expand = 3
  formula = Mo
  name = G4_Mo
  specific = 4
FEATURE [App::DocumentObjectGroupPython] Tc_element001  label="Tc_element : 1"  # scripted group (container) (typed FeaturePython)
  n = 1
  ref = Tc_element
FEATURE [App::DocumentObjectGroupPython] G4_Tc  # scripted group (container) (typed FeaturePython)
  Dunit = g/cm3
  Dvalue = 11.5
  Group = -> [Tc_element001]
  conduct = 2
  density = 1
  expand = 3
  formula = Tc
  name = G4_Tc
  specific = 4
FEATURE [App::DocumentObjectGroupPython] Ru_element001  label="Ru_element : 1"  # scripted group (container) (typed FeaturePython)
  n = 1
  ref = Ru_element
FEATURE [App::DocumentObjectGroupPython] G4_Ru  # scripted group (container) (typed FeaturePython)
  Dunit = g/cm3
  Dvalue = 12.41
  Group = -> [Ru_element001]
  conduct = 2
  density = 1
  expand = 3
  formula = Ru
  name = G4_Ru
  specific = 4
FEATURE [App::DocumentObjectGroupPython] Rh_element001  label="Rh_element : 1"  # scripted group (container) (typed FeaturePython)
  n = 1
  ref = Rh_element
FEATURE [App::DocumentObjectGroupPython] G4_Rh  # scripted group (container) (typed FeaturePython)
  Dunit = g/cm3
  Dvalue = 12.41
  Group = -> [Rh_element001]
  conduct = 2
  density = 1
  expand = 3
  formula = Rh
  name = G4_Rh
  specific = 4
FEATURE [App::DocumentObjectGroupPython] Pd_element001  label="Pd_element : 1"  # scripted group (container) (typed FeaturePython)
  n = 1
  ref = Pd_element
FEATURE [App::DocumentObjectGroupPython] G4_Pd  # scripted group (container) (typed FeaturePython)
  Dunit = g/cm3
  Dvalue = 12.02
  Group = -> [Pd_element001]
  conduct = 2
  density = 1
  expand = 3
  formula = Pd
  name = G4_Pd
  specific = 4
FEATURE [App::DocumentObjectGroupPython] Ag_element006  label="Ag_element : 004"  # scripted group (container) (typed FeaturePython)
  n = 1
  ref = Ag_element
FEATURE [App::DocumentObjectGroupPython] G4_Ag  # scripted group (container) (typed FeaturePython)
  Dunit = g/cm3
  Dvalue = 10.5
  Group = -> [Ag_element006]
  conduct = 2
  density = 1
  expand = 3
  formula = Ag
  name = G4_Ag
  specific = 4
FEATURE [App::DocumentObjectGroupPython] Cd_element003  label="Cd_element : 003"  # scripted group (container) (typed FeaturePython)
  n = 1
  ref = Cd_element
FEATURE [App::DocumentObjectGroupPython] G4_Cd  # scripted group (container) (typed FeaturePython)
  Dunit = g/cm3
  Dvalue = 8.65
  Group = -> [Cd_element003]
  conduct = 2
  density = 1
  expand = 3
  formula = Cd
  name = G4_Cd
  specific = 4
FEATURE [App::DocumentObjectGroupPython] In_element001  label="In_element : 1"  # scripted group (container) (typed FeaturePython)
  n = 1
  ref = In_element
FEATURE [App::DocumentObjectGroupPython] G4_In  # scripted group (container) (typed FeaturePython)
  Dunit = g/cm3
  Dvalue = 7.31
  Group = -> [In_element001]
  conduct = 2
  density = 1
  expand = 3
  formula = In
  name = G4_In
  specific = 4
FEATURE [App::DocumentObjectGroupPython] Sn_element001  label="Sn_element : 1"  # scripted group (container) (typed FeaturePython)
  n = 1
  ref = Sn_element
FEATURE [App::DocumentObjectGroupPython] G4_Sn  # scripted group (container) (typed FeaturePython)
  Dunit = g/cm3
  Dvalue = 7.31
  Group = -> [Sn_element001]
  conduct = 2
  density = 1
  expand = 3
  formula = Sn
  name = G4_Sn
  specific = 4
FEATURE [App::DocumentObjectGroupPython] Sb_element001  label="Sb_element : 1"  # scripted group (container) (typed FeaturePython)
  n = 1
  ref = Sb_element
FEATURE [App::DocumentObjectGroupPython] G4_Sb  # scripted group (container) (typed FeaturePython)
  Dunit = g/cm3
  Dvalue = 6.691
  Group = -> [Sb_element001]
  conduct = 2
  density = 1
  expand = 3
  formula = Sb
  name = G4_Sb
  specific = 4
FEATURE [App::DocumentObjectGroupPython] Te_element002  label="Te_element : 002"  # scripted group (container) (typed FeaturePython)
  n = 1
  ref = Te_element
FEATURE [App::DocumentObjectGroupPython] G4_Te  # scripted group (container) (typed FeaturePython)
  Dunit = g/cm3
  Dvalue = 6.24
  Group = -> [Te_element002]
  conduct = 2
  density = 1
  expand = 3
  formula = Te
  name = G4_Te
  specific = 4
FEATURE [App::DocumentObjectGroupPython] I_element010  label="I_element : 006"  # scripted group (container) (typed FeaturePython)
  n = 1
  ref = I_element
FEATURE [App::DocumentObjectGroupPython] G4_I  # scripted group (container) (typed FeaturePython)
  Dunit = g/cm3
  Dvalue = 4.93
  Group = -> [I_element010]
  conduct = 2
  density = 1
  expand = 3
  formula = I
  name = G4_I
  specific = 4
FEATURE [App::DocumentObjectGroupPython] Xe_element001  label="Xe_element : 1"  # scripted group (container) (typed FeaturePython)
  n = 1
  ref = Xe_element
FEATURE [App::DocumentObjectGroupPython] G4_Xe  # scripted group (container) (typed FeaturePython)
  Dunit = g/cm3
  Dvalue = 0.00548536
  Group = -> [Xe_element001]
  conduct = 2
  density = 1
  expand = 3
  formula = Xe
  name = G4_Xe
  specific = 4
FEATURE [App::DocumentObjectGroupPython] Cs_element003  label="Cs_element : 003"  # scripted group (container) (typed FeaturePython)
  n = 1
  ref = Cs_element
FEATURE [App::DocumentObjectGroupPython] G4_Cs  # scripted group (container) (typed FeaturePython)
  Dunit = g/cm3
  Dvalue = 1.873
  Group = -> [Cs_element003]
  conduct = 2
  density = 1
  expand = 3
  formula = Cs
  name = G4_Cs
  specific = 4
FEATURE [App::DocumentObjectGroupPython] Ba_element003  label="Ba_element : 003"  # scripted group (container) (typed FeaturePython)
  n = 1
  ref = Ba_element
FEATURE [App::DocumentObjectGroupPython] G4_Ba  # scripted group (container) (typed FeaturePython)
  Dunit = g/cm3
  Dvalue = 3.5
  Group = -> [Ba_element003]
  conduct = 2
  density = 1
  expand = 3
  formula = Ba
  name = G4_Ba
  specific = 4
FEATURE [App::DocumentObjectGroupPython] La_element003  label="La_element : 003"  # scripted group (container) (typed FeaturePython)
  n = 1
  ref = La_element
FEATURE [App::DocumentObjectGroupPython] G4_La  # scripted group (container) (typed FeaturePython)
  Dunit = g/cm3
  Dvalue = 6.154
  Group = -> [La_element003]
  conduct = 2
  density = 1
  expand = 3
  formula = La
  name = G4_La
  specific = 4
FEATURE [App::DocumentObjectGroupPython] Ce_element002  label="Ce_element : 1"  # scripted group (container) (typed FeaturePython)
  n = 1
  ref = Ce_element
FEATURE [App::DocumentObjectGroupPython] G4_Ce  # scripted group (container) (typed FeaturePython)
  Dunit = g/cm3
  Dvalue = 6.657
  Group = -> [Ce_element002]
  conduct = 2
  density = 1
  expand = 3
  formula = Ce
  name = G4_Ce
  specific = 4
FEATURE [App::DocumentObjectGroupPython] Pr_element001  label="Pr_element : 1"  # scripted group (container) (typed FeaturePython)
  n = 1
  ref = Pr_element
FEATURE [App::DocumentObjectGroupPython] G4_Pr  # scripted group (container) (typed FeaturePython)
  Dunit = g/cm3
  Dvalue = 6.71
  Group = -> [Pr_element001]
  conduct = 2
  density = 1
  expand = 3
  formula = Pr
  name = G4_Pr
  specific = 4
FEATURE [App::DocumentObjectGroupPython] Nd_element001  label="Nd_element : 1"  # scripted group (container) (typed FeaturePython)
  n = 1
  ref = Nd_element
FEATURE [App::DocumentObjectGroupPython] G4_Nd  # scripted group (container) (typed FeaturePython)
  Dunit = g/cm3
  Dvalue = 6.9
  Group = -> [Nd_element001]
  conduct = 2
  density = 1
  expand = 3
  formula = Nd
  name = G4_Nd
  specific = 4
FEATURE [App::DocumentObjectGroupPython] Pm_element001  label="Pm_element : 1"  # scripted group (container) (typed FeaturePython)
  n = 1
  ref = Pm_element
FEATURE [App::DocumentObjectGroupPython] G4_Pm  # scripted group (container) (typed FeaturePython)
  Dunit = g/cm3
  Dvalue = 7.22
  Group = -> [Pm_element001]
  conduct = 2
  density = 1
  expand = 3
  formula = Pm
  name = G4_Pm
  specific = 4
FEATURE [App::DocumentObjectGroupPython] Sm_element001  label="Sm_element : 1"  # scripted group (container) (typed FeaturePython)
  n = 1
  ref = Sm_element
FEATURE [App::DocumentObjectGroupPython] G4_Sm  # scripted group (container) (typed FeaturePython)
  Dunit = g/cm3
  Dvalue = 7.46
  Group = -> [Sm_element001]
  conduct = 2
  density = 1
  expand = 3
  formula = Sm
  name = G4_Sm
  specific = 4
FEATURE [App::DocumentObjectGroupPython] Eu_element001  label="Eu_element : 1"  # scripted group (container) (typed FeaturePython)
  n = 1
  ref = Eu_element
FEATURE [App::DocumentObjectGroupPython] G4_Eu  # scripted group (container) (typed FeaturePython)
  Dunit = g/cm3
  Dvalue = 5.243
  Group = -> [Eu_element001]
  conduct = 2
  density = 1
  expand = 3
  formula = Eu
  name = G4_Eu
  specific = 4
FEATURE [App::DocumentObjectGroupPython] Gd_element002  label="Gd_element : 1"  # scripted group (container) (typed FeaturePython)
  n = 1
  ref = Gd_element
FEATURE [App::DocumentObjectGroupPython] G4_Gd  # scripted group (container) (typed FeaturePython)
  Dunit = g/cm3
  Dvalue = 7.9004
  Group = -> [Gd_element002]
  conduct = 2
  density = 1
  expand = 3
  formula = Gd
  name = G4_Gd
  specific = 4
FEATURE [App::DocumentObjectGroupPython] Tb_element001  label="Tb_element : 1"  # scripted group (container) (typed FeaturePython)
  n = 1
  ref = Tb_element
FEATURE [App::DocumentObjectGroupPython] G4_Tb  # scripted group (container) (typed FeaturePython)
  Dunit = g/cm3
  Dvalue = 8.229
  Group = -> [Tb_element001]
  conduct = 2
  density = 1
  expand = 3
  formula = Tb
  name = G4_Tb
  specific = 4
FEATURE [App::DocumentObjectGroupPython] Dy_element001  label="Dy_element : 1"  # scripted group (container) (typed FeaturePython)
  n = 1
  ref = Dy_element
FEATURE [App::DocumentObjectGroupPython] G4_Dy  # scripted group (container) (typed FeaturePython)
  Dunit = g/cm3
  Dvalue = 8.55
  Group = -> [Dy_element001]
  conduct = 2
  density = 1
  expand = 3
  formula = Dy
  name = G4_Dy
  specific = 4
FEATURE [App::DocumentObjectGroupPython] Ho_element001  label="Ho_element : 1"  # scripted group (container) (typed FeaturePython)
  n = 1
  ref = Ho_element
FEATURE [App::DocumentObjectGroupPython] G4_Ho  # scripted group (container) (typed FeaturePython)
  Dunit = g/cm3
  Dvalue = 8.795
  Group = -> [Ho_element001]
  conduct = 2
  density = 1
  expand = 3
  formula = Ho
  name = G4_Ho
  specific = 4
FEATURE [App::DocumentObjectGroupPython] Er_element001  label="Er_element : 1"  # scripted group (container) (typed FeaturePython)
  n = 1
  ref = Er_element
FEATURE [App::DocumentObjectGroupPython] G4_Er  # scripted group (container) (typed FeaturePython)
  Dunit = g/cm3
  Dvalue = 9.066
  Group = -> [Er_element001]
  conduct = 2
  density = 1
  expand = 3
  formula = Er
  name = G4_Er
  specific = 4
FEATURE [App::DocumentObjectGroupPython] Tm_element001  label="Tm_element : 1"  # scripted group (container) (typed FeaturePython)
  n = 1
  ref = Tm_element
FEATURE [App::DocumentObjectGroupPython] G4_Tm  # scripted group (container) (typed FeaturePython)
  Dunit = g/cm3
  Dvalue = 9.321
  Group = -> [Tm_element001]
  conduct = 2
  density = 1
  expand = 3
  formula = Tm
  name = G4_Tm
  specific = 4
FEATURE [App::DocumentObjectGroupPython] Yb_element001  label="Yb_element : 1"  # scripted group (container) (typed FeaturePython)
  n = 1
  ref = Yb_element
FEATURE [App::DocumentObjectGroupPython] G4_Yb  # scripted group (container) (typed FeaturePython)
  Dunit = g/cm3
  Dvalue = 6.73
  Group = -> [Yb_element001]
  conduct = 2
  density = 1
  expand = 3
  formula = Yb
  name = G4_Yb
  specific = 4
FEATURE [App::DocumentObjectGroupPython] Lu_element001  label="Lu_element : 1"  # scripted group (container) (typed FeaturePython)
  n = 1
  ref = Lu_element
FEATURE [App::DocumentObjectGroupPython] G4_Lu  # scripted group (container) (typed FeaturePython)
  Dunit = g/cm3
  Dvalue = 9.84
  Group = -> [Lu_element001]
  conduct = 2
  density = 1
  expand = 3
  formula = Lu
  name = G4_Lu
  specific = 4
FEATURE [App::DocumentObjectGroupPython] Hf_element001  label="Hf_element : 1"  # scripted group (container) (typed FeaturePython)
  n = 1
  ref = Hf_element
FEATURE [App::DocumentObjectGroupPython] G4_Hf  # scripted group (container) (typed FeaturePython)
  Dunit = g/cm3
  Dvalue = 13.31
  Group = -> [Hf_element001]
  conduct = 2
  density = 1
  expand = 3
  formula = Hf
  name = G4_Hf
  specific = 4
FEATURE [App::DocumentObjectGroupPython] Ta_element001  label="Ta_element : 1"  # scripted group (container) (typed FeaturePython)
  n = 1
  ref = Ta_element
FEATURE [App::DocumentObjectGroupPython] G4_Ta  # scripted group (container) (typed FeaturePython)
  Dunit = g/cm3
  Dvalue = 16.654
  Group = -> [Ta_element001]
  conduct = 2
  density = 1
  expand = 3
  formula = Ta
  name = G4_Ta
  specific = 4
FEATURE [App::DocumentObjectGroupPython] W_element004  label="W_element : 004"  # scripted group (container) (typed FeaturePython)
  n = 1
  ref = W_element
FEATURE [App::DocumentObjectGroupPython] G4_W  # scripted group (container) (typed FeaturePython)
  Dunit = g/cm3
  Dvalue = 19.3
  Group = -> [W_element004]
  conduct = 2
  density = 1
  expand = 3
  formula = W
  name = G4_W
  specific = 4
FEATURE [App::DocumentObjectGroupPython] Re_element001  label="Re_element : 1"  # scripted group (container) (typed FeaturePython)
  n = 1
  ref = Re_element
FEATURE [App::DocumentObjectGroupPython] G4_Re  # scripted group (container) (typed FeaturePython)
  Dunit = g/cm3
  Dvalue = 21.02
  Group = -> [Re_element001]
  conduct = 2
  density = 1
  expand = 3
  formula = Re
  name = G4_Re
  specific = 4
FEATURE [App::DocumentObjectGroupPython] Os_element001  label="Os_element : 1"  # scripted group (container) (typed FeaturePython)
  n = 1
  ref = Os_element
FEATURE [App::DocumentObjectGroupPython] G4_Os  # scripted group (container) (typed FeaturePython)
  Dunit = g/cm3
  Dvalue = 22.57
  Group = -> [Os_element001]
  conduct = 2
  density = 1
  expand = 3
  formula = Os
  name = G4_Os
  specific = 4
FEATURE [App::DocumentObjectGroupPython] Ir_element001  label="Ir_element : 1"  # scripted group (container) (typed FeaturePython)
  n = 1
  ref = Ir_element
FEATURE [App::DocumentObjectGroupPython] G4_Ir  # scripted group (container) (typed FeaturePython)
  Dunit = g/cm3
  Dvalue = 22.42
  Group = -> [Ir_element001]
  conduct = 2
  density = 1
  expand = 3
  formula = Ir
  name = G4_Ir
  specific = 4
FEATURE [App::DocumentObjectGroupPython] Pt_element001  label="Pt_element : 1"  # scripted group (container) (typed FeaturePython)
  n = 1
  ref = Pt_element
FEATURE [App::DocumentObjectGroupPython] G4_Pt  # scripted group (container) (typed FeaturePython)
  Dunit = g/cm3
  Dvalue = 21.45
  Group = -> [Pt_element001]
  conduct = 2
  density = 1
  expand = 3
  formula = Pt
  name = G4_Pt
  specific = 4
FEATURE [App::DocumentObjectGroupPython] Au_element001  label="Au_element : 1"  # scripted group (container) (typed FeaturePython)
  n = 1
  ref = Au_element
FEATURE [App::DocumentObjectGroupPython] G4_Au  # scripted group (container) (typed FeaturePython)
  Dunit = g/cm3
  Dvalue = 19.32
  Group = -> [Au_element001]
  conduct = 2
  density = 1
  expand = 3
  formula = Au
  name = G4_Au
  specific = 4
FEATURE [App::DocumentObjectGroupPython] Hg_element002  label="Hg_element : 002"  # scripted group (container) (typed FeaturePython)
  n = 1
  ref = Hg_element
FEATURE [App::DocumentObjectGroupPython] G4_Hg  # scripted group (container) (typed FeaturePython)
  Dunit = g/cm3
  Dvalue = 13.546
  Group = -> [Hg_element002]
  conduct = 2
  density = 1
  expand = 3
  formula = Hg
  name = G4_Hg
  specific = 4
FEATURE [App::DocumentObjectGroupPython] Tl_element002  label="Tl_element : 002"  # scripted group (container) (typed FeaturePython)
  n = 1
  ref = Tl_element
FEATURE [App::DocumentObjectGroupPython] G4_Tl  # scripted group (container) (typed FeaturePython)
  Dunit = g/cm3
  Dvalue = 11.72
  Group = -> [Tl_element002]
  conduct = 2
  density = 1
  expand = 3
  formula = Tl
  name = G4_Tl
  specific = 4
FEATURE [App::DocumentObjectGroupPython] Pb_element003  label="Pb_element : 1"  # scripted group (container) (typed FeaturePython)
  n = 1
  ref = Pb_element
FEATURE [App::DocumentObjectGroupPython] G4_Pb  # scripted group (container) (typed FeaturePython)
  Dunit = g/cm3
  Dvalue = 11.35
  Group = -> [Pb_element003]
  conduct = 2
  density = 1
  expand = 3
  formula = Pb
  name = G4_Pb
  specific = 4
FEATURE [App::DocumentObjectGroupPython] Bi_element002  label="Bi_element : 1"  # scripted group (container) (typed FeaturePython)
  n = 1
  ref = Bi_element
FEATURE [App::DocumentObjectGroupPython] G4_Bi  # scripted group (container) (typed FeaturePython)
  Dunit = g/cm3
  Dvalue = 9.747
  Group = -> [Bi_element002]
  conduct = 2
  density = 1
  expand = 3
  formula = Bi
  name = G4_Bi
  specific = 4
FEATURE [App::DocumentObjectGroupPython] Po_element001  label="Po_element : 1"  # scripted group (container) (typed FeaturePython)
  n = 1
  ref = Po_element
FEATURE [App::DocumentObjectGroupPython] G4_Po  # scripted group (container) (typed FeaturePython)
  Dunit = g/cm3
  Dvalue = 9.32
  Group = -> [Po_element001]
  conduct = 2
  density = 1
  expand = 3
  formula = Po
  name = G4_Po
  specific = 4
FEATURE [App::DocumentObjectGroupPython] At_element001  label="At_element : 1"  # scripted group (container) (typed FeaturePython)
  n = 1
  ref = At_element
FEATURE [App::DocumentObjectGroupPython] G4_At  # scripted group (container) (typed FeaturePython)
  Dunit = g/cm3
  Dvalue = 9.32
  Group = -> [At_element001]
  conduct = 2
  density = 1
  expand = 3
  formula = At
  name = G4_At
  specific = 4
FEATURE [App::DocumentObjectGroupPython] Rn_element001  label="Rn_element : 1"  # scripted group (container) (typed FeaturePython)
  n = 1
  ref = Rn_element
FEATURE [App::DocumentObjectGroupPython] G4_Rn  # scripted group (container) (typed FeaturePython)
  Dunit = g/cm3
  Dvalue = 0.00900662
  Group = -> [Rn_element001]
  conduct = 2
  density = 1
  expand = 3
  formula = Rn
  name = G4_Rn
  specific = 4
FEATURE [App::DocumentObjectGroupPython] Fr_element001  label="Fr_element : 1"  # scripted group (container) (typed FeaturePython)
  n = 1
  ref = Fr_element
FEATURE [App::DocumentObjectGroupPython] G4_Fr  # scripted group (container) (typed FeaturePython)
  Dunit = g/cm3
  Dvalue = 1
  Group = -> [Fr_element001]
  conduct = 2
  density = 1
  expand = 3
  formula = Fr
  name = G4_Fr
  specific = 4
FEATURE [App::DocumentObjectGroupPython] Ra_element001  label="Ra_element : 1"  # scripted group (container) (typed FeaturePython)
  n = 1
  ref = Ra_element
FEATURE [App::DocumentObjectGroupPython] G4_Ra  # scripted group (container) (typed FeaturePython)
  Dunit = g/cm3
  Dvalue = 5
  Group = -> [Ra_element001]
  conduct = 2
  density = 1
  expand = 3
  formula = Ra
  name = G4_Ra
  specific = 4
FEATURE [App::DocumentObjectGroupPython] Ac_element001  label="Ac_element : 1"  # scripted group (container) (typed FeaturePython)
  n = 1
  ref = Ac_element
FEATURE [App::DocumentObjectGroupPython] G4_Ac  # scripted group (container) (typed FeaturePython)
  Dunit = g/cm3
  Dvalue = 10.07
  Group = -> [Ac_element001]
  conduct = 2
  density = 1
  expand = 3
  formula = Ac
  name = G4_Ac
  specific = 4
FEATURE [App::DocumentObjectGroupPython] Th_element001  label="Th_element : 1"  # scripted group (container) (typed FeaturePython)
  n = 1
  ref = Th_element
FEATURE [App::DocumentObjectGroupPython] G4_Th  # scripted group (container) (typed FeaturePython)
  Dunit = g/cm3
  Dvalue = 11.72
  Group = -> [Th_element001]
  conduct = 2
  density = 1
  expand = 3
  formula = Th
  name = G4_Th
  specific = 4
FEATURE [App::DocumentObjectGroupPython] Pa_element001  label="Pa_element : 1"  # scripted group (container) (typed FeaturePython)
  n = 1
  ref = Pa_element
FEATURE [App::DocumentObjectGroupPython] G4_Pa  # scripted group (container) (typed FeaturePython)
  Dunit = g/cm3
  Dvalue = 15.37
  Group = -> [Pa_element001]
  conduct = 2
  density = 1
  expand = 3
  formula = Pa
  name = G4_Pa
  specific = 4
FEATURE [App::DocumentObjectGroupPython] U_element004  label="U_element : 004"  # scripted group (container) (typed FeaturePython)
  n = 1
  ref = U_element
FEATURE [App::DocumentObjectGroupPython] G4_U  # scripted group (container) (typed FeaturePython)
  Dunit = g/cm3
  Dvalue = 18.95
  Group = -> [U_element004]
  conduct = 2
  density = 1
  expand = 3
  formula = U
  name = G4_U
  specific = 4
FEATURE [App::DocumentObjectGroupPython] Np_element001  label="Np_element : 1"  # scripted group (container) (typed FeaturePython)
  n = 1
  ref = Np_element
FEATURE [App::DocumentObjectGroupPython] G4_Np  # scripted group (container) (typed FeaturePython)
  Dunit = g/cm3
  Dvalue = 20.25
  Group = -> [Np_element001]
  conduct = 2
  density = 1
  expand = 3
  formula = Np
  name = G4_Np
  specific = 4
FEATURE [App::DocumentObjectGroupPython] Pu_element002  label="Pu_element : 002"  # scripted group (container) (typed FeaturePython)
  n = 1
  ref = Pu_element
FEATURE [App::DocumentObjectGroupPython] G4_Pu  # scripted group (container) (typed FeaturePython)
  Dunit = g/cm3
  Dvalue = 19.84
  Group = -> [Pu_element002]
  conduct = 2
  density = 1
  expand = 3
  formula = Pu
  name = G4_Pu
  specific = 4
FEATURE [App::DocumentObjectGroupPython] Am_element001  label="Am_element : 1"  # scripted group (container) (typed FeaturePython)
  n = 1
  ref = Am_element
FEATURE [App::DocumentObjectGroupPython] G4_Am  # scripted group (container) (typed FeaturePython)
  Dunit = g/cm3
  Dvalue = 13.67
  Group = -> [Am_element001]
  conduct = 2
  density = 1
  expand = 3
  formula = Am
  name = G4_Am
  specific = 4
FEATURE [App::DocumentObjectGroupPython] Cm_element001  label="Cm_element : 1"  # scripted group (container) (typed FeaturePython)
  n = 1
  ref = Cm_element
FEATURE [App::DocumentObjectGroupPython] G4_Cm  # scripted group (container) (typed FeaturePython)
  Dunit = g/cm3
  Dvalue = 13.51
  Group = -> [Cm_element001]
  conduct = 2
  density = 1
  expand = 3
  formula = Cm
  name = G4_Cm
  specific = 4
FEATURE [App::DocumentObjectGroupPython] Bk_element001  label="Bk_element : 1"  # scripted group (container) (typed FeaturePython)
  n = 1
  ref = Bk_element
FEATURE [App::DocumentObjectGroupPython] G4_Bk  # scripted group (container) (typed FeaturePython)
  Dunit = g/cm3
  Dvalue = 14
  Group = -> [Bk_element001]
  conduct = 2
  density = 1
  expand = 3
  formula = Bk
  name = G4_Bk
  specific = 4
FEATURE [App::DocumentObjectGroupPython] Cf_element001  label="Cf_element : 1"  # scripted group (container) (typed FeaturePython)
  n = 1
  ref = Cf_element
FEATURE [App::DocumentObjectGroupPython] G4_Cf  # scripted group (container) (typed FeaturePython)
  Dunit = g/cm3
  Dvalue = 10
  Group = -> [Cf_element001]
  conduct = 2
  density = 1
  expand = 3
  formula = Cf
  name = G4_Cf
  specific = 4
FEATURE [App::DocumentObjectGroupPython] Element  # scripted group (container) (typed FeaturePython)
  Group = -> [G4_H,G4_He,G4_Li,G4_Be,G4_B,G4_C,G4_N,G4_O,G4_F,G4_Ne,G4_Na,G4_Mg,G4_Al,G4_Si,G4_P,G4_S,G4_Cl,G4_Ar,G4_K,G4_Ca,G4_Sc,G4_Ti,G4_V,G4_Cr,G4_Mn,G4_Fe,G4_Co,G4_Ni,G4_Cu,G4_Zn,G4_Ga,G4_Ge,G4_As,G4_Se,G4_Br,G4_Kr,G4_Rb,G4_Sr,G4_Y,G4_Zr,G4_Nb,G4_Mo,G4_Tc,G4_Ru,G4_Rh,G4_Pd,G4_Ag,G4_Cd,G4_In,G4_Sn,G4_Sb,G4_Te,G4_I,G4_Xe,G4_Cs,G4_Ba,G4_La,G4_Ce,G4_Pr,G4_Nd,G4_Pm,G4_Sm,G4_Eu,G4_Gd,G4_Tb,G4_Dy,G4_Ho,G4_Er,+30 more]
FEATURE [App::DocumentObjectGroupPython] H_element114  label="H_element : 063"  # scripted group (container) (typed FeaturePython)
  n = 2
  ref = H_element
FEATURE [App::DocumentObjectGroupPython] G4_lH2  # scripted group (container) (typed FeaturePython)
  Dunit = g/cm3
  Dvalue = 0.0708
  Group = -> [H_element114]
  conduct = 2
  density = 1
  expand = 3
  formula = G4_lH2
  name = G4_lH2
  specific = 4
FEATURE [App::DocumentObjectGroupPython] N_element049  label="N_element : 022"  # scripted group (container) (typed FeaturePython)
  n = 2
  ref = N_element
FEATURE [App::DocumentObjectGroupPython] G4_lN2  # scripted group (container) (typed FeaturePython)
  Dunit = g/cm3
  Dvalue = 0.807
  Group = -> [N_element049]
  conduct = 2
  density = 1
  expand = 3
  formula = G4_lN2
  name = G4_lN2
  specific = 4
FEATURE [App::DocumentObjectGroupPython] O_element106  label="O_element : 060"  # scripted group (container) (typed FeaturePython)
  n = 2
  ref = O_element
FEATURE [App::DocumentObjectGroupPython] G4_lO2  # scripted group (container) (typed FeaturePython)
  Dunit = g/cm3
  Dvalue = 1.141
  Group = -> [O_element106]
  conduct = 2
  density = 1
  expand = 3
  formula = G4_lO2
  name = G4_lO2
  specific = 4
FEATURE [App::DocumentObjectGroupPython] Ar  label="Ar : 1"  # scripted group (container) (typed FeaturePython)
  n = 1
  ref = Ar
FEATURE [App::DocumentObjectGroupPython] G4_lAr  # scripted group (container) (typed FeaturePython)
  Dunit = g/cm3
  Dvalue = 1.396
  Group = -> [Ar]
  conduct = 2
  density = 1
  expand = 3
  formula = G4_lAr
  name = G4_lAr
  specific = 4
FEATURE [App::DocumentObjectGroupPython] Br  label="Br : 1"  # scripted group (container) (typed FeaturePython)
  n = 1
  ref = Br
FEATURE [App::DocumentObjectGroupPython] G4_lBr  # scripted group (container) (typed FeaturePython)
  Dunit = g/cm3
  Dvalue = 3.1028
  Group = -> [Br]
  conduct = 2
  density = 1
  expand = 3
  formula = G4_lBr
  name = G4_lBr
  specific = 4
FEATURE [App::DocumentObjectGroupPython] Kr  label="Kr : 1"  # scripted group (container) (typed FeaturePython)
  n = 1
  ref = Kr
FEATURE [App::DocumentObjectGroupPython] G4_lKr  # scripted group (container) (typed FeaturePython)
  Dunit = g/cm3
  Dvalue = 2.418
  Group = -> [Kr]
  conduct = 2
  density = 1
  expand = 3
  formula = G4_lKr
  name = G4_lKr
  specific = 4
FEATURE [App::DocumentObjectGroupPython] Xe  label="Xe : 1"  # scripted group (container) (typed FeaturePython)
  n = 1
  ref = Xe
FEATURE [App::DocumentObjectGroupPython] G4_lXe  # scripted group (container) (typed FeaturePython)
  Dunit = g/cm3
  Dvalue = 2.953
  Group = -> [Xe]
  conduct = 2
  density = 1
  expand = 3
  formula = G4_lXe
  name = G4_lXe
  specific = 4
FEATURE [App::DocumentObjectGroupPython] O_element107  label="O_element : 061"  # scripted group (container) (typed FeaturePython)
  n = 4
  ref = O_element
FEATURE [App::DocumentObjectGroupPython] Pb_element004  label="Pb_element : 002"  # scripted group (container) (typed FeaturePython)
  n = 1
  ref = Pb_element
FEATURE [App::DocumentObjectGroupPython] W_element005  label="W_element : 005"  # scripted group (container) (typed FeaturePython)
  n = 1
  ref = W_element
FEATURE [App::DocumentObjectGroupPython] G4_PbWO4  # scripted group (container) (typed FeaturePython)
  Dunit = g/cm3
  Dvalue = 8.28
  Group = -> [O_element107,Pb_element004,W_element005]
  conduct = 2
  density = 1
  expand = 3
  formula = G4_PbWO4
  name = G4_PbWO4
  specific = 4
FEATURE [App::DocumentObjectGroupPython] alactic  label="alactic : 1"  # scripted group (container) (typed FeaturePython)
  n = 1
  ref = alactic
FEATURE [App::DocumentObjectGroupPython] G4_Galactic  # scripted group (container) (typed FeaturePython)
  Dunit = g/cm3
  Dvalue = 0
  Group = -> [alactic]
  conduct = 2
  density = 1
  expand = 3
  formula = G4_Galactic
  name = G4_Galactic
  specific = 4
FEATURE [App::DocumentObjectGroupPython] RAPHITE_POROUS  label="RAPHITE_POROUS : 1"  # scripted group (container) (typed FeaturePython)
  n = 1
  ref = RAPHITE_POROUS
FEATURE [App::DocumentObjectGroupPython] G4_GRAPHITE_POROUS  # scripted group (container) (typed FeaturePython)
  Dunit = g/cm3
  Dvalue = 1.7
  Group = -> [RAPHITE_POROUS]
  conduct = 2
  density = 1
  expand = 3
  formula = G4_GRAPHITE_POROUS
  name = G4_GRAPHITE_POROUS
  specific = 4
FEATURE [App::DocumentObjectGroupPython] H_element115  label="H_element : 0.150"  # scripted group (container) (typed FeaturePython)
  n = 0.080538
FEATURE [App::DocumentObjectGroupPython] C_element125  label="C_element : 0.600"  # scripted group (container) (typed FeaturePython)
  n = 0.599848
FEATURE [App::DocumentObjectGroupPython] O_element108  label="O_element : 0.320"  # scripted group (container) (typed FeaturePython)
  n = 0.319614
FEATURE [App::DocumentObjectGroupPython] G4_LUCITE  # scripted group (container) (typed FeaturePython)
  Dunit = g/cm3
  Dvalue = 1.19
  Group = -> [H_element115,C_element125,O_element108]
  conduct = 2
  density = 1
  expand = 3
  formula = G4_LUCITE
  name = G4_LUCITE
  specific = 4
FEATURE [App::DocumentObjectGroupPython] Cu_element002  label="Cu_element : 62"  # scripted group (container) (typed FeaturePython)
  n = 62
  ref = Cu_element
FEATURE [App::DocumentObjectGroupPython] Zn_element002  label="Zn_element : 35"  # scripted group (container) (typed FeaturePython)
  n = 35
  ref = Zn_element
FEATURE [App::DocumentObjectGroupPython] Pb_element005  label="Pb_element : 3"  # scripted group (container) (typed FeaturePython)
  n = 3
  ref = Pb_element
FEATURE [App::DocumentObjectGroupPython] G4_BRASS  # scripted group (container) (typed FeaturePython)
  Dunit = g/cm3
  Dvalue = 8.52
  Group = -> [Cu_element002,Zn_element002,Pb_element005]
  conduct = 2
  density = 1
  expand = 3
  formula = G4_BRASS
  name = G4_BRASS
  specific = 4
FEATURE [App::DocumentObjectGroupPython] Cu_element003  label="Cu_element : 89"  # scripted group (container) (typed FeaturePython)
  n = 89
  ref = Cu_element
FEATURE [App::DocumentObjectGroupPython] Zn_element003  label="Zn_element : 9"  # scripted group (container) (typed FeaturePython)
  n = 9
  ref = Zn_element
FEATURE [App::DocumentObjectGroupPython] Pb_element006  label="Pb_element : 2"  # scripted group (container) (typed FeaturePython)
  n = 2
  ref = Pb_element
FEATURE [App::DocumentObjectGroupPython] G4_BRONZE  # scripted group (container) (typed FeaturePython)
  Dunit = g/cm3
  Dvalue = 8.82
  Group = -> [Cu_element003,Zn_element003,Pb_element006]
  conduct = 2
  density = 1
  expand = 3
  formula = G4_BRONZE
  name = G4_BRONZE
  specific = 4
FEATURE [App::DocumentObjectGroupPython] Fe_element008  label="Fe_element : 74"  # scripted group (container) (typed FeaturePython)
  n = 74
  ref = Fe_element
FEATURE [App::DocumentObjectGroupPython] Cr_element002  label="Cr_element : 18"  # scripted group (container) (typed FeaturePython)
  n = 18
  ref = Cr_element
FEATURE [App::DocumentObjectGroupPython] Ni_element002  label="Ni_element : 8"  # scripted group (container) (typed FeaturePython)
  n = 8
  ref = Ni_element
FEATURE [App::DocumentObjectGroupPython] G4_STAINLESS_STEEL  label="G4_STAINLESS-STEEL"  # scripted group (container) (typed FeaturePython)
  Dunit = g/cm3
  Dvalue = 8
  Group = -> [Fe_element008,Cr_element002,Ni_element002]
  conduct = 2
  density = 1
  expand = 3
  formula = G4_STAINLESS-STEEL
  name = G4_STAINLESS-STEEL
  specific = 4
FEATURE [App::DocumentObjectGroupPython] H_element116  label="H_element : 064"  # scripted group (container) (typed FeaturePython)
  n = 18
  ref = H_element
FEATURE [App::DocumentObjectGroupPython] C_element126  label="C_element : 071"  # scripted group (container) (typed FeaturePython)
  n = 12
  ref = C_element
FEATURE [App::DocumentObjectGroupPython] O_element109  label="O_element : 062"  # scripted group (container) (typed FeaturePython)
  n = 7
  ref = O_element
FEATURE [App::DocumentObjectGroupPython] G4_CR39  # scripted group (container) (typed FeaturePython)
  Dunit = g/cm3
  Dvalue = 1.32
  Group = -> [H_element116,C_element126,O_element109]
  conduct = 2
  density = 1
  expand = 3
  formula = G4_CR39
  name = G4_CR39
  specific = 4
FEATURE [App::DocumentObjectGroupPython] H_element117  label="H_element : 38"  # scripted group (container) (typed FeaturePython)
  n = 38
  ref = H_element
FEATURE [App::DocumentObjectGroupPython] C_element127  label="C_element : 072"  # scripted group (container) (typed FeaturePython)
  n = 18
  ref = C_element
FEATURE [App::DocumentObjectGroupPython] O_element110  label="O_element : 063"  # scripted group (container) (typed FeaturePython)
  n = 1
  ref = O_element
FEATURE [App::DocumentObjectGroupPython] G4_OCTADECANOL  # scripted group (container) (typed FeaturePython)
  Dunit = g/cm3
  Dvalue = 0.812
  Group = -> [H_element117,C_element127,O_element110]
  conduct = 2
  density = 1
  expand = 3
  formula = G4_OCTADECANOL
  name = G4_OCTADECANOL
  specific = 4
FEATURE [App::DocumentObjectGroupPython] HEP  # scripted group (container) (typed FeaturePython)
  Group = -> [G4_lH2,G4_lN2,G4_lO2,G4_lAr,G4_lBr,G4_lKr,G4_lXe,G4_PbWO4,G4_Galactic,G4_GRAPHITE_POROUS,G4_LUCITE,G4_BRASS,G4_BRONZE,G4_STAINLESS_STEEL,G4_CR39,G4_OCTADECANOL]
FEATURE [App::DocumentObjectGroupPython] C_element128  label="C_element : 073"  # scripted group (container) (typed FeaturePython)
  n = 14
  ref = C_element
FEATURE [App::DocumentObjectGroupPython] H_element118  label="H_element : 065"  # scripted group (container) (typed FeaturePython)
  n = 10
  ref = H_element
FEATURE [App::DocumentObjectGroupPython] O_element111  label="O_element : 064"  # scripted group (container) (typed FeaturePython)
  n = 2
  ref = O_element
FEATURE [App::DocumentObjectGroupPython] N_element050  label="N_element : 023"  # scripted group (container) (typed FeaturePython)
  n = 2
  ref = N_element
FEATURE [App::DocumentObjectGroupPython] G4_KEVLAR  # scripted group (container) (typed FeaturePython)
  Dunit = g/cm3
  Dvalue = 1.44
  Group = -> [C_element128,H_element118,O_element111,N_element050]
  conduct = 2
  density = 1
  expand = 3
  formula = G4_KEVLAR
  name = G4_KEVLAR
  specific = 4
FEATURE [App::DocumentObjectGroupPython] C_element129  label="C_element : 074"  # scripted group (container) (typed FeaturePython)
  n = 10
  ref = C_element
FEATURE [App::DocumentObjectGroupPython] H_element119  label="H_element : 066"  # scripted group (container) (typed FeaturePython)
  n = 8
  ref = H_element
FEATURE [App::DocumentObjectGroupPython] O_element112  label="O_element : 065"  # scripted group (container) (typed FeaturePython)
  n = 4
  ref = O_element
FEATURE [App::DocumentObjectGroupPython] G4_DACRON  # scripted group (container) (typed FeaturePython)
  Dunit = g/cm3
  Dvalue = 1.4
  Group = -> [C_element129,H_element119,O_element112]
  conduct = 2
  density = 1
  expand = 3
  formula = G4_DACRON
  name = G4_DACRON
  specific = 4
FEATURE [App::DocumentObjectGroupPython] C_element130  label="C_element : 075"  # scripted group (container) (typed FeaturePython)
  n = 4
  ref = C_element
FEATURE [App::DocumentObjectGroupPython] H_element120  label="H_element : 067"  # scripted group (container) (typed FeaturePython)
  n = 5
  ref = H_element
FEATURE [App::DocumentObjectGroupPython] Cl_element030  label="Cl_element : 016"  # scripted group (container) (typed FeaturePython)
  n = 1
  ref = Cl_element
FEATURE [App::DocumentObjectGroupPython] G4_NEOPRENE  # scripted group (container) (typed FeaturePython)
  Dunit = g/cm3
  Dvalue = 1.23
  Group = -> [C_element130,H_element120,Cl_element030]
  conduct = 2
  density = 1
  expand = 3
  formula = G4_NEOPRENE
  name = G4_NEOPRENE
  specific = 4
FEATURE [App::DocumentObjectGroupPython] Space  # scripted group (container) (typed FeaturePython)
  Group = -> [G4_KEVLAR,G4_DACRON,G4_NEOPRENE]
FEATURE [App::DocumentObjectGroupPython] H_element121  label="H_element : 068"  # scripted group (container) (typed FeaturePython)
  n = 5
  ref = H_element
FEATURE [App::DocumentObjectGroupPython] C_element131  label="C_element : 076"  # scripted group (container) (typed FeaturePython)
  n = 4
  ref = C_element
FEATURE [App::DocumentObjectGroupPython] N_element051  label="N_element : 3"  # scripted group (container) (typed FeaturePython)
  n = 3
  ref = N_element
FEATURE [App::DocumentObjectGroupPython] O_element113  label="O_element : 066"  # scripted group (container) (typed FeaturePython)
  n = 1
  ref = O_element
FEATURE [App::DocumentObjectGroupPython] G4_CYTOSINE  # scripted group (container) (typed FeaturePython)
  Dunit = g/cm3
  Dvalue = 1.55
  Group = -> [H_element121,C_element131,N_element051,O_element113]
  conduct = 2
  density = 1
  expand = 3
  formula = G4_CYTOSINE
  name = G4_CYTOSINE
  specific = 4
FEATURE [App::DocumentObjectGroupPython] H_element122  label="H_element : 069"  # scripted group (container) (typed FeaturePython)
  n = 6
  ref = H_element
FEATURE [App::DocumentObjectGroupPython] C_element132  label="C_element : 077"  # scripted group (container) (typed FeaturePython)
  n = 5
  ref = C_element
FEATURE [App::DocumentObjectGroupPython] N_element052  label="N_element : 024"  # scripted group (container) (typed FeaturePython)
  n = 2
  ref = N_element
FEATURE [App::DocumentObjectGroupPython] O_element114  label="O_element : 067"  # scripted group (container) (typed FeaturePython)
  n = 2
  ref = O_element
FEATURE [App::DocumentObjectGroupPython] G4_THYMINE  # scripted group (container) (typed FeaturePython)
  Dunit = g/cm3
  Dvalue = 1.23
  Group = -> [H_element122,C_element132,N_element052,O_element114]
  conduct = 2
  density = 1
  expand = 3
  formula = G4_THYMINE
  name = G4_THYMINE
  specific = 4
FEATURE [App::DocumentObjectGroupPython] H_element123  label="H_element : 070"  # scripted group (container) (typed FeaturePython)
  n = 4
  ref = H_element
FEATURE [App::DocumentObjectGroupPython] C_element133  label="C_element : 078"  # scripted group (container) (typed FeaturePython)
  n = 4
  ref = C_element
FEATURE [App::DocumentObjectGroupPython] N_element053  label="N_element : 025"  # scripted group (container) (typed FeaturePython)
  n = 2
  ref = N_element
FEATURE [App::DocumentObjectGroupPython] O_element115  label="O_element : 068"  # scripted group (container) (typed FeaturePython)
  n = 2
  ref = O_element
FEATURE [App::DocumentObjectGroupPython] G4_URACIL  # scripted group (container) (typed FeaturePython)
  Dunit = g/cm3
  Dvalue = 1.32
  Group = -> [H_element123,C_element133,N_element053,O_element115]
  conduct = 2
  density = 1
  expand = 3
  formula = G4_URACIL
  name = G4_URACIL
  specific = 4
FEATURE [App::DocumentObjectGroupPython] H_element124  label="H_element : 071"  # scripted group (container) (typed FeaturePython)
  n = 4
  ref = H_element
FEATURE [App::DocumentObjectGroupPython] C_element134  label="C_element : 079"  # scripted group (container) (typed FeaturePython)
  n = 5
  ref = C_element
FEATURE [App::DocumentObjectGroupPython] N_element054  label="N_element : 026"  # scripted group (container) (typed FeaturePython)
  n = 5
  ref = N_element
FEATURE [App::DocumentObjectGroupPython] G4_DNA_ADENINE  # scripted group (container) (typed FeaturePython)
  Dunit = g/cm3
  Dvalue = 1
  Group = -> [H_element124,C_element134,N_element054]
  conduct = 2
  density = 1
  expand = 3
  formula = G4_DNA_ADENINE
  name = G4_DNA_ADENINE
  specific = 4
FEATURE [App::DocumentObjectGroupPython] H_element125  label="H_element : 072"  # scripted group (container) (typed FeaturePython)
  n = 4
  ref = H_element
FEATURE [App::DocumentObjectGroupPython] C_element135  label="C_element : 080"  # scripted group (container) (typed FeaturePython)
  n = 5
  ref = C_element
FEATURE [App::DocumentObjectGroupPython] N_element055  label="N_element : 027"  # scripted group (container) (typed FeaturePython)
  n = 5
  ref = N_element
FEATURE [App::DocumentObjectGroupPython] O_element116  label="O_element : 069"  # scripted group (container) (typed FeaturePython)
  n = 1
  ref = O_element
FEATURE [App::DocumentObjectGroupPython] G4_DNA_GUANINE  # scripted group (container) (typed FeaturePython)
  Dunit = g/cm3
  Dvalue = 1
  Group = -> [H_element125,C_element135,N_element055,O_element116]
  conduct = 2
  density = 1
  expand = 3
  formula = G4_DNA_GUANINE
  name = G4_DNA_GUANINE
  specific = 4
FEATURE [App::DocumentObjectGroupPython] H_element126  label="H_element : 073"  # scripted group (container) (typed FeaturePython)
  n = 4
  ref = H_element
FEATURE [App::DocumentObjectGroupPython] C_element136  label="C_element : 081"  # scripted group (container) (typed FeaturePython)
  n = 4
  ref = C_element
FEATURE [App::DocumentObjectGroupPython] N_element056  label="N_element : 028"  # scripted group (container) (typed FeaturePython)
  n = 3
  ref = N_element
FEATURE [App::DocumentObjectGroupPython] O_element117  label="O_element : 070"  # scripted group (container) (typed FeaturePython)
  n = 1
  ref = O_element
FEATURE [App::DocumentObjectGroupPython] G4_DNA_CYTOSINE  # scripted group (container) (typed FeaturePython)
  Dunit = g/cm3
  Dvalue = 1
  Group = -> [H_element126,C_element136,N_element056,O_element117]
  conduct = 2
  density = 1
  expand = 3
  formula = G4_DNA_CYTOSINE
  name = G4_DNA_CYTOSINE
  specific = 4
FEATURE [App::DocumentObjectGroupPython] H_element127  label="H_element : 074"  # scripted group (container) (typed FeaturePython)
  n = 5
  ref = H_element
FEATURE [App::DocumentObjectGroupPython] C_element137  label="C_element : 082"  # scripted group (container) (typed FeaturePython)
  n = 5
  ref = C_element
FEATURE [App::DocumentObjectGroupPython] N_element057  label="N_element : 029"  # scripted group (container) (typed FeaturePython)
  n = 2
  ref = N_element
FEATURE [App::DocumentObjectGroupPython] O_element118  label="O_element : 071"  # scripted group (container) (typed FeaturePython)
  n = 2
  ref = O_element
FEATURE [App::DocumentObjectGroupPython] G4_DNA_THYMINE  # scripted group (container) (typed FeaturePython)
  Dunit = g/cm3
  Dvalue = 1
  Group = -> [H_element127,C_element137,N_element057,O_element118]
  conduct = 2
  density = 1
  expand = 3
  formula = G4_DNA_THYMINE
  name = G4_DNA_THYMINE
  specific = 4
FEATURE [App::DocumentObjectGroupPython] H_element128  label="H_element : 075"  # scripted group (container) (typed FeaturePython)
  n = 3
  ref = H_element
FEATURE [App::DocumentObjectGroupPython] C_element138  label="C_element : 083"  # scripted group (container) (typed FeaturePython)
  n = 4
  ref = C_element
FEATURE [App::DocumentObjectGroupPython] N_element058  label="N_element : 030"  # scripted group (container) (typed FeaturePython)
  n = 2
  ref = N_element
FEATURE [App::DocumentObjectGroupPython] O_element119  label="O_element : 072"  # scripted group (container) (typed FeaturePython)
  n = 2
  ref = O_element
FEATURE [App::DocumentObjectGroupPython] G4_DNA_URACIL  # scripted group (container) (typed FeaturePython)
  Dunit = g/cm3
  Dvalue = 1
  Group = -> [H_element128,C_element138,N_element058,O_element119]
  conduct = 2
  density = 1
  expand = 3
  formula = G4_DNA_URACIL
  name = G4_DNA_URACIL
  specific = 4
FEATURE [App::DocumentObjectGroupPython] H_element129  label="H_element : 076"  # scripted group (container) (typed FeaturePython)
  n = 10
  ref = H_element
FEATURE [App::DocumentObjectGroupPython] C_element139  label="C_element : 084"  # scripted group (container) (typed FeaturePython)
  n = 10
  ref = C_element
FEATURE [App::DocumentObjectGroupPython] N_element059  label="N_element : 031"  # scripted group (container) (typed FeaturePython)
  n = 5
  ref = N_element
FEATURE [App::DocumentObjectGroupPython] O_element120  label="O_element : 073"  # scripted group (container) (typed FeaturePython)
  n = 4
  ref = O_element
FEATURE [App::DocumentObjectGroupPython] G4_DNA_ADENOSINE  # scripted group (container) (typed FeaturePython)
  Dunit = g/cm3
  Dvalue = 1
  Group = -> [H_element129,C_element139,N_element059,O_element120]
  conduct = 2
  density = 1
  expand = 3
  formula = G4_DNA_ADENOSINE
  name = G4_DNA_ADENOSINE
  specific = 4
FEATURE [App::DocumentObjectGroupPython] H_element130  label="H_element : 077"  # scripted group (container) (typed FeaturePython)
  n = 10
  ref = H_element
FEATURE [App::DocumentObjectGroupPython] C_element140  label="C_element : 085"  # scripted group (container) (typed FeaturePython)
  n = 10
  ref = C_element
FEATURE [App::DocumentObjectGroupPython] N_element060  label="N_element : 032"  # scripted group (container) (typed FeaturePython)
  n = 5
  ref = N_element
FEATURE [App::DocumentObjectGroupPython] O_element121  label="O_element : 074"  # scripted group (container) (typed FeaturePython)
  n = 5
  ref = O_element
FEATURE [App::DocumentObjectGroupPython] G4_DNA_GUANOSINE  # scripted group (container) (typed FeaturePython)
  Dunit = g/cm3
  Dvalue = 1
  Group = -> [H_element130,C_element140,N_element060,O_element121]
  conduct = 2
  density = 1
  expand = 3
  formula = G4_DNA_GUANOSINE
  name = G4_DNA_GUANOSINE
  specific = 4
FEATURE [App::DocumentObjectGroupPython] H_element131  label="H_element : 078"  # scripted group (container) (typed FeaturePython)
  n = 10
  ref = H_element
FEATURE [App::DocumentObjectGroupPython] C_element141  label="C_element : 086"  # scripted group (container) (typed FeaturePython)
  n = 9
  ref = C_element
FEATURE [App::DocumentObjectGroupPython] N_element061  label="N_element : 033"  # scripted group (container) (typed FeaturePython)
  n = 3
  ref = N_element
FEATURE [App::DocumentObjectGroupPython] O_element122  label="O_element : 075"  # scripted group (container) (typed FeaturePython)
  n = 5
  ref = O_element
FEATURE [App::DocumentObjectGroupPython] G4_DNA_CYTIDINE  # scripted group (container) (typed FeaturePython)
  Dunit = g/cm3
  Dvalue = 1
  Group = -> [H_element131,C_element141,N_element061,O_element122]
  conduct = 2
  density = 1
  expand = 3
  formula = G4_DNA_CYTIDINE
  name = G4_DNA_CYTIDINE
  specific = 4
FEATURE [App::DocumentObjectGroupPython] H_element132  label="H_element : 079"  # scripted group (container) (typed FeaturePython)
  n = 9
  ref = H_element
FEATURE [App::DocumentObjectGroupPython] C_element142  label="C_element : 087"  # scripted group (container) (typed FeaturePython)
  n = 9
  ref = C_element
FEATURE [App::DocumentObjectGroupPython] N_element062  label="N_element : 034"  # scripted group (container) (typed FeaturePython)
  n = 2
  ref = N_element
FEATURE [App::DocumentObjectGroupPython] O_element123  label="O_element : 076"  # scripted group (container) (typed FeaturePython)
  n = 6
  ref = O_element
FEATURE [App::DocumentObjectGroupPython] G4_DNA_URIDINE  # scripted group (container) (typed FeaturePython)
  Dunit = g/cm3
  Dvalue = 1
  Group = -> [H_element132,C_element142,N_element062,O_element123]
  conduct = 2
  density = 1
  expand = 3
  formula = G4_DNA_URIDINE
  name = G4_DNA_URIDINE
  specific = 4
FEATURE [App::DocumentObjectGroupPython] H_element133  label="H_element : 080"  # scripted group (container) (typed FeaturePython)
  n = 11
  ref = H_element
FEATURE [App::DocumentObjectGroupPython] C_element143  label="C_element : 088"  # scripted group (container) (typed FeaturePython)
  n = 10
  ref = C_element
FEATURE [App::DocumentObjectGroupPython] N_element063  label="N_element : 035"  # scripted group (container) (typed FeaturePython)
  n = 2
  ref = N_element
FEATURE [App::DocumentObjectGroupPython] O_element124  label="O_element : 077"  # scripted group (container) (typed FeaturePython)
  n = 6
  ref = O_element
FEATURE [App::DocumentObjectGroupPython] G4_DNA_METHYLURIDINE  # scripted group (container) (typed FeaturePython)
  Dunit = g/cm3
  Dvalue = 1
  Group = -> [H_element133,C_element143,N_element063,O_element124]
  conduct = 2
  density = 1
  expand = 3
  formula = G4_DNA_METHYLURIDINE
  name = G4_DNA_METHYLURIDINE
  specific = 4
FEATURE [App::DocumentObjectGroupPython] P_element014  label="P_element : 003"  # scripted group (container) (typed FeaturePython)
  n = 1
  ref = P_element
FEATURE [App::DocumentObjectGroupPython] O_element125  label="O_element : 078"  # scripted group (container) (typed FeaturePython)
  n = 3
  ref = O_element
FEATURE [App::DocumentObjectGroupPython] G4_DNA_MONOPHOSPHATE  # scripted group (container) (typed FeaturePython)
  Dunit = g/cm3
  Dvalue = 1
  Group = -> [P_element014,O_element125]
  conduct = 2
  density = 1
  expand = 3
  formula = G4_DNA_MONOPHOSPHATE
  name = G4_DNA_MONOPHOSPHATE
  specific = 4
FEATURE [App::DocumentObjectGroupPython] H_element134  label="H_element : 081"  # scripted group (container) (typed FeaturePython)
  n = 10
  ref = H_element
FEATURE [App::DocumentObjectGroupPython] C_element144  label="C_element : 089"  # scripted group (container) (typed FeaturePython)
  n = 10
  ref = C_element
FEATURE [App::DocumentObjectGroupPython] N_element064  label="N_element : 036"  # scripted group (container) (typed FeaturePython)
  n = 5
  ref = N_element
FEATURE [App::DocumentObjectGroupPython] O_element126  label="O_element : 079"  # scripted group (container) (typed FeaturePython)
  n = 7
  ref = O_element
FEATURE [App::DocumentObjectGroupPython] P_element015  label="P_element : 004"  # scripted group (container) (typed FeaturePython)
  n = 1
  ref = P_element
FEATURE [App::DocumentObjectGroupPython] G4_DNA_A  # scripted group (container) (typed FeaturePython)
  Dunit = g/cm3
  Dvalue = 1
  Group = -> [H_element134,C_element144,N_element064,O_element126,P_element015]
  conduct = 2
  density = 1
  expand = 3
  formula = G4_DNA_A
  name = G4_DNA_A
  specific = 4
FEATURE [App::DocumentObjectGroupPython] H_element135  label="H_element : 082"  # scripted group (container) (typed FeaturePython)
  n = 10
  ref = H_element
FEATURE [App::DocumentObjectGroupPython] C_element145  label="C_element : 090"  # scripted group (container) (typed FeaturePython)
  n = 10
  ref = C_element
FEATURE [App::DocumentObjectGroupPython] N_element065  label="N_element : 037"  # scripted group (container) (typed FeaturePython)
  n = 5
  ref = N_element
FEATURE [App::DocumentObjectGroupPython] O_element127  label="O_element : 8"  # scripted group (container) (typed FeaturePython)
  n = 8
  ref = O_element
FEATURE [App::DocumentObjectGroupPython] P_element016  label="P_element : 005"  # scripted group (container) (typed FeaturePython)
  n = 1
  ref = P_element
FEATURE [App::DocumentObjectGroupPython] G4_DNA_G  # scripted group (container) (typed FeaturePython)
  Dunit = g/cm3
  Dvalue = 1
  Group = -> [H_element135,C_element145,N_element065,O_element127,P_element016]
  conduct = 2
  density = 1
  expand = 3
  formula = G4_DNA_G
  name = G4_DNA_G
  specific = 4
FEATURE [App::DocumentObjectGroupPython] H_element136  label="H_element : 083"  # scripted group (container) (typed FeaturePython)
  n = 10
  ref = H_element
FEATURE [App::DocumentObjectGroupPython] C_element146  label="C_element : 091"  # scripted group (container) (typed FeaturePython)
  n = 9
  ref = C_element
FEATURE [App::DocumentObjectGroupPython] N_element066  label="N_element : 038"  # scripted group (container) (typed FeaturePython)
  n = 3
  ref = N_element
FEATURE [App::DocumentObjectGroupPython] O_element128  label="O_element : 080"  # scripted group (container) (typed FeaturePython)
  n = 8
  ref = O_element
FEATURE [App::DocumentObjectGroupPython] P_element017  label="P_element : 006"  # scripted group (container) (typed FeaturePython)
  n = 1
  ref = P_element
FEATURE [App::DocumentObjectGroupPython] G4_DNA_C  # scripted group (container) (typed FeaturePython)
  Dunit = g/cm3
  Dvalue = 1
  Group = -> [H_element136,C_element146,N_element066,O_element128,P_element017]
  conduct = 2
  density = 1
  expand = 3
  formula = G4_DNA_C
  name = G4_DNA_C
  specific = 4
FEATURE [App::DocumentObjectGroupPython] H_element137  label="H_element : 084"  # scripted group (container) (typed FeaturePython)
  n = 9
  ref = H_element
FEATURE [App::DocumentObjectGroupPython] C_element147  label="C_element : 092"  # scripted group (container) (typed FeaturePython)
  n = 9
  ref = C_element
FEATURE [App::DocumentObjectGroupPython] N_element067  label="N_element : 039"  # scripted group (container) (typed FeaturePython)
  n = 2
  ref = N_element
FEATURE [App::DocumentObjectGroupPython] O_element129  label="O_element : 9"  # scripted group (container) (typed FeaturePython)
  n = 9
  ref = O_element
FEATURE [App::DocumentObjectGroupPython] P_element018  label="P_element : 007"  # scripted group (container) (typed FeaturePython)
  n = 1
  ref = P_element
FEATURE [App::DocumentObjectGroupPython] G4_DNA_U  # scripted group (container) (typed FeaturePython)
  Dunit = g/cm3
  Dvalue = 1
  Group = -> [H_element137,C_element147,N_element067,O_element129,P_element018]
  conduct = 2
  density = 1
  expand = 3
  formula = G4_DNA_U
  name = G4_DNA_U
  specific = 4
FEATURE [App::DocumentObjectGroupPython] H_element138  label="H_element : 085"  # scripted group (container) (typed FeaturePython)
  n = 11
  ref = H_element
FEATURE [App::DocumentObjectGroupPython] C_element148  label="C_element : 093"  # scripted group (container) (typed FeaturePython)
  n = 10
  ref = C_element
FEATURE [App::DocumentObjectGroupPython] N_element068  label="N_element : 040"  # scripted group (container) (typed FeaturePython)
  n = 2
  ref = N_element
FEATURE [App::DocumentObjectGroupPython] O_element130  label="O_element : 081"  # scripted group (container) (typed FeaturePython)
  n = 9
  ref = O_element
FEATURE [App::DocumentObjectGroupPython] P_element019  label="P_element : 008"  # scripted group (container) (typed FeaturePython)
  n = 1
  ref = P_element
FEATURE [App::DocumentObjectGroupPython] G4_DNA_MU  # scripted group (container) (typed FeaturePython)
  Dunit = g/cm3
  Dvalue = 1
  Group = -> [H_element138,C_element148,N_element068,O_element130,P_element019]
  conduct = 2
  density = 1
  expand = 3
  formula = G4_DNA_MU
  name = G4_DNA_MU
  specific = 4
FEATURE [App::DocumentObjectGroupPython] BioChemical  # scripted group (container) (typed FeaturePython)
  Group = -> [G4_CYTOSINE,G4_THYMINE,G4_URACIL,G4_DNA_ADENINE,G4_DNA_GUANINE,G4_DNA_CYTOSINE,G4_DNA_THYMINE,G4_DNA_URACIL,G4_DNA_ADENOSINE,G4_DNA_GUANOSINE,G4_DNA_CYTIDINE,G4_DNA_URIDINE,G4_DNA_METHYLURIDINE,G4_DNA_MONOPHOSPHATE,G4_DNA_A,G4_DNA_G,G4_DNA_C,G4_DNA_U,G4_DNA_MU]
FEATURE [App::DocumentObjectGroupPython] G4Materials  # scripted group (container) (typed FeaturePython)
  Group = -> [NIST,Element,HEP,Space,BioChemical]
  version = 1
FEATURE [App::DocumentObjectGroupPython] Geant4  # scripted group (container) (typed FeaturePython)
  Group = -> [G4Isotopes,G4Elements,G4Materials]
FEATURE [App::DocumentObjectGroupPython] Materials  # scripted group (container) (typed FeaturePython)
  Group = -> [Geant4]
FEATURE [Part::FeaturePython] GDMLBox_WorldBox  # WARN: FeaturePython — macro-defined, semantics opaque (R4)
  lunit = 2
  material = 5
  x = 452.792
  y = 452.792
  z = 169
FEATURE [Part::FeaturePython] GDMLBox_Box  # WARN: FeaturePython — macro-defined, semantics opaque (R4)
  Placement = pos=(20,0,0) rot=(0,0,1;0rad)
  lunit = 2
  material = 0
  x = 10
  y = 10
  z = 10
FEATURE [Part::FeaturePython] GDMLTube  # WARN: FeaturePython — macro-defined, semantics opaque (R4)
  Placement = pos=(17,-4,0) rot=(0,0,1;0rad)
  aunit = 1
  deltaphi = 90
  lunit = 2
  material = 0
  rmax = 7
  rmin = 5
  startphi = 0
  z = 7
FEATURE [App::Part] LV_Tube
  Group = -> [GDMLTube]
  Origin = -> Origin003
  SkinSurface = 0
FEATURE [App::Part] LV_Box
  Group = -> [GDMLBox_Box,LV_Tube]
  Origin = -> Origin002
  Placement = pos=(0,0,0) rot=(0,0,1;-0.523599rad)
FEATURE [Part::FeaturePython] Array  # Draft array (typed FeaturePython)
  AlwaysSyncPlacement = false
  Angle = 180
  ArrayType = 1
  Axis = (0,0,1)
  Base = -> LV_Box
  Center = (-20,-20,0)
  Count = 5
  ExpandArray = false
  Fuse = false
  IntervalAxis = (0,0,0)
  IntervalX = (100,0,0)
  IntervalY = (0,100,0)
  IntervalZ = (0,0,100)
  NumberCircles = 3
  NumberPolar = 5
  NumberX = 2
  NumberY = 2
  NumberZ = 1
  PlacementList = 5 placements: [(0,0,0),(-20,8.28427,0),(-40,3.55271e-15,0),(-48.2843,-20,0),(-40,-40,0)]
  RadialDistance = 50
  ScaleList = (5) [(1,1,1),(1,1,1),(1,1,1),(1,1,1),(1,1,1)]
  Symmetry = 1
  TangentialDistance = 25
FEATURE [App::Part] Part  label="experiment"
  Group = -> [LV_Box,Array]
  Origin = -> Origin001
FEATURE [Part::FeaturePython] Array001  # Draft array (typed FeaturePython)
  AlwaysSyncPlacement = false
  Angle = 360
  ArrayType = 0
  Axis = (0,0,1)
  Base = -> Part
  Center = (0,0,0)
  Count = 4
  ExpandArray = false
  Fuse = true
  IntervalAxis = (0,0,0)
  IntervalX = (150,0,0)
  IntervalY = (0,150,0)
  IntervalZ = (0,0,100)
  NumberCircles = 3
  NumberPolar = 5
  NumberX = 2
  NumberY = 2
  NumberZ = 1
  PlacementList = 4 placements: [(0,0,0),(0,150,0),(150,0,0),(150,150,0)]
  RadialDistance = 50
  ScaleList = (4) [(1,1,1),(1,1,1),(1,1,1),(1,1,1)]
  Symmetry = 1
  TangentialDistance = 25
FEATURE [App::Part] Part001
  Group = -> [Part,Array001]
  Origin = -> Origin004
FEATURE [App::Part] worldVOL
  Group = -> [GDMLBox_WorldBox,Part001]
  Origin = -> Origin
